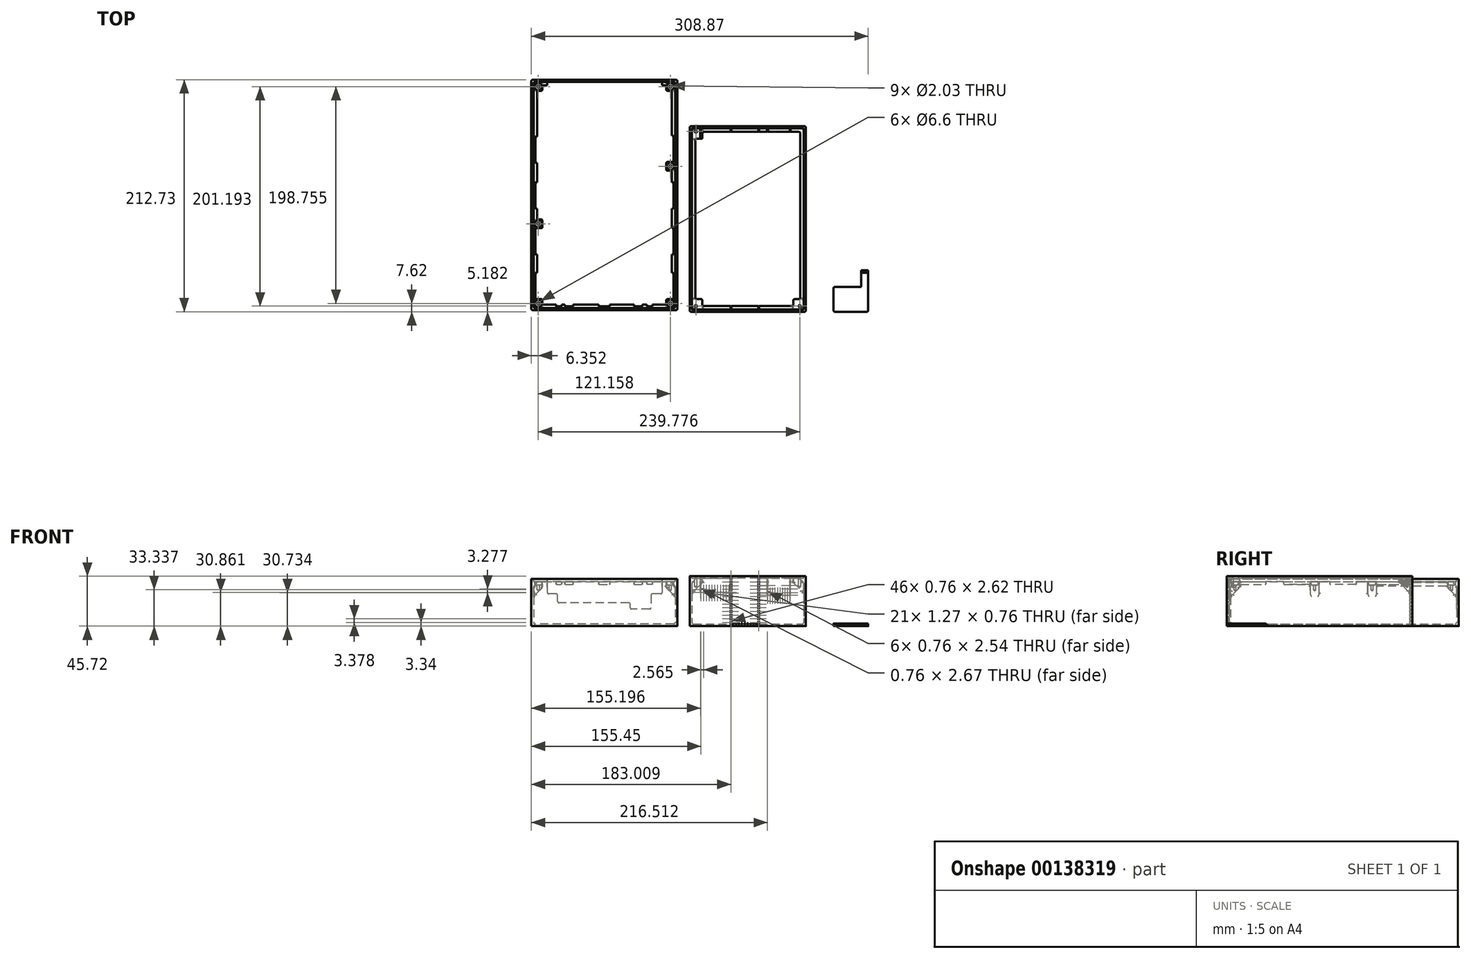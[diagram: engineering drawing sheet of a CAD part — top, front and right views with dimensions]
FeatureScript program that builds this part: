
annotation { "Feature Type Name" : "Feature", "Feature Type Description" : "" }
export const myFeature = defineFeature(function(context is Context, id is Id, definition is map)
    precondition{}
    {
        {
            var Q0;
            Q0=qCreatedBy(makeId("Top.planeOp"),FACE);
            var sketch = newSketch(context, id + "F0", { "sketchPlane" : qUnion([Q0])});
            skLineSegment(sketch, "E0.bottom", {"start": v(5.08, 5.08) * mm, "end": v(111.5, 5.08) * mm});
            skLineSegment(sketch, "E0.top", {"start": v(5.08, 175.13) * mm, "end": v(111.5, 175.13) * mm});
            skLineSegment(sketch, "E0.left", {"start": v(5.08, 5.08) * mm, "end": v(5.08, 175.13) * mm});
            skLineSegment(sketch, "E0.right", {"start": v(111.5, 5.08) * mm, "end": v(111.5, 175.13) * mm});
            skSolve(sketch);
        }
        {
            var Q0;
            Q0 = qSketchRegion(id + "F0", true);
            extrude(context, id + "F1", {"entities" : qUnion([Q0]), "depth" : 45.72 * mm, "offsetDistance" : 25.4 * mm});
        }
        {
            var Q0;
            Q0=makeQuery(id+"F1.opExtrude","CAP_FACE",FACE,{"disambiguationData":[OSD([sQuery(id+"F0.wireOp",EDGE,"E0.bottom"),sQuery(id+"F0.wireOp",EDGE,"E0.top"),sQuery(id+"F0.wireOp",EDGE,"E0.left"),sQuery(id+"F0.wireOp",EDGE,"E0.right")])],"isStart":false});
            shell(context, id + "F2", {"entities" : qUnion([Q0]), "thickness" : 2.03 * mm});
        }
        {
            var Q0;
            Q0=makeQuery(id+"F1.opExtrude","CAP_FACE",FACE,{"disambiguationData":[OSD([sQuery(id+"F0.wireOp",EDGE,"E0.bottom"),sQuery(id+"F0.wireOp",EDGE,"E0.top"),sQuery(id+"F0.wireOp",EDGE,"E0.left"),sQuery(id+"F0.wireOp",EDGE,"E0.right")])],"isStart":false});
            var sketch = newSketch(context, id + "F3", { "sketchPlane" : qUnion([Q0])});
            skLineSegment(sketch, "E1.0", {"start": v(16.64, 10.29) * mm, "end": v(99.95, 10.29) * mm});
            skLineSegment(sketch, "E1.1", {"start": v(10.29, 16.64) * mm, "end": v(10.29, 163.58) * mm});
            skLineSegment(sketch, "E1.2", {"start": v(16.64, 169.93) * mm, "end": v(106.3, 169.93) * mm});
            skLineSegment(sketch, "E1.3", {"start": v(106.3, 16.64) * mm, "end": v(106.3, 169.93) * mm});
            skLineSegment(sketch, "E2", {"start": v(109.47, 7.11) * mm, "end": v(7.11, 7.11) * mm});
            skLineSegment(sketch, "E3", {"start": v(7.11, 7.11) * mm, "end": v(7.11, 173.1) * mm});
            skLineSegment(sketch, "E4", {"start": v(7.11, 173.1) * mm, "end": v(109.47, 173.1) * mm});
            skLineSegment(sketch, "E5", {"start": v(109.47, 173.1) * mm, "end": v(109.47, 7.11) * mm});
            skLineSegment(sketch, "E6", {"start": v(16.64, 10.29) * mm, "end": v(16.64, 16.64) * mm});
            skLineSegment(sketch, "E7", {"start": v(16.64, 16.64) * mm, "end": v(10.29, 16.64) * mm});
            skLineSegment(sketch, "E8", {"start": v(106.3, 16.64) * mm, "end": v(99.95, 16.64) * mm});
            skLineSegment(sketch, "E9", {"start": v(99.95, 16.64) * mm, "end": v(99.95, 10.29) * mm});
            skLineSegment(sketch, "E10", {"start": v(16.64, 169.93) * mm, "end": v(16.64, 163.58) * mm});
            skLineSegment(sketch, "E11", {"start": v(16.64, 163.58) * mm, "end": v(10.29, 163.58) * mm});
            skSolve(sketch);
        }
        {
            var Q0;
            Q0 = qSketchRegion(id + "F3", true);
            extrude(context, id + "F4", {"entities" : qUnion([Q0]), "operationType" : NewBodyOperationType.ADD, "oppositeDirection" : true, "depth" : 15.24 * mm, "offsetDistance" : 25.4 * mm});
        }
        {
            var Q0;
            Q0=makeQuery(id+"F4.boolean.opBoolean","MERGE",FACE,{"derivedFrom":[makeQuery(id+"F1.opExtrude","CAP_FACE",FACE,{"disambiguationData":[OSD([sQuery(id+"F0.wireOp",EDGE,"E0.bottom"),sQuery(id+"F0.wireOp",EDGE,"E0.top"),sQuery(id+"F0.wireOp",EDGE,"E0.left"),sQuery(id+"F0.wireOp",EDGE,"E0.right")])],"isStart":false}),makeQuery(id+"F4.opExtrude","CAP_FACE",FACE,{"disambiguationData":[OSD([sQuery(id+"F3.wireOp",EDGE,"E1.0"),sQuery(id+"F3.wireOp",EDGE,"E1.1"),sQuery(id+"F3.wireOp",EDGE,"E1.2"),sQuery(id+"F3.wireOp",EDGE,"E1.3"),sQuery(id+"F3.wireOp",EDGE,"E2"),sQuery(id+"F3.wireOp",EDGE,"E3"),sQuery(id+"F3.wireOp",EDGE,"E4"),sQuery(id+"F3.wireOp",EDGE,"E5")])],"isStart":true})]});
            var sketch = newSketch(context, id + "F5", { "sketchPlane" : qUnion([Q0])});
            skLineSegment(sketch, "E12.0", {"start": v(7.11, 7.11) * mm, "end": v(109.47, 7.11) * mm});
            skLineSegment(sketch, "E12.1", {"start": v(7.11, 7.11) * mm, "end": v(7.11, 173.1) * mm});
            skLineSegment(sketch, "E12.2", {"start": v(7.11, 173.1) * mm, "end": v(109.47, 173.1) * mm});
            skLineSegment(sketch, "E12.3", {"start": v(109.47, 7.11) * mm, "end": v(109.47, 173.1) * mm});
            skSolve(sketch);
        }
        {
            var Q0;
            Q0 = qSketchRegion(id + "F5", true);
            extrude(context, id + "F6", {"entities" : qUnion([Q0]), "operationType" : NewBodyOperationType.REMOVE, "oppositeDirection" : true, "depth" : 1.65 * mm, "offsetDistance" : 25.4 * mm});
        }
        {
            var Q0;
            Q0=makeQuery(id+"F4.opExtrude","CAP_EDGE",EDGE,{"disambiguationData":[OSD([sQuery(id+"F3.wireOp",EDGE,"E1.0")])],"isStart":false});
            var Q1;
            Q1=makeQuery(id+"F4.opExtrude","CAP_EDGE",EDGE,{"disambiguationData":[OSD([sQuery(id+"F3.wireOp",EDGE,"E1.1")])],"isStart":false});
            var Q2;
            Q2=makeQuery(id+"F4.opExtrude","CAP_EDGE",EDGE,{"disambiguationData":[OSD([sQuery(id+"F3.wireOp",EDGE,"E1.3")])],"isStart":false});
            var Q3;
            Q3=makeQuery(id+"F4.opExtrude","CAP_EDGE",EDGE,{"disambiguationData":[OSD([sQuery(id+"F3.wireOp",EDGE,"E1.2")])],"isStart":false});
            chamfer(context, id + "F7", {"entities" : qUnion([Q0, Q1, Q2, Q3]), "width" : 12.7 * mm, "tangentPropagation" : true});
        }
        {
            var Q0;
            Q0=makeQuery(id+"F4.opExtrude","CAP_EDGE",EDGE,{"disambiguationData":[OSD([sQuery(id+"F3.wireOp",EDGE,"E8")])],"isStart":false});
            var Q1;
            Q1=makeQuery(id+"F4.opExtrude","CAP_EDGE",EDGE,{"disambiguationData":[OSD([sQuery(id+"F3.wireOp",EDGE,"E9")])],"isStart":false});
            var Q2;
            Q2=makeQuery(id+"F4.opExtrude","CAP_EDGE",EDGE,{"disambiguationData":[OSD([sQuery(id+"F3.wireOp",EDGE,"E11")])],"isStart":false});
            var Q3;
            Q3=makeQuery(id+"F4.opExtrude","CAP_EDGE",EDGE,{"disambiguationData":[OSD([sQuery(id+"F3.wireOp",EDGE,"E10")])],"isStart":false});
            var Q4;
            Q4=makeQuery(id+"F4.opExtrude","CAP_EDGE",EDGE,{"disambiguationData":[OSD([sQuery(id+"F3.wireOp",EDGE,"E7")])],"isStart":false});
            var Q5;
            Q5=makeQuery(id+"F4.opExtrude","CAP_EDGE",EDGE,{"disambiguationData":[OSD([sQuery(id+"F3.wireOp",EDGE,"E6")])],"isStart":false});
            chamfer(context, id + "F8", {"entities" : qUnion([Q0, Q1, Q2, Q3, Q4, Q5]), "width" : 9.52 * mm, "tangentPropagation" : true});
        }
        {
            var Q0;
            Q0=makeQuery(id+"F4.opExtrude","SWEPT_EDGE",EDGE,{"disambiguationData":[OSD([sQuery(id+"F3.wireOp",EDGE,"E6"),sQuery(id+"F3.wireOp",EDGE,"E7")])]});
            var Q1;
            {var subQ0=sQuery(id+"F3.wireOp",EDGE,"E7");Q1=makeQuery(id+"F8.opChamfer","BLEND_EDGE",EDGE,{"blendedFrom":[makeQuery(id+"F4.opExtrude","CAP_EDGE",EDGE,{"disambiguationData":[OSD([subQ0])],"isStart":false}),makeQuery(id+"F4.opExtrude","SWEPT_FACE",FACE,{"disambiguationData":[OSD([subQ0])]})],"blendedInto":[makeQuery(id+"F4.opExtrude","SWEPT_FACE",FACE,{"disambiguationData":[OSD([subQ0])]})]});}
            var Q2;
            Q2=makeQuery(id+"F8.opChamfer","BLEND_EDGE",EDGE,{"blendedFrom":[makeQuery(id+"F4.opExtrude","CAP_EDGE",EDGE,{"disambiguationData":[OSD([sQuery(id+"F3.wireOp",EDGE,"E6")])],"isStart":false}),makeQuery(id+"F4.opExtrude","CAP_EDGE",EDGE,{"disambiguationData":[OSD([sQuery(id+"F3.wireOp",EDGE,"E7")])],"isStart":false})],"blendedInto":[]});
            var Q3;
            {var subQ0=sQuery(id+"F3.wireOp",EDGE,"E6");Q3=makeQuery(id+"F8.opChamfer","BLEND_EDGE",EDGE,{"blendedFrom":[makeQuery(id+"F4.opExtrude","CAP_EDGE",EDGE,{"disambiguationData":[OSD([subQ0])],"isStart":false}),makeQuery(id+"F4.opExtrude","SWEPT_FACE",FACE,{"disambiguationData":[OSD([subQ0])]})],"blendedInto":[makeQuery(id+"F4.opExtrude","SWEPT_FACE",FACE,{"disambiguationData":[OSD([subQ0])]})]});}
            var Q4;
            {var subQ0=sQuery(id+"F3.wireOp",EDGE,"E1.0");Q4=makeQuery(id+"F7.opChamfer","BLEND_EDGE",EDGE,{"blendedFrom":[makeQuery(id+"F4.opExtrude","CAP_EDGE",EDGE,{"disambiguationData":[OSD([subQ0])],"isStart":false}),makeQuery(id+"F4.opExtrude","SWEPT_FACE",FACE,{"disambiguationData":[OSD([subQ0])]})],"blendedInto":[makeQuery(id+"F4.opExtrude","SWEPT_FACE",FACE,{"disambiguationData":[OSD([subQ0])]})]});}
            var Q5;
            Q5=makeQuery(id+"F7.opChamfer","BLEND_EDGE",EDGE,{"blendedFrom":[makeQuery(id+"F4.opExtrude","CAP_EDGE",EDGE,{"disambiguationData":[OSD([sQuery(id+"F3.wireOp",EDGE,"E1.0")])],"isStart":false}),makeQuery(id+"F2.opShell","OFFSET_FACE",FACE,{"disambiguationData":[OSD([sQuery(id+"F0.wireOp",EDGE,"E0.bottom")])]})],"blendedInto":[makeQuery(id+"F2.opShell","OFFSET_FACE",FACE,{"disambiguationData":[OSD([sQuery(id+"F0.wireOp",EDGE,"E0.bottom")])]})]});
            var Q6;
            {var subQ0=sQuery(id+"F3.wireOp",EDGE,"E1.1");Q6=makeQuery(id+"F7.opChamfer","BLEND_EDGE",EDGE,{"blendedFrom":[makeQuery(id+"F4.opExtrude","CAP_EDGE",EDGE,{"disambiguationData":[OSD([subQ0])],"isStart":false}),makeQuery(id+"F4.opExtrude","SWEPT_FACE",FACE,{"disambiguationData":[OSD([subQ0])]})],"blendedInto":[makeQuery(id+"F4.opExtrude","SWEPT_FACE",FACE,{"disambiguationData":[OSD([subQ0])]})]});}
            var Q7;
            Q7=makeQuery(id+"F4.opExtrude","SWEPT_EDGE",EDGE,{"disambiguationData":[OSD([sQuery(id+"F3.wireOp",EDGE,"E8"),sQuery(id+"F3.wireOp",EDGE,"E9")])]});
            var Q8;
            Q8=makeQuery(id+"F8.opChamfer","BLEND_EDGE",EDGE,{"blendedFrom":[makeQuery(id+"F4.opExtrude","CAP_EDGE",EDGE,{"disambiguationData":[OSD([sQuery(id+"F3.wireOp",EDGE,"E8")])],"isStart":false}),makeQuery(id+"F4.opExtrude","CAP_EDGE",EDGE,{"disambiguationData":[OSD([sQuery(id+"F3.wireOp",EDGE,"E9")])],"isStart":false})],"blendedInto":[]});
            var Q9;
            {var subQ0=sQuery(id+"F3.wireOp",EDGE,"E9");Q9=makeQuery(id+"F8.opChamfer","BLEND_EDGE",EDGE,{"blendedFrom":[makeQuery(id+"F4.opExtrude","CAP_EDGE",EDGE,{"disambiguationData":[OSD([subQ0])],"isStart":false}),makeQuery(id+"F4.opExtrude","SWEPT_FACE",FACE,{"disambiguationData":[OSD([subQ0])]})],"blendedInto":[makeQuery(id+"F4.opExtrude","SWEPT_FACE",FACE,{"disambiguationData":[OSD([subQ0])]})]});}
            var Q10;
            {var subQ0=sQuery(id+"F3.wireOp",EDGE,"E8");Q10=makeQuery(id+"F8.opChamfer","BLEND_EDGE",EDGE,{"blendedFrom":[makeQuery(id+"F4.opExtrude","CAP_EDGE",EDGE,{"disambiguationData":[OSD([subQ0])],"isStart":false}),makeQuery(id+"F4.opExtrude","SWEPT_FACE",FACE,{"disambiguationData":[OSD([subQ0])]})],"blendedInto":[makeQuery(id+"F4.opExtrude","SWEPT_FACE",FACE,{"disambiguationData":[OSD([subQ0])]})]});}
            var Q11;
            {var subQ0=sQuery(id+"F3.wireOp",EDGE,"E1.3");Q11=makeQuery(id+"F7.opChamfer","BLEND_EDGE",EDGE,{"blendedFrom":[makeQuery(id+"F4.opExtrude","CAP_EDGE",EDGE,{"disambiguationData":[OSD([subQ0])],"isStart":false}),makeQuery(id+"F4.opExtrude","SWEPT_FACE",FACE,{"disambiguationData":[OSD([subQ0])]})],"blendedInto":[makeQuery(id+"F4.opExtrude","SWEPT_FACE",FACE,{"disambiguationData":[OSD([subQ0])]})]});}
            var Q12;
            Q12=makeQuery(id+"F7.opChamfer","BLEND_EDGE",EDGE,{"blendedFrom":[makeQuery(id+"F4.opExtrude","CAP_EDGE",EDGE,{"disambiguationData":[OSD([sQuery(id+"F3.wireOp",EDGE,"E1.3")])],"isStart":false}),makeQuery(id+"F2.opShell","OFFSET_FACE",FACE,{"disambiguationData":[OSD([sQuery(id+"F0.wireOp",EDGE,"E0.right")])]})],"blendedInto":[makeQuery(id+"F2.opShell","OFFSET_FACE",FACE,{"disambiguationData":[OSD([sQuery(id+"F0.wireOp",EDGE,"E0.right")])]})]});
            var Q13;
            Q13=makeQuery(id+"F4.opExtrude","SWEPT_EDGE",EDGE,{"disambiguationData":[OSD([sQuery(id+"F3.wireOp",EDGE,"E10"),sQuery(id+"F3.wireOp",EDGE,"E11")])]});
            var Q14;
            {var subQ0=sQuery(id+"F3.wireOp",EDGE,"E10");Q14=makeQuery(id+"F8.opChamfer","BLEND_EDGE",EDGE,{"blendedFrom":[makeQuery(id+"F4.opExtrude","CAP_EDGE",EDGE,{"disambiguationData":[OSD([subQ0])],"isStart":false}),makeQuery(id+"F4.opExtrude","SWEPT_FACE",FACE,{"disambiguationData":[OSD([subQ0])]})],"blendedInto":[makeQuery(id+"F4.opExtrude","SWEPT_FACE",FACE,{"disambiguationData":[OSD([subQ0])]})]});}
            var Q15;
            {var subQ0=sQuery(id+"F3.wireOp",EDGE,"E11");Q15=makeQuery(id+"F8.opChamfer","BLEND_EDGE",EDGE,{"blendedFrom":[makeQuery(id+"F4.opExtrude","CAP_EDGE",EDGE,{"disambiguationData":[OSD([subQ0])],"isStart":false}),makeQuery(id+"F4.opExtrude","SWEPT_FACE",FACE,{"disambiguationData":[OSD([subQ0])]})],"blendedInto":[makeQuery(id+"F4.opExtrude","SWEPT_FACE",FACE,{"disambiguationData":[OSD([subQ0])]})]});}
            var Q16;
            Q16=makeQuery(id+"F8.opChamfer","BLEND_EDGE",EDGE,{"blendedFrom":[makeQuery(id+"F4.opExtrude","CAP_EDGE",EDGE,{"disambiguationData":[OSD([sQuery(id+"F3.wireOp",EDGE,"E10")])],"isStart":false}),makeQuery(id+"F4.opExtrude","CAP_EDGE",EDGE,{"disambiguationData":[OSD([sQuery(id+"F3.wireOp",EDGE,"E11")])],"isStart":false})],"blendedInto":[]});
            var Q17;
            Q17=makeQuery(id+"F7.opChamfer","BLEND_EDGE",EDGE,{"blendedFrom":[makeQuery(id+"F4.opExtrude","CAP_EDGE",EDGE,{"disambiguationData":[OSD([sQuery(id+"F3.wireOp",EDGE,"E1.1")])],"isStart":false}),makeQuery(id+"F2.opShell","OFFSET_FACE",FACE,{"disambiguationData":[OSD([sQuery(id+"F0.wireOp",EDGE,"E0.left")])]})],"blendedInto":[makeQuery(id+"F2.opShell","OFFSET_FACE",FACE,{"disambiguationData":[OSD([sQuery(id+"F0.wireOp",EDGE,"E0.left")])]})]});
            var Q18;
            {var subQ0=sQuery(id+"F3.wireOp",EDGE,"E1.2");Q18=makeQuery(id+"F7.opChamfer","BLEND_EDGE",EDGE,{"blendedFrom":[makeQuery(id+"F4.opExtrude","CAP_EDGE",EDGE,{"disambiguationData":[OSD([subQ0])],"isStart":false}),makeQuery(id+"F4.opExtrude","SWEPT_FACE",FACE,{"disambiguationData":[OSD([subQ0])]})],"blendedInto":[makeQuery(id+"F4.opExtrude","SWEPT_FACE",FACE,{"disambiguationData":[OSD([subQ0])]})]});}
            var Q19;
            Q19=makeQuery(id+"F7.opChamfer","BLEND_EDGE",EDGE,{"blendedFrom":[makeQuery(id+"F4.opExtrude","CAP_EDGE",EDGE,{"disambiguationData":[OSD([sQuery(id+"F3.wireOp",EDGE,"E1.2")])],"isStart":false}),makeQuery(id+"F2.opShell","OFFSET_FACE",FACE,{"disambiguationData":[OSD([sQuery(id+"F0.wireOp",EDGE,"E0.top")])]})],"blendedInto":[makeQuery(id+"F2.opShell","OFFSET_FACE",FACE,{"disambiguationData":[OSD([sQuery(id+"F0.wireOp",EDGE,"E0.top")])]})]});
            fillet(context, id + "F9", {"entities" : qUnion([Q0, Q1, Q2, Q3, Q4, Q5, Q6, Q7, Q8, Q9, Q10, Q11, Q12, Q13, Q14, Q15, Q16, Q17, Q18, Q19]), "tangentPropagation" : true, "radius" : 1.27 * mm, "defaultsChanged" : false, "vertexSettings" : [], "allowEdgeOverflow" : false});
        }
        {
            var Q0;
            Q0=makeQuery(id+"F1.opExtrude","SWEPT_FACE",FACE,{"disambiguationData":[OSD([sQuery(id+"F0.wireOp",EDGE,"E0.bottom")])]});
            var sketch = newSketch(context, id + "F10", { "sketchPlane" : qUnion([Q0])});
            skLineSegment(sketch, "E13.bottom", {"start": v(42.42, 2.03) * mm, "end": v(43.18, 2.03) * mm});
            skLineSegment(sketch, "E13.top", {"start": v(42.42, 4.65) * mm, "end": v(43.18, 4.65) * mm});
            skLineSegment(sketch, "E13.left", {"start": v(42.42, 2.03) * mm, "end": v(42.42, 4.65) * mm});
            skLineSegment(sketch, "E13.right", {"start": v(43.18, 2.03) * mm, "end": v(43.18, 4.65) * mm});
            skLineSegment(sketch, "E14.0.1.0", {"start": v(42.42, 8.03) * mm, "end": v(43.18, 8.03) * mm});
            skLineSegment(sketch, "E14.0.1.1", {"start": v(42.42, 5.41) * mm, "end": v(43.18, 5.41) * mm});
            skLineSegment(sketch, "E14.0.1.2", {"start": v(43.18, 5.41) * mm, "end": v(43.18, 8.03) * mm});
            skLineSegment(sketch, "E14.0.1.3", {"start": v(42.42, 5.41) * mm, "end": v(42.42, 8.03) * mm});
            skLineSegment(sketch, "E14.0.2.0", {"start": v(42.42, 11.4) * mm, "end": v(43.18, 11.4) * mm});
            skLineSegment(sketch, "E14.0.2.1", {"start": v(42.42, 8.79) * mm, "end": v(43.18, 8.79) * mm});
            skLineSegment(sketch, "E14.0.2.2", {"start": v(43.18, 8.79) * mm, "end": v(43.18, 11.4) * mm});
            skLineSegment(sketch, "E14.0.2.3", {"start": v(42.42, 8.79) * mm, "end": v(42.42, 11.4) * mm});
            skLineSegment(sketch, "E14.0.3.0", {"start": v(42.42, 14.78) * mm, "end": v(43.18, 14.78) * mm});
            skLineSegment(sketch, "E14.0.3.1", {"start": v(42.42, 12.17) * mm, "end": v(43.18, 12.17) * mm});
            skLineSegment(sketch, "E14.0.3.2", {"start": v(43.18, 12.17) * mm, "end": v(43.18, 14.78) * mm});
            skLineSegment(sketch, "E14.0.3.3", {"start": v(42.42, 12.17) * mm, "end": v(42.42, 14.78) * mm});
            skLineSegment(sketch, "E14.0.4.0", {"start": v(42.42, 18.16) * mm, "end": v(43.18, 18.16) * mm});
            skLineSegment(sketch, "E14.0.4.1", {"start": v(42.42, 15.54) * mm, "end": v(43.18, 15.54) * mm});
            skLineSegment(sketch, "E14.0.4.2", {"start": v(43.18, 15.54) * mm, "end": v(43.18, 18.16) * mm});
            skLineSegment(sketch, "E14.0.4.3", {"start": v(42.42, 15.54) * mm, "end": v(42.42, 18.16) * mm});
            skLineSegment(sketch, "E14.0.5.0", {"start": v(42.42, 21.54) * mm, "end": v(43.18, 21.54) * mm});
            skLineSegment(sketch, "E14.0.5.1", {"start": v(42.42, 18.92) * mm, "end": v(43.18, 18.92) * mm});
            skLineSegment(sketch, "E14.0.5.2", {"start": v(43.18, 18.92) * mm, "end": v(43.18, 21.54) * mm});
            skLineSegment(sketch, "E14.0.5.3", {"start": v(42.42, 18.92) * mm, "end": v(42.42, 21.54) * mm});
            skLineSegment(sketch, "E14.0.6.0", {"start": v(42.42, 24.92) * mm, "end": v(43.18, 24.92) * mm});
            skLineSegment(sketch, "E14.0.6.1", {"start": v(42.42, 22.3) * mm, "end": v(43.18, 22.3) * mm});
            skLineSegment(sketch, "E14.0.6.2", {"start": v(43.18, 22.3) * mm, "end": v(43.18, 24.92) * mm});
            skLineSegment(sketch, "E14.0.6.3", {"start": v(42.42, 22.3) * mm, "end": v(42.42, 24.92) * mm});
            skLineSegment(sketch, "E14.0.7.0", {"start": v(42.42, 28.3) * mm, "end": v(43.18, 28.3) * mm});
            skLineSegment(sketch, "E14.0.7.1", {"start": v(42.42, 25.68) * mm, "end": v(43.18, 25.68) * mm});
            skLineSegment(sketch, "E14.0.7.2", {"start": v(43.18, 25.68) * mm, "end": v(43.18, 28.3) * mm});
            skLineSegment(sketch, "E14.0.7.3", {"start": v(42.42, 25.68) * mm, "end": v(42.42, 28.3) * mm});
            skLineSegment(sketch, "E14.0.8.0", {"start": v(42.42, 31.67) * mm, "end": v(43.18, 31.67) * mm});
            skLineSegment(sketch, "E14.0.8.1", {"start": v(42.42, 29.06) * mm, "end": v(43.18, 29.06) * mm});
            skLineSegment(sketch, "E14.0.8.2", {"start": v(43.18, 29.06) * mm, "end": v(43.18, 31.67) * mm});
            skLineSegment(sketch, "E14.0.8.3", {"start": v(42.42, 29.06) * mm, "end": v(42.42, 31.67) * mm});
            skLineSegment(sketch, "E14.0.9.0", {"start": v(42.42, 35.05) * mm, "end": v(43.18, 35.05) * mm});
            skLineSegment(sketch, "E14.0.9.1", {"start": v(42.42, 32.44) * mm, "end": v(43.18, 32.44) * mm});
            skLineSegment(sketch, "E14.0.9.2", {"start": v(43.18, 32.44) * mm, "end": v(43.18, 35.05) * mm});
            skLineSegment(sketch, "E14.0.9.3", {"start": v(42.42, 32.44) * mm, "end": v(42.42, 35.05) * mm});
            skLineSegment(sketch, "E14.0.10.0", {"start": v(42.42, 38.43) * mm, "end": v(43.18, 38.43) * mm});
            skLineSegment(sketch, "E14.0.10.1", {"start": v(42.42, 35.81) * mm, "end": v(43.18, 35.81) * mm});
            skLineSegment(sketch, "E14.0.10.2", {"start": v(43.18, 35.81) * mm, "end": v(43.18, 38.43) * mm});
            skLineSegment(sketch, "E14.0.10.3", {"start": v(42.42, 35.81) * mm, "end": v(42.42, 38.43) * mm});
            skLineSegment(sketch, "E14.0.11.0", {"start": v(42.42, 41.8) * mm, "end": v(43.18, 41.8) * mm});
            skLineSegment(sketch, "E14.0.11.1", {"start": v(42.42, 39.2) * mm, "end": v(43.18, 39.2) * mm});
            skLineSegment(sketch, "E14.0.11.2", {"start": v(43.18, 39.2) * mm, "end": v(43.18, 41.8) * mm});
            skLineSegment(sketch, "E14.0.11.3", {"start": v(42.42, 39.2) * mm, "end": v(42.42, 41.8) * mm});
            skLineSegment(sketch, "E14.0.12.0", {"start": v(42.42, 45.19) * mm, "end": v(43.18, 45.19) * mm});
            skLineSegment(sketch, "E14.0.12.1", {"start": v(42.42, 42.57) * mm, "end": v(43.18, 42.57) * mm});
            skLineSegment(sketch, "E14.0.12.2", {"start": v(43.18, 42.57) * mm, "end": v(43.18, 45.19) * mm});
            skLineSegment(sketch, "E14.0.12.3", {"start": v(42.42, 42.57) * mm, "end": v(42.42, 45.19) * mm});
            skLineSegment(sketch, "E14.1.0.0", {"start": v(67.82, 4.65) * mm, "end": v(68.58, 4.65) * mm});
            skLineSegment(sketch, "E14.1.0.1", {"start": v(67.82, 2.03) * mm, "end": v(68.58, 2.03) * mm});
            skLineSegment(sketch, "E14.1.0.2", {"start": v(68.58, 2.03) * mm, "end": v(68.58, 4.65) * mm});
            skLineSegment(sketch, "E14.1.0.3", {"start": v(67.82, 2.03) * mm, "end": v(67.82, 4.65) * mm});
            skLineSegment(sketch, "E14.1.1.0", {"start": v(67.82, 8.03) * mm, "end": v(68.58, 8.03) * mm});
            skLineSegment(sketch, "E14.1.1.1", {"start": v(67.82, 5.41) * mm, "end": v(68.58, 5.41) * mm});
            skLineSegment(sketch, "E14.1.1.2", {"start": v(68.58, 5.41) * mm, "end": v(68.58, 8.03) * mm});
            skLineSegment(sketch, "E14.1.1.3", {"start": v(67.82, 5.41) * mm, "end": v(67.82, 8.03) * mm});
            skLineSegment(sketch, "E14.1.2.0", {"start": v(67.82, 11.4) * mm, "end": v(68.58, 11.4) * mm});
            skLineSegment(sketch, "E14.1.2.1", {"start": v(67.82, 8.79) * mm, "end": v(68.58, 8.79) * mm});
            skLineSegment(sketch, "E14.1.2.2", {"start": v(68.58, 8.79) * mm, "end": v(68.58, 11.4) * mm});
            skLineSegment(sketch, "E14.1.2.3", {"start": v(67.82, 8.79) * mm, "end": v(67.82, 11.4) * mm});
            skLineSegment(sketch, "E14.1.3.0", {"start": v(67.82, 14.78) * mm, "end": v(68.58, 14.78) * mm});
            skLineSegment(sketch, "E14.1.3.1", {"start": v(67.82, 12.17) * mm, "end": v(68.58, 12.17) * mm});
            skLineSegment(sketch, "E14.1.3.2", {"start": v(68.58, 12.17) * mm, "end": v(68.58, 14.78) * mm});
            skLineSegment(sketch, "E14.1.3.3", {"start": v(67.82, 12.17) * mm, "end": v(67.82, 14.78) * mm});
            skLineSegment(sketch, "E14.1.4.0", {"start": v(67.82, 18.16) * mm, "end": v(68.58, 18.16) * mm});
            skLineSegment(sketch, "E14.1.4.1", {"start": v(67.82, 15.54) * mm, "end": v(68.58, 15.54) * mm});
            skLineSegment(sketch, "E14.1.4.2", {"start": v(68.58, 15.54) * mm, "end": v(68.58, 18.16) * mm});
            skLineSegment(sketch, "E14.1.4.3", {"start": v(67.82, 15.54) * mm, "end": v(67.82, 18.16) * mm});
            skLineSegment(sketch, "E14.1.5.0", {"start": v(67.82, 21.54) * mm, "end": v(68.58, 21.54) * mm});
            skLineSegment(sketch, "E14.1.5.1", {"start": v(67.82, 18.92) * mm, "end": v(68.58, 18.92) * mm});
            skLineSegment(sketch, "E14.1.5.2", {"start": v(68.58, 18.92) * mm, "end": v(68.58, 21.54) * mm});
            skLineSegment(sketch, "E14.1.5.3", {"start": v(67.82, 18.92) * mm, "end": v(67.82, 21.54) * mm});
            skLineSegment(sketch, "E14.1.6.0", {"start": v(67.82, 24.92) * mm, "end": v(68.58, 24.92) * mm});
            skLineSegment(sketch, "E14.1.6.1", {"start": v(67.82, 22.3) * mm, "end": v(68.58, 22.3) * mm});
            skLineSegment(sketch, "E14.1.6.2", {"start": v(68.58, 22.3) * mm, "end": v(68.58, 24.92) * mm});
            skLineSegment(sketch, "E14.1.6.3", {"start": v(67.82, 22.3) * mm, "end": v(67.82, 24.92) * mm});
            skLineSegment(sketch, "E14.1.7.0", {"start": v(67.82, 28.3) * mm, "end": v(68.58, 28.3) * mm});
            skLineSegment(sketch, "E14.1.7.1", {"start": v(67.82, 25.68) * mm, "end": v(68.58, 25.68) * mm});
            skLineSegment(sketch, "E14.1.7.2", {"start": v(68.58, 25.68) * mm, "end": v(68.58, 28.3) * mm});
            skLineSegment(sketch, "E14.1.7.3", {"start": v(67.82, 25.68) * mm, "end": v(67.82, 28.3) * mm});
            skLineSegment(sketch, "E14.1.8.0", {"start": v(67.82, 31.67) * mm, "end": v(68.58, 31.67) * mm});
            skLineSegment(sketch, "E14.1.8.1", {"start": v(67.82, 29.06) * mm, "end": v(68.58, 29.06) * mm});
            skLineSegment(sketch, "E14.1.8.2", {"start": v(68.58, 29.06) * mm, "end": v(68.58, 31.67) * mm});
            skLineSegment(sketch, "E14.1.8.3", {"start": v(67.82, 29.06) * mm, "end": v(67.82, 31.67) * mm});
            skLineSegment(sketch, "E14.1.9.0", {"start": v(67.82, 35.05) * mm, "end": v(68.58, 35.05) * mm});
            skLineSegment(sketch, "E14.1.9.1", {"start": v(67.82, 32.44) * mm, "end": v(68.58, 32.44) * mm});
            skLineSegment(sketch, "E14.1.9.2", {"start": v(68.58, 32.44) * mm, "end": v(68.58, 35.05) * mm});
            skLineSegment(sketch, "E14.1.9.3", {"start": v(67.82, 32.44) * mm, "end": v(67.82, 35.05) * mm});
            skLineSegment(sketch, "E14.1.10.0", {"start": v(67.82, 38.43) * mm, "end": v(68.58, 38.43) * mm});
            skLineSegment(sketch, "E14.1.10.1", {"start": v(67.82, 35.81) * mm, "end": v(68.58, 35.81) * mm});
            skLineSegment(sketch, "E14.1.10.2", {"start": v(68.58, 35.81) * mm, "end": v(68.58, 38.43) * mm});
            skLineSegment(sketch, "E14.1.10.3", {"start": v(67.82, 35.81) * mm, "end": v(67.82, 38.43) * mm});
            skLineSegment(sketch, "E14.1.11.0", {"start": v(67.82, 41.8) * mm, "end": v(68.58, 41.8) * mm});
            skLineSegment(sketch, "E14.1.11.1", {"start": v(67.82, 39.2) * mm, "end": v(68.58, 39.2) * mm});
            skLineSegment(sketch, "E14.1.11.2", {"start": v(68.58, 39.2) * mm, "end": v(68.58, 41.8) * mm});
            skLineSegment(sketch, "E14.1.11.3", {"start": v(67.82, 39.2) * mm, "end": v(67.82, 41.8) * mm});
            skLineSegment(sketch, "E14.1.12.0", {"start": v(67.82, 45.19) * mm, "end": v(68.58, 45.19) * mm});
            skLineSegment(sketch, "E14.1.12.1", {"start": v(67.82, 42.57) * mm, "end": v(68.58, 42.57) * mm});
            skLineSegment(sketch, "E14.1.12.2", {"start": v(68.58, 42.57) * mm, "end": v(68.58, 45.19) * mm});
            skLineSegment(sketch, "E14.1.12.3", {"start": v(67.82, 42.57) * mm, "end": v(67.82, 45.19) * mm});
            skLineSegment(sketch, "E14.direction1", {"start": v(42.42, 2.03) * mm, "end": v(67.82, 2.03) * mm, "construction": true});
            skLineSegment(sketch, "E14.direction2", {"start": v(42.42, 2.03) * mm, "end": v(42.42, 5.41) * mm, "construction": true});
            skLineSegment(sketch, "E15.bottom", {"start": v(44.2, 2.8) * mm, "end": v(45.47, 2.8) * mm});
            skLineSegment(sketch, "E15.top", {"start": v(44.2, 2.03) * mm, "end": v(45.47, 2.03) * mm});
            skLineSegment(sketch, "E15.left", {"start": v(44.2, 2.8) * mm, "end": v(44.2, 2.03) * mm});
            skLineSegment(sketch, "E15.right", {"start": v(45.47, 2.8) * mm, "end": v(45.47, 2.03) * mm});
            skLineSegment(sketch, "E16.1.0.0", {"start": v(46.86, 2.8) * mm, "end": v(46.86, 2.03) * mm});
            skLineSegment(sketch, "E16.1.0.1", {"start": v(48.13, 2.8) * mm, "end": v(48.13, 2.03) * mm});
            skLineSegment(sketch, "E16.1.0.2", {"start": v(46.86, 2.8) * mm, "end": v(48.13, 2.8) * mm});
            skLineSegment(sketch, "E16.1.0.3", {"start": v(46.86, 2.03) * mm, "end": v(48.13, 2.03) * mm});
            skLineSegment(sketch, "E16.2.0.0", {"start": v(49.53, 2.8) * mm, "end": v(49.53, 2.03) * mm});
            skLineSegment(sketch, "E16.2.0.1", {"start": v(50.8, 2.8) * mm, "end": v(50.8, 2.03) * mm});
            skLineSegment(sketch, "E16.2.0.2", {"start": v(49.53, 2.8) * mm, "end": v(50.8, 2.8) * mm});
            skLineSegment(sketch, "E16.2.0.3", {"start": v(49.53, 2.03) * mm, "end": v(50.8, 2.03) * mm});
            skLineSegment(sketch, "E16.3.0.0", {"start": v(52.2, 2.8) * mm, "end": v(52.2, 2.03) * mm});
            skLineSegment(sketch, "E16.3.0.1", {"start": v(53.47, 2.8) * mm, "end": v(53.47, 2.03) * mm});
            skLineSegment(sketch, "E16.3.0.2", {"start": v(52.2, 2.8) * mm, "end": v(53.47, 2.8) * mm});
            skLineSegment(sketch, "E16.3.0.3", {"start": v(52.2, 2.03) * mm, "end": v(53.47, 2.03) * mm});
            skLineSegment(sketch, "E16.4.0.0", {"start": v(54.86, 2.8) * mm, "end": v(54.86, 2.03) * mm});
            skLineSegment(sketch, "E16.4.0.1", {"start": v(56.13, 2.8) * mm, "end": v(56.13, 2.03) * mm});
            skLineSegment(sketch, "E16.4.0.2", {"start": v(54.86, 2.8) * mm, "end": v(56.13, 2.8) * mm});
            skLineSegment(sketch, "E16.4.0.3", {"start": v(54.86, 2.03) * mm, "end": v(56.13, 2.03) * mm});
            skLineSegment(sketch, "E16.5.0.0", {"start": v(57.53, 2.8) * mm, "end": v(57.53, 2.03) * mm});
            skLineSegment(sketch, "E16.5.0.1", {"start": v(58.8, 2.8) * mm, "end": v(58.8, 2.03) * mm});
            skLineSegment(sketch, "E16.5.0.2", {"start": v(57.53, 2.8) * mm, "end": v(58.8, 2.8) * mm});
            skLineSegment(sketch, "E16.5.0.3", {"start": v(57.53, 2.03) * mm, "end": v(58.8, 2.03) * mm});
            skLineSegment(sketch, "E16.6.0.0", {"start": v(60.2, 2.8) * mm, "end": v(60.2, 2.03) * mm});
            skLineSegment(sketch, "E16.6.0.1", {"start": v(61.47, 2.8) * mm, "end": v(61.47, 2.03) * mm});
            skLineSegment(sketch, "E16.6.0.2", {"start": v(60.2, 2.8) * mm, "end": v(61.47, 2.8) * mm});
            skLineSegment(sketch, "E16.6.0.3", {"start": v(60.2, 2.03) * mm, "end": v(61.47, 2.03) * mm});
            skLineSegment(sketch, "E16.direction1", {"start": v(44.2, 2.03) * mm, "end": v(46.86, 2.03) * mm, "construction": true});
            skLineSegment(sketch, "E17.0.7.0", {"start": v(62.87, 2.8) * mm, "end": v(62.87, 2.03) * mm});
            skLineSegment(sketch, "E17.3.7.0", {"start": v(64.14, 2.8) * mm, "end": v(64.14, 2.03) * mm});
            skLineSegment(sketch, "E17.6.7.0", {"start": v(62.87, 2.8) * mm, "end": v(64.14, 2.8) * mm});
            skLineSegment(sketch, "E17.9.7.0", {"start": v(62.87, 2.03) * mm, "end": v(64.14, 2.03) * mm});
            skLineSegment(sketch, "E17.0.8.0", {"start": v(65.53, 2.8) * mm, "end": v(65.53, 2.03) * mm});
            skLineSegment(sketch, "E17.3.8.0", {"start": v(66.8, 2.8) * mm, "end": v(66.8, 2.03) * mm});
            skLineSegment(sketch, "E17.6.8.0", {"start": v(65.53, 2.8) * mm, "end": v(66.8, 2.8) * mm});
            skLineSegment(sketch, "E17.9.8.0", {"start": v(65.53, 2.03) * mm, "end": v(66.8, 2.03) * mm});
            skSolve(sketch);
        }
        {
            var Q0;
            Q0 = qSketchRegion(id + "F10", true);
            extrude(context, id + "F11", {"entities" : qUnion([Q0]), "operationType" : NewBodyOperationType.REMOVE, "oppositeDirection" : true, "depth" : 12.7 * mm, "offsetDistance" : 25.4 * mm});
        }
        {
            var Q0;
            Q0=makeQuery(id+"F1.opExtrude","SWEPT_FACE",FACE,{"disambiguationData":[OSD([sQuery(id+"F0.wireOp",EDGE,"E0.top")])]});
            var sketch = newSketch(context, id + "F12", { "sketchPlane" : qUnion([Q0])});
            skLineSegment(sketch, "E18.bottom", {"start": v(-15.88, 31.24) * mm, "end": v(-14.6, 31.24) * mm});
            skLineSegment(sketch, "E18.top", {"start": v(-15.88, 30.48) * mm, "end": v(-14.6, 30.48) * mm});
            skLineSegment(sketch, "E18.left", {"start": v(-15.88, 31.24) * mm, "end": v(-15.88, 30.48) * mm});
            skLineSegment(sketch, "E18.right", {"start": v(-14.6, 31.24) * mm, "end": v(-14.6, 30.48) * mm});
            skLineSegment(sketch, "E19.1.0.0", {"start": v(-18.44, 30.48) * mm, "end": v(-17.17, 30.48) * mm});
            skLineSegment(sketch, "E19.1.0.1", {"start": v(-18.44, 31.24) * mm, "end": v(-17.17, 31.24) * mm});
            skLineSegment(sketch, "E19.1.0.2", {"start": v(-17.17, 31.24) * mm, "end": v(-17.17, 30.48) * mm});
            skLineSegment(sketch, "E19.1.0.3", {"start": v(-18.44, 31.24) * mm, "end": v(-18.44, 30.48) * mm});
            skLineSegment(sketch, "E19.2.0.0", {"start": v(-21, 30.48) * mm, "end": v(-19.74, 30.48) * mm});
            skLineSegment(sketch, "E19.2.0.1", {"start": v(-21, 31.24) * mm, "end": v(-19.74, 31.24) * mm});
            skLineSegment(sketch, "E19.2.0.2", {"start": v(-19.74, 31.24) * mm, "end": v(-19.74, 30.48) * mm});
            skLineSegment(sketch, "E19.2.0.3", {"start": v(-21, 31.24) * mm, "end": v(-21, 30.48) * mm});
            skLineSegment(sketch, "E19.3.0.0", {"start": v(-23.57, 30.48) * mm, "end": v(-22.3, 30.48) * mm});
            skLineSegment(sketch, "E19.3.0.1", {"start": v(-23.57, 31.24) * mm, "end": v(-22.3, 31.24) * mm});
            skLineSegment(sketch, "E19.3.0.2", {"start": v(-22.3, 31.24) * mm, "end": v(-22.3, 30.48) * mm});
            skLineSegment(sketch, "E19.3.0.3", {"start": v(-23.57, 31.24) * mm, "end": v(-23.57, 30.48) * mm});
            skLineSegment(sketch, "E19.4.0.0", {"start": v(-26.14, 30.48) * mm, "end": v(-24.87, 30.48) * mm});
            skLineSegment(sketch, "E19.4.0.1", {"start": v(-26.14, 31.24) * mm, "end": v(-24.87, 31.24) * mm});
            skLineSegment(sketch, "E19.4.0.2", {"start": v(-24.87, 31.24) * mm, "end": v(-24.87, 30.48) * mm});
            skLineSegment(sketch, "E19.4.0.3", {"start": v(-26.14, 31.24) * mm, "end": v(-26.14, 30.48) * mm});
            skLineSegment(sketch, "E19.5.0.0", {"start": v(-28.7, 30.48) * mm, "end": v(-27.43, 30.48) * mm});
            skLineSegment(sketch, "E19.5.0.1", {"start": v(-28.7, 31.24) * mm, "end": v(-27.43, 31.24) * mm});
            skLineSegment(sketch, "E19.5.0.2", {"start": v(-27.43, 31.24) * mm, "end": v(-27.43, 30.48) * mm});
            skLineSegment(sketch, "E19.5.0.3", {"start": v(-28.7, 31.24) * mm, "end": v(-28.7, 30.48) * mm});
            skLineSegment(sketch, "E19.6.0.0", {"start": v(-31.27, 30.48) * mm, "end": v(-30, 30.48) * mm});
            skLineSegment(sketch, "E19.6.0.1", {"start": v(-31.27, 31.24) * mm, "end": v(-30, 31.24) * mm});
            skLineSegment(sketch, "E19.6.0.2", {"start": v(-30, 31.24) * mm, "end": v(-30, 30.48) * mm});
            skLineSegment(sketch, "E19.6.0.3", {"start": v(-31.27, 31.24) * mm, "end": v(-31.27, 30.48) * mm});
            skLineSegment(sketch, "E19.7.0.0", {"start": v(-33.83, 30.48) * mm, "end": v(-32.56, 30.48) * mm});
            skLineSegment(sketch, "E19.7.0.1", {"start": v(-33.83, 31.24) * mm, "end": v(-32.56, 31.24) * mm});
            skLineSegment(sketch, "E19.7.0.2", {"start": v(-32.56, 31.24) * mm, "end": v(-32.56, 30.48) * mm});
            skLineSegment(sketch, "E19.7.0.3", {"start": v(-33.83, 31.24) * mm, "end": v(-33.83, 30.48) * mm});
            skLineSegment(sketch, "E19.8.0.0", {"start": v(-36.4, 30.48) * mm, "end": v(-35.13, 30.48) * mm});
            skLineSegment(sketch, "E19.8.0.1", {"start": v(-36.4, 31.24) * mm, "end": v(-35.13, 31.24) * mm});
            skLineSegment(sketch, "E19.8.0.2", {"start": v(-35.13, 31.24) * mm, "end": v(-35.13, 30.48) * mm});
            skLineSegment(sketch, "E19.8.0.3", {"start": v(-36.4, 31.24) * mm, "end": v(-36.4, 30.48) * mm});
            skLineSegment(sketch, "E19.9.0.0", {"start": v(-38.96, 30.48) * mm, "end": v(-37.7, 30.48) * mm});
            skLineSegment(sketch, "E19.9.0.1", {"start": v(-38.96, 31.24) * mm, "end": v(-37.7, 31.24) * mm});
            skLineSegment(sketch, "E19.9.0.2", {"start": v(-37.7, 31.24) * mm, "end": v(-37.7, 30.48) * mm});
            skLineSegment(sketch, "E19.9.0.3", {"start": v(-38.96, 31.24) * mm, "end": v(-38.96, 30.48) * mm});
            skLineSegment(sketch, "E19.10.0.0", {"start": v(-41.53, 30.48) * mm, "end": v(-40.26, 30.48) * mm});
            skLineSegment(sketch, "E19.10.0.1", {"start": v(-41.53, 31.24) * mm, "end": v(-40.26, 31.24) * mm});
            skLineSegment(sketch, "E19.10.0.2", {"start": v(-40.26, 31.24) * mm, "end": v(-40.26, 30.48) * mm});
            skLineSegment(sketch, "E19.10.0.3", {"start": v(-41.53, 31.24) * mm, "end": v(-41.53, 30.48) * mm});
            skLineSegment(sketch, "E19.direction1", {"start": v(-15.88, 30.48) * mm, "end": v(-18.44, 30.48) * mm, "construction": true});
            skLineSegment(sketch, "E20.bottom", {"start": v(-14.6, 32) * mm, "end": v(-15.37, 32) * mm});
            skLineSegment(sketch, "E20.top", {"start": v(-14.6, 34.67) * mm, "end": v(-15.37, 34.67) * mm});
            skLineSegment(sketch, "E20.left", {"start": v(-14.6, 32) * mm, "end": v(-14.6, 34.67) * mm});
            skLineSegment(sketch, "E20.right", {"start": v(-15.37, 32) * mm, "end": v(-15.37, 34.67) * mm});
            skLineSegment(sketch, "E21.0.1.0", {"start": v(-15.37, 35.43) * mm, "end": v(-15.37, 38.1) * mm});
            skLineSegment(sketch, "E21.0.1.1", {"start": v(-14.6, 35.43) * mm, "end": v(-15.37, 35.43) * mm});
            skLineSegment(sketch, "E21.0.1.2", {"start": v(-14.6, 35.43) * mm, "end": v(-14.6, 38.1) * mm});
            skLineSegment(sketch, "E21.0.1.3", {"start": v(-14.6, 38.1) * mm, "end": v(-15.37, 38.1) * mm});
            skLineSegment(sketch, "E21.0.2.0", {"start": v(-15.37, 38.86) * mm, "end": v(-15.37, 41.53) * mm});
            skLineSegment(sketch, "E21.0.2.1", {"start": v(-14.6, 38.86) * mm, "end": v(-15.37, 38.86) * mm});
            skLineSegment(sketch, "E21.0.2.2", {"start": v(-14.6, 38.86) * mm, "end": v(-14.6, 41.53) * mm});
            skLineSegment(sketch, "E21.0.2.3", {"start": v(-14.6, 41.53) * mm, "end": v(-15.37, 41.53) * mm});
            skLineSegment(sketch, "E21.0.3.0", {"start": v(-15.37, 42.3) * mm, "end": v(-15.37, 44.96) * mm});
            skLineSegment(sketch, "E21.0.3.1", {"start": v(-14.6, 42.3) * mm, "end": v(-15.37, 42.3) * mm});
            skLineSegment(sketch, "E21.0.3.2", {"start": v(-14.6, 42.3) * mm, "end": v(-14.6, 44.96) * mm});
            skLineSegment(sketch, "E21.0.3.3", {"start": v(-14.6, 44.96) * mm, "end": v(-15.37, 44.96) * mm});
            skLineSegment(sketch, "E21.direction1", {"start": v(-15.37, 32) * mm, "end": v(-13.63, 32) * mm, "construction": true});
            skLineSegment(sketch, "E21.direction2", {"start": v(-15.37, 32) * mm, "end": v(-15.37, 35.43) * mm, "construction": true});
            skLineSegment(sketch, "E22.bottom", {"start": v(-96.27, 27.94) * mm, "end": v(-97.54, 27.94) * mm});
            skLineSegment(sketch, "E22.top", {"start": v(-96.27, 28.7) * mm, "end": v(-97.54, 28.7) * mm});
            skLineSegment(sketch, "E22.left", {"start": v(-96.27, 27.94) * mm, "end": v(-96.27, 28.7) * mm});
            skLineSegment(sketch, "E22.right", {"start": v(-97.54, 27.94) * mm, "end": v(-97.54, 28.7) * mm});
            skLineSegment(sketch, "E23.1.0.0", {"start": v(-94, 27.94) * mm, "end": v(-94, 28.7) * mm});
            skLineSegment(sketch, "E23.1.0.1", {"start": v(-94, 28.7) * mm, "end": v(-95.28, 28.7) * mm});
            skLineSegment(sketch, "E23.1.0.2", {"start": v(-95.28, 27.94) * mm, "end": v(-95.28, 28.7) * mm});
            skLineSegment(sketch, "E23.1.0.3", {"start": v(-94, 27.94) * mm, "end": v(-95.28, 27.94) * mm});
            skLineSegment(sketch, "E23.2.0.0", {"start": v(-91.74, 27.94) * mm, "end": v(-91.74, 28.7) * mm});
            skLineSegment(sketch, "E23.2.0.1", {"start": v(-91.74, 28.7) * mm, "end": v(-93.01, 28.7) * mm});
            skLineSegment(sketch, "E23.2.0.2", {"start": v(-93.01, 27.94) * mm, "end": v(-93.01, 28.7) * mm});
            skLineSegment(sketch, "E23.2.0.3", {"start": v(-91.74, 27.94) * mm, "end": v(-93.01, 27.94) * mm});
            skLineSegment(sketch, "E23.3.0.0", {"start": v(-89.48, 27.94) * mm, "end": v(-89.48, 28.7) * mm});
            skLineSegment(sketch, "E23.3.0.1", {"start": v(-89.48, 28.7) * mm, "end": v(-90.75, 28.7) * mm});
            skLineSegment(sketch, "E23.3.0.2", {"start": v(-90.75, 27.94) * mm, "end": v(-90.75, 28.7) * mm});
            skLineSegment(sketch, "E23.3.0.3", {"start": v(-89.48, 27.94) * mm, "end": v(-90.75, 27.94) * mm});
            skLineSegment(sketch, "E23.4.0.0", {"start": v(-87.22, 27.94) * mm, "end": v(-87.22, 28.7) * mm});
            skLineSegment(sketch, "E23.4.0.1", {"start": v(-87.22, 28.7) * mm, "end": v(-88.5, 28.7) * mm});
            skLineSegment(sketch, "E23.4.0.2", {"start": v(-88.5, 27.94) * mm, "end": v(-88.5, 28.7) * mm});
            skLineSegment(sketch, "E23.4.0.3", {"start": v(-87.22, 27.94) * mm, "end": v(-88.5, 27.94) * mm});
            skLineSegment(sketch, "E23.5.0.0", {"start": v(-84.96, 27.94) * mm, "end": v(-84.96, 28.7) * mm});
            skLineSegment(sketch, "E23.5.0.1", {"start": v(-84.96, 28.7) * mm, "end": v(-86.23, 28.7) * mm});
            skLineSegment(sketch, "E23.5.0.2", {"start": v(-86.23, 27.94) * mm, "end": v(-86.23, 28.7) * mm});
            skLineSegment(sketch, "E23.5.0.3", {"start": v(-84.96, 27.94) * mm, "end": v(-86.23, 27.94) * mm});
            skLineSegment(sketch, "E23.6.0.0", {"start": v(-82.7, 27.94) * mm, "end": v(-82.7, 28.7) * mm});
            skLineSegment(sketch, "E23.6.0.1", {"start": v(-82.7, 28.7) * mm, "end": v(-83.97, 28.7) * mm});
            skLineSegment(sketch, "E23.6.0.2", {"start": v(-83.97, 27.94) * mm, "end": v(-83.97, 28.7) * mm});
            skLineSegment(sketch, "E23.6.0.3", {"start": v(-82.7, 27.94) * mm, "end": v(-83.97, 27.94) * mm});
            skLineSegment(sketch, "E23.7.0.0", {"start": v(-80.44, 27.94) * mm, "end": v(-80.44, 28.7) * mm});
            skLineSegment(sketch, "E23.7.0.1", {"start": v(-80.44, 28.7) * mm, "end": v(-81.71, 28.7) * mm});
            skLineSegment(sketch, "E23.7.0.2", {"start": v(-81.71, 27.94) * mm, "end": v(-81.71, 28.7) * mm});
            skLineSegment(sketch, "E23.7.0.3", {"start": v(-80.44, 27.94) * mm, "end": v(-81.71, 27.94) * mm});
            skLineSegment(sketch, "E23.8.0.0", {"start": v(-78.18, 27.94) * mm, "end": v(-78.18, 28.7) * mm});
            skLineSegment(sketch, "E23.8.0.1", {"start": v(-78.18, 28.7) * mm, "end": v(-79.45, 28.7) * mm});
            skLineSegment(sketch, "E23.8.0.2", {"start": v(-79.45, 27.94) * mm, "end": v(-79.45, 28.7) * mm});
            skLineSegment(sketch, "E23.8.0.3", {"start": v(-78.18, 27.94) * mm, "end": v(-79.45, 27.94) * mm});
            skLineSegment(sketch, "E23.9.0.0", {"start": v(-75.92, 27.94) * mm, "end": v(-75.92, 28.7) * mm});
            skLineSegment(sketch, "E23.9.0.1", {"start": v(-75.92, 28.7) * mm, "end": v(-77.2, 28.7) * mm});
            skLineSegment(sketch, "E23.9.0.2", {"start": v(-77.2, 27.94) * mm, "end": v(-77.2, 28.7) * mm});
            skLineSegment(sketch, "E23.9.0.3", {"start": v(-75.92, 27.94) * mm, "end": v(-77.2, 27.94) * mm});
            skLineSegment(sketch, "E23.direction1", {"start": v(-97.54, 27.94) * mm, "end": v(-95.28, 27.94) * mm, "construction": true});
            skLineSegment(sketch, "E24.bottom", {"start": v(-97.54, 29.46) * mm, "end": v(-96.77, 29.46) * mm});
            skLineSegment(sketch, "E24.top", {"start": v(-97.54, 32) * mm, "end": v(-96.77, 32) * mm});
            skLineSegment(sketch, "E24.left", {"start": v(-97.54, 29.46) * mm, "end": v(-97.54, 32) * mm});
            skLineSegment(sketch, "E24.right", {"start": v(-96.77, 29.46) * mm, "end": v(-96.77, 32) * mm});
            skLineSegment(sketch, "E25.0.1.0", {"start": v(-97.54, 35.28) * mm, "end": v(-96.77, 35.28) * mm});
            skLineSegment(sketch, "E25.0.1.1", {"start": v(-97.54, 32.74) * mm, "end": v(-96.77, 32.74) * mm});
            skLineSegment(sketch, "E25.0.1.2", {"start": v(-96.77, 32.74) * mm, "end": v(-96.77, 35.28) * mm});
            skLineSegment(sketch, "E25.0.1.3", {"start": v(-97.54, 32.74) * mm, "end": v(-97.54, 35.28) * mm});
            skLineSegment(sketch, "E25.0.2.0", {"start": v(-97.54, 38.56) * mm, "end": v(-96.77, 38.56) * mm});
            skLineSegment(sketch, "E25.0.2.1", {"start": v(-97.54, 36.02) * mm, "end": v(-96.77, 36.02) * mm});
            skLineSegment(sketch, "E25.0.2.2", {"start": v(-96.77, 36.02) * mm, "end": v(-96.77, 38.56) * mm});
            skLineSegment(sketch, "E25.0.2.3", {"start": v(-97.54, 36.02) * mm, "end": v(-97.54, 38.56) * mm});
            skLineSegment(sketch, "E25.0.3.0", {"start": v(-97.54, 41.83) * mm, "end": v(-96.77, 41.83) * mm});
            skLineSegment(sketch, "E25.0.3.1", {"start": v(-97.54, 39.3) * mm, "end": v(-96.77, 39.3) * mm});
            skLineSegment(sketch, "E25.0.3.2", {"start": v(-96.77, 39.3) * mm, "end": v(-96.77, 41.83) * mm});
            skLineSegment(sketch, "E25.0.3.3", {"start": v(-97.54, 39.3) * mm, "end": v(-97.54, 41.83) * mm});
            skLineSegment(sketch, "E25.0.4.0", {"start": v(-97.54, 45.11) * mm, "end": v(-96.77, 45.11) * mm});
            skLineSegment(sketch, "E25.0.4.1", {"start": v(-97.54, 42.57) * mm, "end": v(-96.77, 42.57) * mm});
            skLineSegment(sketch, "E25.0.4.2", {"start": v(-96.77, 42.57) * mm, "end": v(-96.77, 45.11) * mm});
            skLineSegment(sketch, "E25.0.4.3", {"start": v(-97.54, 42.57) * mm, "end": v(-97.54, 45.11) * mm});
            skLineSegment(sketch, "E25.1.0.0", {"start": v(-76.68, 32) * mm, "end": v(-75.92, 32) * mm});
            skLineSegment(sketch, "E25.1.0.1", {"start": v(-76.68, 29.46) * mm, "end": v(-75.92, 29.46) * mm});
            skLineSegment(sketch, "E25.1.0.2", {"start": v(-75.92, 29.46) * mm, "end": v(-75.92, 32) * mm});
            skLineSegment(sketch, "E25.1.0.3", {"start": v(-76.68, 29.46) * mm, "end": v(-76.68, 32) * mm});
            skLineSegment(sketch, "E25.1.1.0", {"start": v(-76.68, 35.28) * mm, "end": v(-75.92, 35.28) * mm});
            skLineSegment(sketch, "E25.1.1.1", {"start": v(-76.68, 32.74) * mm, "end": v(-75.92, 32.74) * mm});
            skLineSegment(sketch, "E25.1.1.2", {"start": v(-75.92, 32.74) * mm, "end": v(-75.92, 35.28) * mm});
            skLineSegment(sketch, "E25.1.1.3", {"start": v(-76.68, 32.74) * mm, "end": v(-76.68, 35.28) * mm});
            skLineSegment(sketch, "E25.1.2.0", {"start": v(-76.68, 38.56) * mm, "end": v(-75.92, 38.56) * mm});
            skLineSegment(sketch, "E25.1.2.1", {"start": v(-76.68, 36.02) * mm, "end": v(-75.92, 36.02) * mm});
            skLineSegment(sketch, "E25.1.2.2", {"start": v(-75.92, 36.02) * mm, "end": v(-75.92, 38.56) * mm});
            skLineSegment(sketch, "E25.1.2.3", {"start": v(-76.68, 36.02) * mm, "end": v(-76.68, 38.56) * mm});
            skLineSegment(sketch, "E25.1.3.0", {"start": v(-76.68, 41.83) * mm, "end": v(-75.92, 41.83) * mm});
            skLineSegment(sketch, "E25.1.3.1", {"start": v(-76.68, 39.3) * mm, "end": v(-75.92, 39.3) * mm});
            skLineSegment(sketch, "E25.1.3.2", {"start": v(-75.92, 39.3) * mm, "end": v(-75.92, 41.83) * mm});
            skLineSegment(sketch, "E25.1.3.3", {"start": v(-76.68, 39.3) * mm, "end": v(-76.68, 41.83) * mm});
            skLineSegment(sketch, "E25.1.4.0", {"start": v(-76.68, 45.11) * mm, "end": v(-75.92, 45.11) * mm});
            skLineSegment(sketch, "E25.1.4.1", {"start": v(-76.68, 42.57) * mm, "end": v(-75.92, 42.57) * mm});
            skLineSegment(sketch, "E25.1.4.2", {"start": v(-75.92, 42.57) * mm, "end": v(-75.92, 45.11) * mm});
            skLineSegment(sketch, "E25.1.4.3", {"start": v(-76.68, 42.57) * mm, "end": v(-76.68, 45.11) * mm});
            skLineSegment(sketch, "E25.direction1", {"start": v(-97.54, 29.46) * mm, "end": v(-76.68, 29.46) * mm, "construction": true});
            skLineSegment(sketch, "E25.direction2", {"start": v(-97.54, 29.46) * mm, "end": v(-97.54, 32.74) * mm, "construction": true});
            skLineSegment(sketch, "E26.bottom", {"start": v(-68.58, 2.03) * mm, "end": v(-67.82, 2.03) * mm});
            skLineSegment(sketch, "E26.top", {"start": v(-68.58, 4.65) * mm, "end": v(-67.82, 4.65) * mm});
            skLineSegment(sketch, "E26.left", {"start": v(-68.58, 2.03) * mm, "end": v(-68.58, 4.65) * mm});
            skLineSegment(sketch, "E26.right", {"start": v(-67.82, 2.03) * mm, "end": v(-67.82, 4.65) * mm});
            skLineSegment(sketch, "E27.0.1.0", {"start": v(-68.58, 5.41) * mm, "end": v(-67.82, 5.41) * mm});
            skLineSegment(sketch, "E27.0.1.1", {"start": v(-67.82, 5.41) * mm, "end": v(-67.82, 8.03) * mm});
            skLineSegment(sketch, "E27.0.1.2", {"start": v(-68.58, 5.41) * mm, "end": v(-68.58, 8.03) * mm});
            skLineSegment(sketch, "E27.0.1.3", {"start": v(-68.58, 8.03) * mm, "end": v(-67.82, 8.03) * mm});
            skLineSegment(sketch, "E27.0.2.0", {"start": v(-68.58, 8.79) * mm, "end": v(-67.82, 8.79) * mm});
            skLineSegment(sketch, "E27.0.2.1", {"start": v(-67.82, 8.79) * mm, "end": v(-67.82, 11.4) * mm});
            skLineSegment(sketch, "E27.0.2.2", {"start": v(-68.58, 8.79) * mm, "end": v(-68.58, 11.4) * mm});
            skLineSegment(sketch, "E27.0.2.3", {"start": v(-68.58, 11.4) * mm, "end": v(-67.82, 11.4) * mm});
            skLineSegment(sketch, "E27.0.3.0", {"start": v(-68.58, 12.17) * mm, "end": v(-67.82, 12.17) * mm});
            skLineSegment(sketch, "E27.0.3.1", {"start": v(-67.82, 12.17) * mm, "end": v(-67.82, 14.78) * mm});
            skLineSegment(sketch, "E27.0.3.2", {"start": v(-68.58, 12.17) * mm, "end": v(-68.58, 14.78) * mm});
            skLineSegment(sketch, "E27.0.3.3", {"start": v(-68.58, 14.78) * mm, "end": v(-67.82, 14.78) * mm});
            skLineSegment(sketch, "E27.0.4.0", {"start": v(-68.58, 15.54) * mm, "end": v(-67.82, 15.54) * mm});
            skLineSegment(sketch, "E27.0.4.1", {"start": v(-67.82, 15.54) * mm, "end": v(-67.82, 18.16) * mm});
            skLineSegment(sketch, "E27.0.4.2", {"start": v(-68.58, 15.54) * mm, "end": v(-68.58, 18.16) * mm});
            skLineSegment(sketch, "E27.0.4.3", {"start": v(-68.58, 18.16) * mm, "end": v(-67.82, 18.16) * mm});
            skLineSegment(sketch, "E27.0.5.0", {"start": v(-68.58, 18.92) * mm, "end": v(-67.82, 18.92) * mm});
            skLineSegment(sketch, "E27.0.5.1", {"start": v(-67.82, 18.92) * mm, "end": v(-67.82, 21.54) * mm});
            skLineSegment(sketch, "E27.0.5.2", {"start": v(-68.58, 18.92) * mm, "end": v(-68.58, 21.54) * mm});
            skLineSegment(sketch, "E27.0.5.3", {"start": v(-68.58, 21.54) * mm, "end": v(-67.82, 21.54) * mm});
            skLineSegment(sketch, "E27.0.6.0", {"start": v(-68.58, 22.3) * mm, "end": v(-67.82, 22.3) * mm});
            skLineSegment(sketch, "E27.0.6.1", {"start": v(-67.82, 22.3) * mm, "end": v(-67.82, 24.92) * mm});
            skLineSegment(sketch, "E27.0.6.2", {"start": v(-68.58, 22.3) * mm, "end": v(-68.58, 24.92) * mm});
            skLineSegment(sketch, "E27.0.6.3", {"start": v(-68.58, 24.92) * mm, "end": v(-67.82, 24.92) * mm});
            skLineSegment(sketch, "E27.0.7.0", {"start": v(-68.58, 25.68) * mm, "end": v(-67.82, 25.68) * mm});
            skLineSegment(sketch, "E27.0.7.1", {"start": v(-67.82, 25.68) * mm, "end": v(-67.82, 28.3) * mm});
            skLineSegment(sketch, "E27.0.7.2", {"start": v(-68.58, 25.68) * mm, "end": v(-68.58, 28.3) * mm});
            skLineSegment(sketch, "E27.0.7.3", {"start": v(-68.58, 28.3) * mm, "end": v(-67.82, 28.3) * mm});
            skLineSegment(sketch, "E27.0.8.0", {"start": v(-68.58, 29.06) * mm, "end": v(-67.82, 29.06) * mm});
            skLineSegment(sketch, "E27.0.8.1", {"start": v(-67.82, 29.06) * mm, "end": v(-67.82, 31.67) * mm});
            skLineSegment(sketch, "E27.0.8.2", {"start": v(-68.58, 29.06) * mm, "end": v(-68.58, 31.67) * mm});
            skLineSegment(sketch, "E27.0.8.3", {"start": v(-68.58, 31.67) * mm, "end": v(-67.82, 31.67) * mm});
            skLineSegment(sketch, "E27.0.9.0", {"start": v(-68.58, 32.44) * mm, "end": v(-67.82, 32.44) * mm});
            skLineSegment(sketch, "E27.0.9.1", {"start": v(-67.82, 32.44) * mm, "end": v(-67.82, 35.05) * mm});
            skLineSegment(sketch, "E27.0.9.2", {"start": v(-68.58, 32.44) * mm, "end": v(-68.58, 35.05) * mm});
            skLineSegment(sketch, "E27.0.9.3", {"start": v(-68.58, 35.05) * mm, "end": v(-67.82, 35.05) * mm});
            skLineSegment(sketch, "E27.0.10.0", {"start": v(-68.58, 35.81) * mm, "end": v(-67.82, 35.81) * mm});
            skLineSegment(sketch, "E27.0.10.1", {"start": v(-67.82, 35.81) * mm, "end": v(-67.82, 38.43) * mm});
            skLineSegment(sketch, "E27.0.10.2", {"start": v(-68.58, 35.81) * mm, "end": v(-68.58, 38.43) * mm});
            skLineSegment(sketch, "E27.0.10.3", {"start": v(-68.58, 38.43) * mm, "end": v(-67.82, 38.43) * mm});
            skLineSegment(sketch, "E27.0.11.0", {"start": v(-68.58, 39.2) * mm, "end": v(-67.82, 39.2) * mm});
            skLineSegment(sketch, "E27.0.11.1", {"start": v(-67.82, 39.2) * mm, "end": v(-67.82, 41.8) * mm});
            skLineSegment(sketch, "E27.0.11.2", {"start": v(-68.58, 39.2) * mm, "end": v(-68.58, 41.8) * mm});
            skLineSegment(sketch, "E27.0.11.3", {"start": v(-68.58, 41.8) * mm, "end": v(-67.82, 41.8) * mm});
            skLineSegment(sketch, "E27.0.12.0", {"start": v(-68.58, 42.57) * mm, "end": v(-67.82, 42.57) * mm});
            skLineSegment(sketch, "E27.0.12.1", {"start": v(-67.82, 42.57) * mm, "end": v(-67.82, 45.19) * mm});
            skLineSegment(sketch, "E27.0.12.2", {"start": v(-68.58, 42.57) * mm, "end": v(-68.58, 45.19) * mm});
            skLineSegment(sketch, "E27.0.12.3", {"start": v(-68.58, 45.19) * mm, "end": v(-67.82, 45.19) * mm});
            skLineSegment(sketch, "E27.1.0.0", {"start": v(-43.18, 2.03) * mm, "end": v(-42.42, 2.03) * mm});
            skLineSegment(sketch, "E27.1.0.1", {"start": v(-42.42, 2.03) * mm, "end": v(-42.42, 4.65) * mm});
            skLineSegment(sketch, "E27.1.0.2", {"start": v(-43.18, 2.03) * mm, "end": v(-43.18, 4.65) * mm});
            skLineSegment(sketch, "E27.1.0.3", {"start": v(-43.18, 4.65) * mm, "end": v(-42.42, 4.65) * mm});
            skLineSegment(sketch, "E27.1.1.0", {"start": v(-43.18, 5.41) * mm, "end": v(-42.42, 5.41) * mm});
            skLineSegment(sketch, "E27.1.1.1", {"start": v(-42.42, 5.41) * mm, "end": v(-42.42, 8.03) * mm});
            skLineSegment(sketch, "E27.1.1.2", {"start": v(-43.18, 5.41) * mm, "end": v(-43.18, 8.03) * mm});
            skLineSegment(sketch, "E27.1.1.3", {"start": v(-43.18, 8.03) * mm, "end": v(-42.42, 8.03) * mm});
            skLineSegment(sketch, "E27.1.2.0", {"start": v(-43.18, 8.79) * mm, "end": v(-42.42, 8.79) * mm});
            skLineSegment(sketch, "E27.1.2.1", {"start": v(-42.42, 8.79) * mm, "end": v(-42.42, 11.4) * mm});
            skLineSegment(sketch, "E27.1.2.2", {"start": v(-43.18, 8.79) * mm, "end": v(-43.18, 11.4) * mm});
            skLineSegment(sketch, "E27.1.2.3", {"start": v(-43.18, 11.4) * mm, "end": v(-42.42, 11.4) * mm});
            skLineSegment(sketch, "E27.1.3.0", {"start": v(-43.18, 12.17) * mm, "end": v(-42.42, 12.17) * mm});
            skLineSegment(sketch, "E27.1.3.1", {"start": v(-42.42, 12.17) * mm, "end": v(-42.42, 14.78) * mm});
            skLineSegment(sketch, "E27.1.3.2", {"start": v(-43.18, 12.17) * mm, "end": v(-43.18, 14.78) * mm});
            skLineSegment(sketch, "E27.1.3.3", {"start": v(-43.18, 14.78) * mm, "end": v(-42.42, 14.78) * mm});
            skLineSegment(sketch, "E27.1.4.0", {"start": v(-43.18, 15.54) * mm, "end": v(-42.42, 15.54) * mm});
            skLineSegment(sketch, "E27.1.4.1", {"start": v(-42.42, 15.54) * mm, "end": v(-42.42, 18.16) * mm});
            skLineSegment(sketch, "E27.1.4.2", {"start": v(-43.18, 15.54) * mm, "end": v(-43.18, 18.16) * mm});
            skLineSegment(sketch, "E27.1.4.3", {"start": v(-43.18, 18.16) * mm, "end": v(-42.42, 18.16) * mm});
            skLineSegment(sketch, "E27.1.5.0", {"start": v(-43.18, 18.92) * mm, "end": v(-42.42, 18.92) * mm});
            skLineSegment(sketch, "E27.1.5.1", {"start": v(-42.42, 18.92) * mm, "end": v(-42.42, 21.54) * mm});
            skLineSegment(sketch, "E27.1.5.2", {"start": v(-43.18, 18.92) * mm, "end": v(-43.18, 21.54) * mm});
            skLineSegment(sketch, "E27.1.5.3", {"start": v(-43.18, 21.54) * mm, "end": v(-42.42, 21.54) * mm});
            skLineSegment(sketch, "E27.1.6.0", {"start": v(-43.18, 22.3) * mm, "end": v(-42.42, 22.3) * mm});
            skLineSegment(sketch, "E27.1.6.1", {"start": v(-42.42, 22.3) * mm, "end": v(-42.42, 24.92) * mm});
            skLineSegment(sketch, "E27.1.6.2", {"start": v(-43.18, 22.3) * mm, "end": v(-43.18, 24.92) * mm});
            skLineSegment(sketch, "E27.1.6.3", {"start": v(-43.18, 24.92) * mm, "end": v(-42.42, 24.92) * mm});
            skLineSegment(sketch, "E27.1.7.0", {"start": v(-43.18, 25.68) * mm, "end": v(-42.42, 25.68) * mm});
            skLineSegment(sketch, "E27.1.7.1", {"start": v(-42.42, 25.68) * mm, "end": v(-42.42, 28.3) * mm});
            skLineSegment(sketch, "E27.1.7.2", {"start": v(-43.18, 25.68) * mm, "end": v(-43.18, 28.3) * mm});
            skLineSegment(sketch, "E27.1.7.3", {"start": v(-43.18, 28.3) * mm, "end": v(-42.42, 28.3) * mm});
            skLineSegment(sketch, "E27.1.8.0", {"start": v(-43.18, 29.06) * mm, "end": v(-42.42, 29.06) * mm});
            skLineSegment(sketch, "E27.1.8.1", {"start": v(-42.42, 29.06) * mm, "end": v(-42.42, 31.67) * mm});
            skLineSegment(sketch, "E27.1.8.2", {"start": v(-43.18, 29.06) * mm, "end": v(-43.18, 31.67) * mm});
            skLineSegment(sketch, "E27.1.8.3", {"start": v(-43.18, 31.67) * mm, "end": v(-42.42, 31.67) * mm});
            skLineSegment(sketch, "E27.1.9.0", {"start": v(-43.18, 32.44) * mm, "end": v(-42.42, 32.44) * mm});
            skLineSegment(sketch, "E27.1.9.1", {"start": v(-42.42, 32.44) * mm, "end": v(-42.42, 35.05) * mm});
            skLineSegment(sketch, "E27.1.9.2", {"start": v(-43.18, 32.44) * mm, "end": v(-43.18, 35.05) * mm});
            skLineSegment(sketch, "E27.1.9.3", {"start": v(-43.18, 35.05) * mm, "end": v(-42.42, 35.05) * mm});
            skLineSegment(sketch, "E27.1.10.0", {"start": v(-43.18, 35.81) * mm, "end": v(-42.42, 35.81) * mm});
            skLineSegment(sketch, "E27.1.10.1", {"start": v(-42.42, 35.81) * mm, "end": v(-42.42, 38.43) * mm});
            skLineSegment(sketch, "E27.1.10.2", {"start": v(-43.18, 35.81) * mm, "end": v(-43.18, 38.43) * mm});
            skLineSegment(sketch, "E27.1.10.3", {"start": v(-43.18, 38.43) * mm, "end": v(-42.42, 38.43) * mm});
            skLineSegment(sketch, "E27.1.11.0", {"start": v(-43.18, 39.2) * mm, "end": v(-42.42, 39.2) * mm});
            skLineSegment(sketch, "E27.1.11.1", {"start": v(-42.42, 39.2) * mm, "end": v(-42.42, 41.8) * mm});
            skLineSegment(sketch, "E27.1.11.2", {"start": v(-43.18, 39.2) * mm, "end": v(-43.18, 41.8) * mm});
            skLineSegment(sketch, "E27.1.11.3", {"start": v(-43.18, 41.8) * mm, "end": v(-42.42, 41.8) * mm});
            skLineSegment(sketch, "E27.1.12.0", {"start": v(-43.18, 42.57) * mm, "end": v(-42.42, 42.57) * mm});
            skLineSegment(sketch, "E27.1.12.1", {"start": v(-42.42, 42.57) * mm, "end": v(-42.42, 45.19) * mm});
            skLineSegment(sketch, "E27.1.12.2", {"start": v(-43.18, 42.57) * mm, "end": v(-43.18, 45.19) * mm});
            skLineSegment(sketch, "E27.1.12.3", {"start": v(-43.18, 45.19) * mm, "end": v(-42.42, 45.19) * mm});
            skLineSegment(sketch, "E27.direction1", {"start": v(-68.58, 2.03) * mm, "end": v(-43.18, 2.03) * mm, "construction": true});
            skLineSegment(sketch, "E27.direction2", {"start": v(-68.58, 2.03) * mm, "end": v(-68.58, 5.41) * mm, "construction": true});
            skSolve(sketch);
        }
        {
            var Q0;
            Q0 = qSketchRegion(id + "F12", true);
            extrude(context, id + "F13", {"entities" : qUnion([Q0]), "operationType" : NewBodyOperationType.REMOVE, "oppositeDirection" : true, "depth" : 11.56 * mm, "offsetDistance" : 25.4 * mm});
        }
        {
            var Q0;
            Q0=makeQuery(id+"F1.opExtrude","SWEPT_EDGE",EDGE,{"disambiguationData":[OSD([sQuery(id+"F0.wireOp",EDGE,"E0.bottom"),sQuery(id+"F0.wireOp",EDGE,"E0.left")])]});
            var Q1;
            Q1=makeQuery(id+"F1.opExtrude","SWEPT_EDGE",EDGE,{"disambiguationData":[OSD([sQuery(id+"F0.wireOp",EDGE,"E0.bottom"),sQuery(id+"F0.wireOp",EDGE,"E0.right")])]});
            var Q2;
            Q2=makeQuery(id+"F1.opExtrude","SWEPT_EDGE",EDGE,{"disambiguationData":[OSD([sQuery(id+"F0.wireOp",EDGE,"E0.top"),sQuery(id+"F0.wireOp",EDGE,"E0.right")])]});
            var Q3;
            Q3=makeQuery(id+"F1.opExtrude","SWEPT_EDGE",EDGE,{"disambiguationData":[OSD([sQuery(id+"F0.wireOp",EDGE,"E0.top"),sQuery(id+"F0.wireOp",EDGE,"E0.left")])]});
            fillet(context, id + "F14", {"entities" : qUnion([Q0, Q1, Q2, Q3]), "tangentPropagation" : true, "radius" : 1.27 * mm, "defaultsChanged" : false, "vertexSettings" : [], "allowEdgeOverflow" : false});
        }
        {
            var Q0;
            Q0=makeQuery(id+"F6.boolean.opBoolean","COPY",EDGE,{"derivedFrom":makeQuery(id+"F6.opExtrude","SWEPT_EDGE",EDGE,{"disambiguationData":[OSD([sQuery(id+"F5.wireOp",EDGE,"E12.1"),sQuery(id+"F5.wireOp",EDGE,"E12.2")])]})});
            var Q1;
            Q1=makeQuery(id+"F6.boolean.opBoolean","COPY",EDGE,{"derivedFrom":makeQuery(id+"F6.opExtrude","SWEPT_EDGE",EDGE,{"disambiguationData":[OSD([sQuery(id+"F5.wireOp",EDGE,"E12.2"),sQuery(id+"F5.wireOp",EDGE,"E12.3")])]})});
            var Q2;
            Q2=makeQuery(id+"F6.boolean.opBoolean","COPY",EDGE,{"derivedFrom":makeQuery(id+"F6.opExtrude","SWEPT_EDGE",EDGE,{"disambiguationData":[OSD([sQuery(id+"F5.wireOp",EDGE,"E12.0"),sQuery(id+"F5.wireOp",EDGE,"E12.1")])]})});
            var Q3;
            Q3=makeQuery(id+"F6.boolean.opBoolean","COPY",EDGE,{"derivedFrom":makeQuery(id+"F6.opExtrude","SWEPT_EDGE",EDGE,{"disambiguationData":[OSD([sQuery(id+"F5.wireOp",EDGE,"E12.0"),sQuery(id+"F5.wireOp",EDGE,"E12.3")])]})});
            fillet(context, id + "F15", {"entities" : qUnion([Q0, Q1, Q2, Q3]), "tangentPropagation" : true, "radius" : 0.38 * mm, "defaultsChanged" : true, "vertexSettings" : [], "allowEdgeOverflow" : false});
        }
        {
            var Q0;
            Q0=makeQuery(id+"F2.opShell","OFFSET_EDGE",EDGE,{"disambiguationData":[OSD([sQuery(id+"F0.wireOp",EDGE,"E0.top"),sQuery(id+"F0.wireOp",EDGE,"E0.left")])]});
            var Q1;
            Q1=makeQuery(id+"F8.opChamfer","BLEND_EDGE",EDGE,{"blendedFrom":[makeQuery(id+"F4.opExtrude","CAP_EDGE",EDGE,{"disambiguationData":[OSD([sQuery(id+"F3.wireOp",EDGE,"E10")])],"isStart":false}),makeQuery(id+"F2.opShell","OFFSET_FACE",FACE,{"disambiguationData":[OSD([sQuery(id+"F0.wireOp",EDGE,"E0.top")])]})],"blendedInto":[makeQuery(id+"F2.opShell","OFFSET_FACE",FACE,{"disambiguationData":[OSD([sQuery(id+"F0.wireOp",EDGE,"E0.top")])]})]});
            var Q2;
            Q2=makeQuery(id+"F8.opChamfer","BLEND_EDGE",EDGE,{"blendedFrom":[makeQuery(id+"F4.opExtrude","CAP_EDGE",EDGE,{"disambiguationData":[OSD([sQuery(id+"F3.wireOp",EDGE,"E11")])],"isStart":false}),makeQuery(id+"F2.opShell","OFFSET_FACE",FACE,{"disambiguationData":[OSD([sQuery(id+"F0.wireOp",EDGE,"E0.left")])]})],"blendedInto":[makeQuery(id+"F2.opShell","OFFSET_FACE",FACE,{"disambiguationData":[OSD([sQuery(id+"F0.wireOp",EDGE,"E0.left")])]})]});
            var Q3;
            {var subQ0=sQuery(id+"F0.wireOp",EDGE,"E0.left");Q3=makeQuery(id+"F2.opShell","OFFSET_EDGE",EDGE,{"disambiguationData":[OSD([subQ0]),TDD([makeQuery(id+"F1.opExtrude","CAP_EDGE",EDGE,{"disambiguationData":[OSD([subQ0])],"isStart":true})])]});}
            var Q4;
            {var subQ0=sQuery(id+"F0.wireOp",EDGE,"E0.left");var subQ1=sQuery(id+"F0.wireOp",EDGE,"E0.top");Q4=makeQuery(id+"F11.boolean.opBoolean","SPLIT",EDGE,{"disambiguationData":[TD([makeQuery(id+"F2.opShell","OFFSET_FACE",FACE,{"disambiguationData":[OSD([subQ0])]})])],"derivedFrom":makeQuery(id+"F2.opShell","OFFSET_EDGE",EDGE,{"disambiguationData":[OSD([subQ1]),TDD([makeQuery(id+"F1.opExtrude","CAP_EDGE",EDGE,{"disambiguationData":[OSD([subQ1])],"isStart":true})])]})});}
            var Q5;
            Q5=makeQuery(id+"F2.opShell","OFFSET_EDGE",EDGE,{"disambiguationData":[OSD([sQuery(id+"F0.wireOp",EDGE,"E0.bottom"),sQuery(id+"F0.wireOp",EDGE,"E0.left")])]});
            var Q6;
            {var subQ0=sQuery(id+"F0.wireOp",EDGE,"E0.left");var subQ1=sQuery(id+"F0.wireOp",EDGE,"E0.bottom");Q6=makeQuery(id+"F11.boolean.opBoolean","SPLIT",EDGE,{"disambiguationData":[TD([makeQuery(id+"F2.opShell","OFFSET_FACE",FACE,{"disambiguationData":[OSD([subQ0])]})])],"derivedFrom":makeQuery(id+"F2.opShell","OFFSET_EDGE",EDGE,{"disambiguationData":[OSD([subQ1]),TDD([makeQuery(id+"F1.opExtrude","CAP_EDGE",EDGE,{"disambiguationData":[OSD([subQ1])],"isStart":true})])]})});}
            var Q7;
            Q7=makeQuery(id+"F8.opChamfer","BLEND_EDGE",EDGE,{"blendedFrom":[makeQuery(id+"F4.opExtrude","CAP_EDGE",EDGE,{"disambiguationData":[OSD([sQuery(id+"F3.wireOp",EDGE,"E6")])],"isStart":false}),makeQuery(id+"F2.opShell","OFFSET_FACE",FACE,{"disambiguationData":[OSD([sQuery(id+"F0.wireOp",EDGE,"E0.bottom")])]})],"blendedInto":[makeQuery(id+"F2.opShell","OFFSET_FACE",FACE,{"disambiguationData":[OSD([sQuery(id+"F0.wireOp",EDGE,"E0.bottom")])]})]});
            var Q8;
            Q8=makeQuery(id+"F8.opChamfer","BLEND_EDGE",EDGE,{"blendedFrom":[makeQuery(id+"F4.opExtrude","CAP_EDGE",EDGE,{"disambiguationData":[OSD([sQuery(id+"F3.wireOp",EDGE,"E7")])],"isStart":false}),makeQuery(id+"F2.opShell","OFFSET_FACE",FACE,{"disambiguationData":[OSD([sQuery(id+"F0.wireOp",EDGE,"E0.left")])]})],"blendedInto":[makeQuery(id+"F2.opShell","OFFSET_FACE",FACE,{"disambiguationData":[OSD([sQuery(id+"F0.wireOp",EDGE,"E0.left")])]})]});
            var Q9;
            Q9=makeQuery(id+"F2.opShell","OFFSET_EDGE",EDGE,{"disambiguationData":[OSD([sQuery(id+"F0.wireOp",EDGE,"E0.bottom"),sQuery(id+"F0.wireOp",EDGE,"E0.right")])]});
            var Q10;
            Q10=makeQuery(id+"F8.opChamfer","BLEND_EDGE",EDGE,{"blendedFrom":[makeQuery(id+"F4.opExtrude","CAP_EDGE",EDGE,{"disambiguationData":[OSD([sQuery(id+"F3.wireOp",EDGE,"E9")])],"isStart":false}),makeQuery(id+"F2.opShell","OFFSET_FACE",FACE,{"disambiguationData":[OSD([sQuery(id+"F0.wireOp",EDGE,"E0.bottom")])]})],"blendedInto":[makeQuery(id+"F2.opShell","OFFSET_FACE",FACE,{"disambiguationData":[OSD([sQuery(id+"F0.wireOp",EDGE,"E0.bottom")])]})]});
            var Q11;
            Q11=makeQuery(id+"F8.opChamfer","BLEND_EDGE",EDGE,{"blendedFrom":[makeQuery(id+"F4.opExtrude","CAP_EDGE",EDGE,{"disambiguationData":[OSD([sQuery(id+"F3.wireOp",EDGE,"E8")])],"isStart":false}),makeQuery(id+"F2.opShell","OFFSET_FACE",FACE,{"disambiguationData":[OSD([sQuery(id+"F0.wireOp",EDGE,"E0.right")])]})],"blendedInto":[makeQuery(id+"F2.opShell","OFFSET_FACE",FACE,{"disambiguationData":[OSD([sQuery(id+"F0.wireOp",EDGE,"E0.right")])]})]});
            var Q12;
            {var subQ0=sQuery(id+"F0.wireOp",EDGE,"E0.right");Q12=makeQuery(id+"F2.opShell","OFFSET_EDGE",EDGE,{"disambiguationData":[OSD([subQ0]),TDD([makeQuery(id+"F1.opExtrude","CAP_EDGE",EDGE,{"disambiguationData":[OSD([subQ0])],"isStart":true})])]});}
            var Q13;
            Q13=makeQuery(id+"F2.opShell","OFFSET_EDGE",EDGE,{"disambiguationData":[OSD([sQuery(id+"F0.wireOp",EDGE,"E0.top"),sQuery(id+"F0.wireOp",EDGE,"E0.right")])]});
            var Q14;
            {var subQ0=sQuery(id+"F0.wireOp",EDGE,"E0.right");var subQ1=sQuery(id+"F0.wireOp",EDGE,"E0.top");Q14=makeQuery(id+"F11.boolean.opBoolean","SPLIT",EDGE,{"disambiguationData":[TD([makeQuery(id+"F2.opShell","OFFSET_FACE",FACE,{"disambiguationData":[OSD([subQ0])]})])],"derivedFrom":makeQuery(id+"F2.opShell","OFFSET_EDGE",EDGE,{"disambiguationData":[OSD([subQ1]),TDD([makeQuery(id+"F1.opExtrude","CAP_EDGE",EDGE,{"disambiguationData":[OSD([subQ1])],"isStart":true})])]})});}
            var Q15;
            {var subQ0=sQuery(id+"F0.wireOp",EDGE,"E0.right");var subQ1=sQuery(id+"F0.wireOp",EDGE,"E0.bottom");Q15=makeQuery(id+"F11.boolean.opBoolean","SPLIT",EDGE,{"disambiguationData":[TD([makeQuery(id+"F2.opShell","OFFSET_FACE",FACE,{"disambiguationData":[OSD([subQ0])]})])],"derivedFrom":makeQuery(id+"F2.opShell","OFFSET_EDGE",EDGE,{"disambiguationData":[OSD([subQ1]),TDD([makeQuery(id+"F1.opExtrude","CAP_EDGE",EDGE,{"disambiguationData":[OSD([subQ1])],"isStart":true})])]})});}
            fillet(context, id + "F16", {"entities" : qUnion([Q0, Q1, Q2, Q3, Q4, Q5, Q6, Q7, Q8, Q9, Q10, Q11, Q12, Q13, Q14, Q15]), "tangentPropagation" : true, "radius" : 1.27 * mm, "defaultsChanged" : false, "vertexSettings" : [], "allowEdgeOverflow" : false});
        }
        {
            var Q0;
            {var subQ0=sQuery(id+"F5.wireOp",EDGE,"E12.0");var subQ1=makeQuery(id+"F6.boolean.opBoolean","COPY",FACE,{"derivedFrom":makeQuery(id+"F6.opExtrude","SWEPT_FACE",FACE,{"disambiguationData":[OSD([subQ0])]})});var subQ2=sQuery(id+"F3.wireOp",EDGE,"E1.0");var subQ3=makeQuery(id+"F4.opExtrude","SWEPT_FACE",FACE,{"disambiguationData":[OSD([subQ2])]});var subQ4=sQuery(id+"F5.wireOp",EDGE,"E12.3");var subQ5=sQuery(id+"F5.wireOp",EDGE,"E12.2");var subQ6=makeQuery(id+"F6.boolean.opBoolean","COPY",FACE,{"derivedFrom":makeQuery(id+"F6.opExtrude","CAP_FACE",FACE,{"disambiguationData":[OSD([subQ0,sQuery(id+"F5.wireOp",EDGE,"E12.1"),subQ5,subQ4])],"isStart":false})});var subQ7=makeQuery(id+"F11.opExtrude","SWEPT_FACE",FACE,{"disambiguationData":[OSD([sQuery(id+"F10.wireOp",EDGE,"E14.1.14.2")])]});var subQ8=makeQuery(id+"F6.boolean.opBoolean","COPY",FACE,{"derivedFrom":makeQuery(id+"F6.opExtrude","SWEPT_FACE",FACE,{"disambiguationData":[OSD([subQ4])]})});var subQ9=sQuery(id+"F3.wireOp",EDGE,"E9");var subQ10=makeQuery(id+"F4.opExtrude","SWEPT_FACE",FACE,{"disambiguationData":[OSD([subQ9])]});var subQ11=sQuery(id+"F3.wireOp",EDGE,"E8");var subQ12=makeQuery(id+"F9.opFillet","BLEND_FACE",FACE,{"disambiguationData":[OSD([subQ11,subQ9]),TDD([makeQuery(id+"F4.opExtrude","SWEPT_EDGE",EDGE,{"disambiguationData":[OSD([subQ11,subQ9])]})])]});var subQ13=makeQuery(id+"F4.opExtrude","SWEPT_FACE",FACE,{"disambiguationData":[OSD([sQuery(id+"F3.wireOp",EDGE,"E1.3")])]});var subQ14=makeQuery(id+"F4.opExtrude","SWEPT_FACE",FACE,{"disambiguationData":[OSD([sQuery(id+"F3.wireOp",EDGE,"E1.2")])]});var subQ15=makeQuery(id+"F6.boolean.opBoolean","COPY",FACE,{"derivedFrom":makeQuery(id+"F6.opExtrude","SWEPT_FACE",FACE,{"disambiguationData":[OSD([subQ5])]})});var subQ16=makeQuery(id+"F4.opExtrude","SWEPT_FACE",FACE,{"disambiguationData":[OSD([subQ11])]});Q0=makeQuery(id+"F13.boolean.opBoolean","SPLIT",FACE,{"disambiguationData":[TD([subQ3])],"derivedFrom":makeQuery(id+"F11.boolean.opBoolean","SPLIT",FACE,{"disambiguationData":[TD([subQ3,subQ14,subQ13,subQ16,subQ10,subQ1,subQ15,subQ8,subQ12,subQ7])],"derivedFrom":subQ6})});}
            var sketch = newSketch(context, id + "F17", { "sketchPlane" : qUnion([Q0])});
            skCircle(sketch, "E28", {"center": v(10.67, 10.26) * mm, "radius": 1.02 * mm});
            skCircle(sketch, "E29", {"center": v(10.67, 170.28) * mm, "radius": 1.02 * mm});
            skCircle(sketch, "E30", {"center": v(105.92, 10.26) * mm, "radius": 1.02 * mm});
            skSolve(sketch);
        }
        {
            var Q0;
            Q0 = qSketchRegion(id + "F17", true);
            extrude(context, id + "F18", {"entities" : qUnion([Q0]), "operationType" : NewBodyOperationType.REMOVE, "oppositeDirection" : true, "depth" : 8.25 * mm, "offsetDistance" : 25.4 * mm});
        }
        {
            var Q0;
            Q0=makeQuery(id+"F18.boolean.opBoolean","COPY",EDGE,{"derivedFrom":makeQuery(id+"F18.opExtrude","CAP_EDGE",EDGE,{"disambiguationData":[OSD([sQuery(id+"F17.wireOp",EDGE,"E30")])],"isStart":false})});
            var Q1;
            Q1=makeQuery(id+"F18.boolean.opBoolean","COPY",EDGE,{"derivedFrom":makeQuery(id+"F18.opExtrude","CAP_EDGE",EDGE,{"disambiguationData":[OSD([sQuery(id+"F17.wireOp",EDGE,"E28")])],"isStart":false})});
            var Q2;
            Q2=makeQuery(id+"F18.boolean.opBoolean","COPY",EDGE,{"derivedFrom":makeQuery(id+"F18.opExtrude","CAP_EDGE",EDGE,{"disambiguationData":[OSD([sQuery(id+"F17.wireOp",EDGE,"E29")])],"isStart":false})});
            chamfer(context, id + "F19", {"entities" : qUnion([Q0, Q1, Q2]), "width" : 0.64 * mm, "tangentPropagation" : true});
        }
        {
            var Q0;
            Q0=qCreatedBy(makeId("Top.planeOp"),FACE);
            var sketch = newSketch(context, id + "F20", { "sketchPlane" : qUnion([Q0])});
            skLineSegment(sketch, "E31.top", {"start": v(168.66, 43.18) * mm, "end": v(162.3, 43.18) * mm});
            skLineSegment(sketch, "E31.right", {"start": v(162.3, 27.94) * mm, "end": v(162.3, 43.18) * mm});
            skLineSegment(sketch, "E32", {"start": v(168.66, 43.18) * mm, "end": v(168.66, 5.08) * mm});
            skLineSegment(sketch, "E33", {"start": v(168.66, 5.08) * mm, "end": v(136.9, 5.08) * mm});
            skLineSegment(sketch, "E34", {"start": v(136.9, 5.08) * mm, "end": v(136.9, 27.94) * mm});
            skLineSegment(sketch, "E35", {"start": v(136.9, 27.94) * mm, "end": v(162.3, 27.94) * mm});
            skSolve(sketch);
        }
        {
            var Q0;
            Q0 = qSketchRegion(id + "F20", true);
            extrude(context, id + "F21", {"entities" : qUnion([Q0]), "depth" : 2.41 * mm, "offsetDistance" : 25.4 * mm});
        }
        {
            var Q0;
            Q0=makeQuery(id+"F21.opExtrude","SWEPT_FACE",FACE,{"disambiguationData":[OSD([sQuery(id+"F20.wireOp",EDGE,"E31.right")])]});
            var sketch = newSketch(context, id + "F22", { "sketchPlane" : qUnion([Q0])});
            skLineSegment(sketch, "E36", {"start": v(-43.18, 0) * mm, "end": v(-40.77, 2.41) * mm});
            skLineSegment(sketch, "E37", {"start": v(-40.77, 2.41) * mm, "end": v(-43.18, 2.41) * mm});
            skLineSegment(sketch, "E38", {"start": v(-43.18, 2.41) * mm, "end": v(-43.18, 0) * mm});
            skSolve(sketch);
        }
        {
            var Q0;
            Q0 = qSketchRegion(id + "F22", true);
            extrude(context, id + "F23", {"entities" : qUnion([Q0]), "operationType" : NewBodyOperationType.REMOVE, "endBound" : BoundingType.UP_TO_NEXT, "oppositeDirection" : true, "depth" : 25.4 * mm, "offsetDistance" : 25.4 * mm});
        }
        {
            var Q0;
            Q0=makeQuery(id+"F23.boolean.opBoolean","COPY",EDGE,{"derivedFrom":makeQuery(id+"F23.opExtrude","SWEPT_EDGE",EDGE,{"disambiguationData":[OSD([sQuery(id+"F20.wireOp",EDGE,"E31.right"),sQuery(id+"F22.wireOp",EDGE,"E36"),sQuery(id+"F22.wireOp",EDGE,"E37")])]})});
            var Q1;
            Q1=makeQuery(id+"F21.opExtrude","SWEPT_EDGE",EDGE,{"disambiguationData":[OSD([sQuery(id+"F20.wireOp",EDGE,"E33"),sQuery(id+"F20.wireOp",EDGE,"E34")])]});
            var Q2;
            Q2=makeQuery(id+"F21.opExtrude","SWEPT_EDGE",EDGE,{"disambiguationData":[OSD([sQuery(id+"F20.wireOp",EDGE,"E32"),sQuery(id+"F20.wireOp",EDGE,"E33")])]});
            var Q3;
            Q3=makeQuery(id+"F21.opExtrude","SWEPT_EDGE",EDGE,{"disambiguationData":[OSD([sQuery(id+"F20.wireOp",EDGE,"E34"),sQuery(id+"F20.wireOp",EDGE,"E35")])]});
            fillet(context, id + "F24", {"entities" : qUnion([Q0, Q1, Q2, Q3]), "tangentPropagation" : true, "radius" : 1.27 * mm, "defaultsChanged" : false, "vertexSettings" : [], "allowEdgeOverflow" : false});
        }
        {
            var Q0;
            Q0=qCreatedBy(makeId("Top.planeOp"),FACE);
            var sketch = newSketch(context, id + "F25", { "sketchPlane" : qUnion([Q0])});
            skCircle(sketch, "E39", {"center": v(-133.86, 85.73) * mm, "radius": 1.02 * mm, "construction": true});
            skCircle(sketch, "E40", {"center": v(-133.86, 12.7) * mm, "radius": 1.02 * mm, "construction": true});
            skCircle(sketch, "E41", {"center": v(-12.7, 12.7) * mm, "radius": 1.02 * mm, "construction": true});
            skCircle(sketch, "E42", {"center": v(-12.7, 138.43) * mm, "radius": 1.02 * mm, "construction": true});
            skCircle(sketch, "E43", {"center": v(-12.7, 211.46) * mm, "radius": 1.02 * mm, "construction": true});
            skCircle(sketch, "E44", {"center": v(-133.86, 211.46) * mm, "radius": 1.02 * mm, "construction": true});
            skSolve(sketch);
        }
        {
            var Q0;
            Q0=qCreatedBy(makeId("Top.planeOp"),FACE);
            var sketch = newSketch(context, id + "F26", { "sketchPlane" : qUnion([Q0])});
            skLineSegment(sketch, "E45.bottom", {"start": v(-6.35, 6.48) * mm, "end": v(-140.2, 6.48) * mm});
            skLineSegment(sketch, "E45.top", {"start": v(-6.35, 217.8) * mm, "end": v(-140.2, 217.8) * mm});
            skLineSegment(sketch, "E45.left", {"start": v(-6.35, 6.48) * mm, "end": v(-6.35, 217.8) * mm});
            skLineSegment(sketch, "E45.right", {"start": v(-140.2, 6.48) * mm, "end": v(-140.2, 217.8) * mm});
            skSolve(sketch);
        }
        {
            var Q0;
            Q0 = qSketchRegion(id + "F26", true);
            extrude(context, id + "F27", {"entities" : qUnion([Q0]), "depth" : 43.18 * mm, "offsetDistance" : 25.4 * mm});
        }
        {
            var Q0;
            Q0=makeQuery(id+"F27.opExtrude","CAP_FACE",FACE,{"disambiguationData":[OSD([sQuery(id+"F26.wireOp",EDGE,"E45.bottom"),sQuery(id+"F26.wireOp",EDGE,"E45.top"),sQuery(id+"F26.wireOp",EDGE,"E45.left"),sQuery(id+"F26.wireOp",EDGE,"E45.right")])],"isStart":false});
            shell(context, id + "F28", {"entities" : qUnion([Q0]), "thickness" : 2.03 * mm});
        }
        {
            var Q0;
            Q0=makeQuery(id+"F27.opExtrude","CAP_FACE",FACE,{"disambiguationData":[OSD([sQuery(id+"F26.wireOp",EDGE,"E45.bottom"),sQuery(id+"F26.wireOp",EDGE,"E45.top"),sQuery(id+"F26.wireOp",EDGE,"E45.left"),sQuery(id+"F26.wireOp",EDGE,"E45.right")])],"isStart":false});
            var sketch = newSketch(context, id + "F29", { "sketchPlane" : qUnion([Q0])});
            skLineSegment(sketch, "E46.0", {"start": v(-16.51, 11.68) * mm, "end": v(-130.05, 11.68) * mm});
            skLineSegment(sketch, "E46.1", {"start": v(-11.56, 16.64) * mm, "end": v(-11.56, 134.37) * mm});
            skLineSegment(sketch, "E46.2", {"start": v(-16.51, 212.6) * mm, "end": v(-130.05, 212.6) * mm});
            skLineSegment(sketch, "E46.3", {"start": v(-135, 16.64) * mm, "end": v(-135, 81.66) * mm});
            skLineSegment(sketch, "E47.bottom", {"start": v(-138.18, 8.5) * mm, "end": v(-8.38, 8.5) * mm});
            skLineSegment(sketch, "E47.top", {"start": v(-138.18, 215.77) * mm, "end": v(-8.38, 215.77) * mm});
            skLineSegment(sketch, "E47.left", {"start": v(-138.18, 8.5) * mm, "end": v(-138.18, 215.77) * mm});
            skLineSegment(sketch, "E47.right", {"start": v(-8.38, 8.5) * mm, "end": v(-8.38, 215.77) * mm});
            skLineSegment(sketch, "E48.trimOffspring", {"start": v(-135, 89.79) * mm, "end": v(-135, 207.64) * mm});
            skLineSegment(sketch, "E49.trimOffspring", {"start": v(-11.56, 142.5) * mm, "end": v(-11.56, 207.64) * mm});
            skLineSegment(sketch, "E50", {"start": v(-130.05, 11.68) * mm, "end": v(-130.05, 16.64) * mm});
            skLineSegment(sketch, "E51", {"start": v(-130.05, 16.64) * mm, "end": v(-135, 16.64) * mm});
            skLineSegment(sketch, "E52", {"start": v(-130.05, 212.6) * mm, "end": v(-130.05, 207.64) * mm});
            skLineSegment(sketch, "E53", {"start": v(-130.05, 207.64) * mm, "end": v(-135, 207.64) * mm});
            skLineSegment(sketch, "E54", {"start": v(-16.51, 212.6) * mm, "end": v(-16.51, 207.64) * mm});
            skLineSegment(sketch, "E55", {"start": v(-16.51, 207.64) * mm, "end": v(-11.56, 207.64) * mm});
            skLineSegment(sketch, "E56", {"start": v(-16.51, 11.68) * mm, "end": v(-16.51, 16.64) * mm});
            skLineSegment(sketch, "E57", {"start": v(-16.51, 16.64) * mm, "end": v(-11.56, 16.64) * mm});
            skLineSegment(sketch, "E58", {"start": v(-16.51, 142.5) * mm, "end": v(-16.51, 134.37) * mm});
            skLineSegment(sketch, "E59", {"start": v(-16.51, 134.37) * mm, "end": v(-11.56, 134.37) * mm});
            skLineSegment(sketch, "E60", {"start": v(-16.51, 142.5) * mm, "end": v(-11.56, 142.5) * mm});
            skLineSegment(sketch, "E61", {"start": v(-130.05, 89.79) * mm, "end": v(-135, 89.79) * mm});
            skLineSegment(sketch, "E62", {"start": v(-130.05, 89.79) * mm, "end": v(-130.05, 81.66) * mm});
            skLineSegment(sketch, "E63", {"start": v(-130.05, 81.66) * mm, "end": v(-135, 81.66) * mm});
            skSolve(sketch);
        }
        {
            var Q0;
            Q0 = qSketchRegion(id + "F29", true);
            extrude(context, id + "F30", {"entities" : qUnion([Q0]), "operationType" : NewBodyOperationType.ADD, "oppositeDirection" : true, "depth" : 16.13 * mm, "offsetDistance" : 25.4 * mm});
        }
        {
            var Q0;
            Q0=makeQuery(id+"F30.boolean.opBoolean","MERGE",FACE,{"derivedFrom":[makeQuery(id+"F27.opExtrude","CAP_FACE",FACE,{"disambiguationData":[OSD([sQuery(id+"F26.wireOp",EDGE,"E45.bottom"),sQuery(id+"F26.wireOp",EDGE,"E45.top"),sQuery(id+"F26.wireOp",EDGE,"E45.left"),sQuery(id+"F26.wireOp",EDGE,"E45.right")])],"isStart":false}),makeQuery(id+"F30.opExtrude","CAP_FACE",FACE,{"disambiguationData":[OSD([sQuery(id+"F29.wireOp",EDGE,"E46.0"),sQuery(id+"F29.wireOp",EDGE,"E46.1"),sQuery(id+"F29.wireOp",EDGE,"E46.2"),sQuery(id+"F29.wireOp",EDGE,"E46.3"),sQuery(id+"F29.wireOp",EDGE,"E47.bottom"),sQuery(id+"F29.wireOp",EDGE,"E47.top"),sQuery(id+"F29.wireOp",EDGE,"E47.left"),sQuery(id+"F29.wireOp",EDGE,"E47.right"),sQuery(id+"F29.wireOp",EDGE,"uWxHugOf-zhmA-qJ57-9LGJ-pqTAcnEIktd7"),sQuery(id+"F29.wireOp",EDGE,"jIXdJzng-OD2u-fN7O-8gNi-9prW1kMuI1wx"),sQuery(id+"F29.wireOp",EDGE,"CFKaRoVD-wyd5-bcc1-801v-Y6PZ14qxQbg9"),sQuery(id+"F29.wireOp",EDGE,"GjyveGod-SLd1-fnku-ILoq-S772YWMfSp8S"),sQuery(id+"F29.wireOp",EDGE,"UHkL2R5a-KTLg-REzY-9cj0-lWzBasoKYknI"),sQuery(id+"F29.wireOp",EDGE,"J0Rh9hGe-oPI9-cChK-3JgH-kA8318Qk9fB8"),sQuery(id+"F29.wireOp",EDGE,"E48.trimOffspring"),sQuery(id+"F29.wireOp",EDGE,"E49.trimOffspring")])],"isStart":true})]});
            var sketch = newSketch(context, id + "F31", { "sketchPlane" : qUnion([Q0])});
            skLineSegment(sketch, "E64.0", {"start": v(-8.38, 8.5) * mm, "end": v(-138.18, 8.5) * mm});
            skLineSegment(sketch, "E64.1", {"start": v(-8.38, 8.5) * mm, "end": v(-8.38, 215.77) * mm});
            skLineSegment(sketch, "E64.2", {"start": v(-8.38, 215.77) * mm, "end": v(-138.18, 215.77) * mm});
            skLineSegment(sketch, "E64.3", {"start": v(-138.18, 8.5) * mm, "end": v(-138.18, 215.77) * mm});
            skLineSegment(sketch, "E65.0", {"start": v(-127.5, 19.18) * mm, "end": v(-19.05, 19.18) * mm});
            skLineSegment(sketch, "E65.1", {"start": v(-127.5, 205.1) * mm, "end": v(-127.5, 19.18) * mm});
            skLineSegment(sketch, "E65.2", {"start": v(-19.05, 205.1) * mm, "end": v(-127.5, 205.1) * mm});
            skLineSegment(sketch, "E65.3", {"start": v(-19.05, 19.18) * mm, "end": v(-19.05, 205.1) * mm});
            skSolve(sketch);
        }
        {
            var Q0;
            Q0 = qSketchRegion(id + "F31", true);
            extrude(context, id + "F32", {"entities" : qUnion([Q0]), "operationType" : NewBodyOperationType.REMOVE, "oppositeDirection" : true, "depth" : 2.54 * mm, "offsetDistance" : 25.4 * mm});
        }
        {
            var Q0;
            Q0=makeQuery(id+"F30.opExtrude","CAP_EDGE",EDGE,{"disambiguationData":[OSD([sQuery(id+"F29.wireOp",EDGE,"E46.3")])],"isStart":false});
            var Q1;
            Q1=makeQuery(id+"F30.opExtrude","CAP_EDGE",EDGE,{"disambiguationData":[OSD([sQuery(id+"F29.wireOp",EDGE,"E48.trimOffspring")])],"isStart":false});
            var Q2;
            Q2=makeQuery(id+"F30.opExtrude","CAP_EDGE",EDGE,{"disambiguationData":[OSD([sQuery(id+"F29.wireOp",EDGE,"E46.2")])],"isStart":false});
            var Q3;
            Q3=makeQuery(id+"F30.opExtrude","CAP_EDGE",EDGE,{"disambiguationData":[OSD([sQuery(id+"F29.wireOp",EDGE,"E49.trimOffspring")])],"isStart":false});
            var Q4;
            Q4=makeQuery(id+"F30.opExtrude","CAP_EDGE",EDGE,{"disambiguationData":[OSD([sQuery(id+"F29.wireOp",EDGE,"E46.1")])],"isStart":false});
            var Q5;
            Q5=makeQuery(id+"F30.opExtrude","CAP_EDGE",EDGE,{"disambiguationData":[OSD([sQuery(id+"F29.wireOp",EDGE,"E46.0")])],"isStart":false});
            chamfer(context, id + "F33", {"entities" : qUnion([Q0, Q1, Q2, Q3, Q4, Q5]), "width" : 12.7 * mm, "tangentPropagation" : true});
        }
        {
            var Q0;
            Q0=makeQuery(id+"F30.opExtrude","CAP_EDGE",EDGE,{"disambiguationData":[OSD([sQuery(id+"F29.wireOp",EDGE,"E50")])],"isStart":false});
            var Q1;
            Q1=makeQuery(id+"F30.opExtrude","CAP_EDGE",EDGE,{"disambiguationData":[OSD([sQuery(id+"F29.wireOp",EDGE,"E51")])],"isStart":false});
            var Q2;
            Q2=makeQuery(id+"F30.opExtrude","CAP_EDGE",EDGE,{"disambiguationData":[OSD([sQuery(id+"F29.wireOp",EDGE,"E62")])],"isStart":false});
            var Q3;
            Q3=makeQuery(id+"F30.opExtrude","CAP_EDGE",EDGE,{"disambiguationData":[OSD([sQuery(id+"F29.wireOp",EDGE,"E52")])],"isStart":false});
            var Q4;
            Q4=makeQuery(id+"F30.opExtrude","CAP_EDGE",EDGE,{"disambiguationData":[OSD([sQuery(id+"F29.wireOp",EDGE,"E53")])],"isStart":false});
            var Q5;
            Q5=makeQuery(id+"F30.opExtrude","CAP_EDGE",EDGE,{"disambiguationData":[OSD([sQuery(id+"F29.wireOp",EDGE,"E55")])],"isStart":false});
            var Q6;
            Q6=makeQuery(id+"F30.opExtrude","CAP_EDGE",EDGE,{"disambiguationData":[OSD([sQuery(id+"F29.wireOp",EDGE,"E54")])],"isStart":false});
            var Q7;
            Q7=makeQuery(id+"F30.opExtrude","CAP_EDGE",EDGE,{"disambiguationData":[OSD([sQuery(id+"F29.wireOp",EDGE,"E58")])],"isStart":false});
            var Q8;
            Q8=makeQuery(id+"F30.opExtrude","CAP_EDGE",EDGE,{"disambiguationData":[OSD([sQuery(id+"F29.wireOp",EDGE,"E57")])],"isStart":false});
            var Q9;
            Q9=makeQuery(id+"F30.opExtrude","CAP_EDGE",EDGE,{"disambiguationData":[OSD([sQuery(id+"F29.wireOp",EDGE,"E56")])],"isStart":false});
            chamfer(context, id + "F34", {"entities" : qUnion([Q0, Q1, Q2, Q3, Q4, Q5, Q6, Q7, Q8, Q9]), "width" : 8.13 * mm, "tangentPropagation" : true});
        }
        {
            var Q0;
            Q0=makeQuery(id+"F33.opChamfer","BLEND_EDGE",EDGE,{"blendedFrom":[makeQuery(id+"F30.opExtrude","CAP_EDGE",EDGE,{"disambiguationData":[OSD([sQuery(id+"F29.wireOp",EDGE,"E46.0")])],"isStart":false}),makeQuery(id+"F28.opShell","OFFSET_FACE",FACE,{"disambiguationData":[OSD([sQuery(id+"F26.wireOp",EDGE,"E45.bottom")])]})],"blendedInto":[makeQuery(id+"F28.opShell","OFFSET_FACE",FACE,{"disambiguationData":[OSD([sQuery(id+"F26.wireOp",EDGE,"E45.bottom")])]})]});
            var Q1;
            Q1=makeQuery(id+"F33.opChamfer","TWEAK_EDGE",EDGE,{"derivedFrom":[makeQuery(id+"F30.opExtrude","CAP_VERTEX",VERTEX,{"disambiguationData":[OSD([sQuery(id+"F29.wireOp",EDGE,"E46.0"),sQuery(id+"F29.wireOp",EDGE,"E50")])],"isStart":false})]});
            var Q2;
            Q2=makeQuery(id+"F34.opChamfer","BLEND_EDGE",EDGE,{"blendedFrom":[makeQuery(id+"F30.opExtrude","CAP_EDGE",EDGE,{"disambiguationData":[OSD([sQuery(id+"F29.wireOp",EDGE,"E50")])],"isStart":false}),makeQuery(id+"F28.opShell","OFFSET_FACE",FACE,{"disambiguationData":[OSD([sQuery(id+"F26.wireOp",EDGE,"E45.bottom")])]})],"blendedInto":[makeQuery(id+"F28.opShell","OFFSET_FACE",FACE,{"disambiguationData":[OSD([sQuery(id+"F26.wireOp",EDGE,"E45.bottom")])]})]});
            var Q3;
            Q3=makeQuery(id+"F34.opChamfer","BLEND_EDGE",EDGE,{"blendedFrom":[makeQuery(id+"F30.opExtrude","CAP_EDGE",EDGE,{"disambiguationData":[OSD([sQuery(id+"F29.wireOp",EDGE,"E50")])],"isStart":false}),makeQuery(id+"F30.opExtrude","CAP_EDGE",EDGE,{"disambiguationData":[OSD([sQuery(id+"F29.wireOp",EDGE,"E51")])],"isStart":false})],"blendedInto":[]});
            var Q4;
            Q4=makeQuery(id+"F34.opChamfer","BLEND_EDGE",EDGE,{"blendedFrom":[makeQuery(id+"F30.opExtrude","CAP_EDGE",EDGE,{"disambiguationData":[OSD([sQuery(id+"F29.wireOp",EDGE,"E51")])],"isStart":false}),makeQuery(id+"F28.opShell","OFFSET_FACE",FACE,{"disambiguationData":[OSD([sQuery(id+"F26.wireOp",EDGE,"E45.right")])]})],"blendedInto":[makeQuery(id+"F28.opShell","OFFSET_FACE",FACE,{"disambiguationData":[OSD([sQuery(id+"F26.wireOp",EDGE,"E45.right")])]})]});
            var Q5;
            Q5=makeQuery(id+"F33.opChamfer","TWEAK_EDGE",EDGE,{"derivedFrom":[makeQuery(id+"F30.opExtrude","CAP_VERTEX",VERTEX,{"disambiguationData":[OSD([sQuery(id+"F29.wireOp",EDGE,"E46.3"),sQuery(id+"F29.wireOp",EDGE,"E51")])],"isStart":false})]});
            var Q6;
            {var subQ0=sQuery(id+"F29.wireOp",EDGE,"E51");Q6=makeQuery(id+"F34.opChamfer","BLEND_EDGE",EDGE,{"blendedFrom":[makeQuery(id+"F30.opExtrude","CAP_EDGE",EDGE,{"disambiguationData":[OSD([subQ0])],"isStart":false}),makeQuery(id+"F30.opExtrude","SWEPT_FACE",FACE,{"disambiguationData":[OSD([subQ0])]})],"blendedInto":[makeQuery(id+"F30.opExtrude","SWEPT_FACE",FACE,{"disambiguationData":[OSD([subQ0])]})]});}
            var Q7;
            Q7=makeQuery(id+"F33.opChamfer","BLEND_EDGE",EDGE,{"blendedFrom":[makeQuery(id+"F30.opExtrude","CAP_EDGE",EDGE,{"disambiguationData":[OSD([sQuery(id+"F29.wireOp",EDGE,"E46.3")])],"isStart":false}),makeQuery(id+"F30.opExtrude","SWEPT_FACE",FACE,{"disambiguationData":[OSD([sQuery(id+"F29.wireOp",EDGE,"E51")])]})],"blendedInto":[makeQuery(id+"F30.opExtrude","SWEPT_FACE",FACE,{"disambiguationData":[OSD([sQuery(id+"F29.wireOp",EDGE,"E51")])]})]});
            var Q8;
            Q8=makeQuery(id+"F30.opExtrude","SWEPT_EDGE",EDGE,{"disambiguationData":[OSD([sQuery(id+"F29.wireOp",EDGE,"E50"),sQuery(id+"F29.wireOp",EDGE,"E51")])]});
            var Q9;
            {var subQ0=sQuery(id+"F29.wireOp",EDGE,"E50");Q9=makeQuery(id+"F34.opChamfer","BLEND_EDGE",EDGE,{"blendedFrom":[makeQuery(id+"F30.opExtrude","CAP_EDGE",EDGE,{"disambiguationData":[OSD([subQ0])],"isStart":false}),makeQuery(id+"F30.opExtrude","SWEPT_FACE",FACE,{"disambiguationData":[OSD([subQ0])]})],"blendedInto":[makeQuery(id+"F30.opExtrude","SWEPT_FACE",FACE,{"disambiguationData":[OSD([subQ0])]})]});}
            var Q10;
            Q10=makeQuery(id+"F33.opChamfer","BLEND_EDGE",EDGE,{"blendedFrom":[makeQuery(id+"F30.opExtrude","CAP_EDGE",EDGE,{"disambiguationData":[OSD([sQuery(id+"F29.wireOp",EDGE,"E46.0")])],"isStart":false}),makeQuery(id+"F30.opExtrude","SWEPT_FACE",FACE,{"disambiguationData":[OSD([sQuery(id+"F29.wireOp",EDGE,"E50")])]})],"blendedInto":[makeQuery(id+"F30.opExtrude","SWEPT_FACE",FACE,{"disambiguationData":[OSD([sQuery(id+"F29.wireOp",EDGE,"E50")])]})]});
            var Q11;
            Q11=makeQuery(id+"F30.opExtrude","SWEPT_EDGE",EDGE,{"disambiguationData":[OSD([sQuery(id+"F29.wireOp",EDGE,"E46.0"),sQuery(id+"F29.wireOp",EDGE,"E50")])]});
            var Q12;
            Q12=makeQuery(id+"F30.opExtrude","SWEPT_EDGE",EDGE,{"disambiguationData":[OSD([sQuery(id+"F29.wireOp",EDGE,"E46.3"),sQuery(id+"F29.wireOp",EDGE,"E51")])]});
            var Q13;
            Q13=makeQuery(id+"F33.opChamfer","TWEAK_EDGE",EDGE,{"derivedFrom":[makeQuery(id+"F30.opExtrude","CAP_VERTEX",VERTEX,{"disambiguationData":[OSD([sQuery(id+"F29.wireOp",EDGE,"E48.trimOffspring"),sQuery(id+"F29.wireOp",EDGE,"E61")])],"isStart":false})]});
            var Q14;
            Q14=makeQuery(id+"F34.opChamfer","BLEND_EDGE",EDGE,{"blendedFrom":[makeQuery(id+"F30.opExtrude","CAP_EDGE",EDGE,{"disambiguationData":[OSD([sQuery(id+"F29.wireOp",EDGE,"E62")])],"isStart":false}),makeQuery(id+"F30.opExtrude","SWEPT_FACE",FACE,{"disambiguationData":[OSD([sQuery(id+"F29.wireOp",EDGE,"E61")])]})],"blendedInto":[makeQuery(id+"F30.opExtrude","SWEPT_FACE",FACE,{"disambiguationData":[OSD([sQuery(id+"F29.wireOp",EDGE,"E61")])]})]});
            var Q15;
            Q15=makeQuery(id+"F34.opChamfer","BLEND_EDGE",EDGE,{"blendedFrom":[makeQuery(id+"F30.opExtrude","CAP_EDGE",EDGE,{"disambiguationData":[OSD([sQuery(id+"F29.wireOp",EDGE,"E62")])],"isStart":false}),makeQuery(id+"F28.opShell","OFFSET_FACE",FACE,{"disambiguationData":[OSD([sQuery(id+"F26.wireOp",EDGE,"E45.right")])]})],"blendedInto":[makeQuery(id+"F28.opShell","OFFSET_FACE",FACE,{"disambiguationData":[OSD([sQuery(id+"F26.wireOp",EDGE,"E45.right")])]})]});
            var Q16;
            Q16=makeQuery(id+"F34.opChamfer","BLEND_EDGE",EDGE,{"blendedFrom":[makeQuery(id+"F30.opExtrude","CAP_EDGE",EDGE,{"disambiguationData":[OSD([sQuery(id+"F29.wireOp",EDGE,"E62")])],"isStart":false}),makeQuery(id+"F30.opExtrude","SWEPT_FACE",FACE,{"disambiguationData":[OSD([sQuery(id+"F29.wireOp",EDGE,"E63")])]})],"blendedInto":[makeQuery(id+"F30.opExtrude","SWEPT_FACE",FACE,{"disambiguationData":[OSD([sQuery(id+"F29.wireOp",EDGE,"E63")])]})]});
            var Q17;
            {var subQ0=sQuery(id+"F29.wireOp",EDGE,"E62");Q17=makeQuery(id+"F34.opChamfer","BLEND_EDGE",EDGE,{"blendedFrom":[makeQuery(id+"F30.opExtrude","CAP_EDGE",EDGE,{"disambiguationData":[OSD([subQ0])],"isStart":false}),makeQuery(id+"F30.opExtrude","SWEPT_FACE",FACE,{"disambiguationData":[OSD([subQ0])]})],"blendedInto":[makeQuery(id+"F30.opExtrude","SWEPT_FACE",FACE,{"disambiguationData":[OSD([subQ0])]})]});}
            var Q18;
            Q18=makeQuery(id+"F30.opExtrude","SWEPT_EDGE",EDGE,{"disambiguationData":[OSD([sQuery(id+"F29.wireOp",EDGE,"E61"),sQuery(id+"F29.wireOp",EDGE,"E62")])]});
            var Q19;
            Q19=makeQuery(id+"F30.opExtrude","SWEPT_EDGE",EDGE,{"disambiguationData":[OSD([sQuery(id+"F29.wireOp",EDGE,"E62"),sQuery(id+"F29.wireOp",EDGE,"E63")])]});
            var Q20;
            Q20=makeQuery(id+"F33.opChamfer","BLEND_EDGE",EDGE,{"blendedFrom":[makeQuery(id+"F30.opExtrude","CAP_EDGE",EDGE,{"disambiguationData":[OSD([sQuery(id+"F29.wireOp",EDGE,"E48.trimOffspring")])],"isStart":false}),makeQuery(id+"F30.opExtrude","SWEPT_FACE",FACE,{"disambiguationData":[OSD([sQuery(id+"F29.wireOp",EDGE,"E61")])]})],"blendedInto":[makeQuery(id+"F30.opExtrude","SWEPT_FACE",FACE,{"disambiguationData":[OSD([sQuery(id+"F29.wireOp",EDGE,"E61")])]})]});
            var Q21;
            Q21=makeQuery(id+"F30.opExtrude","SWEPT_EDGE",EDGE,{"disambiguationData":[OSD([sQuery(id+"F29.wireOp",EDGE,"E48.trimOffspring"),sQuery(id+"F29.wireOp",EDGE,"E61")])]});
            var Q22;
            Q22=makeQuery(id+"F30.opExtrude","SWEPT_EDGE",EDGE,{"disambiguationData":[OSD([sQuery(id+"F29.wireOp",EDGE,"E46.3"),sQuery(id+"F29.wireOp",EDGE,"E63")])]});
            var Q23;
            Q23=makeQuery(id+"F33.opChamfer","BLEND_EDGE",EDGE,{"blendedFrom":[makeQuery(id+"F30.opExtrude","CAP_EDGE",EDGE,{"disambiguationData":[OSD([sQuery(id+"F29.wireOp",EDGE,"E46.3")])],"isStart":false}),makeQuery(id+"F30.opExtrude","SWEPT_FACE",FACE,{"disambiguationData":[OSD([sQuery(id+"F29.wireOp",EDGE,"E63")])]})],"blendedInto":[makeQuery(id+"F30.opExtrude","SWEPT_FACE",FACE,{"disambiguationData":[OSD([sQuery(id+"F29.wireOp",EDGE,"E63")])]})]});
            var Q24;
            Q24=makeQuery(id+"F34.opChamfer","BLEND_EDGE",EDGE,{"blendedFrom":[makeQuery(id+"F30.opExtrude","CAP_EDGE",EDGE,{"disambiguationData":[OSD([sQuery(id+"F29.wireOp",EDGE,"E52")])],"isStart":false}),makeQuery(id+"F28.opShell","OFFSET_FACE",FACE,{"disambiguationData":[OSD([sQuery(id+"F26.wireOp",EDGE,"E45.top")])]})],"blendedInto":[makeQuery(id+"F28.opShell","OFFSET_FACE",FACE,{"disambiguationData":[OSD([sQuery(id+"F26.wireOp",EDGE,"E45.top")])]})]});
            var Q25;
            Q25=makeQuery(id+"F34.opChamfer","BLEND_EDGE",EDGE,{"blendedFrom":[makeQuery(id+"F30.opExtrude","CAP_EDGE",EDGE,{"disambiguationData":[OSD([sQuery(id+"F29.wireOp",EDGE,"E52")])],"isStart":false}),makeQuery(id+"F30.opExtrude","CAP_EDGE",EDGE,{"disambiguationData":[OSD([sQuery(id+"F29.wireOp",EDGE,"E53")])],"isStart":false})],"blendedInto":[]});
            var Q26;
            Q26=makeQuery(id+"F34.opChamfer","BLEND_EDGE",EDGE,{"blendedFrom":[makeQuery(id+"F30.opExtrude","CAP_EDGE",EDGE,{"disambiguationData":[OSD([sQuery(id+"F29.wireOp",EDGE,"E53")])],"isStart":false}),makeQuery(id+"F28.opShell","OFFSET_FACE",FACE,{"disambiguationData":[OSD([sQuery(id+"F26.wireOp",EDGE,"E45.right")])]})],"blendedInto":[makeQuery(id+"F28.opShell","OFFSET_FACE",FACE,{"disambiguationData":[OSD([sQuery(id+"F26.wireOp",EDGE,"E45.right")])]})]});
            var Q27;
            {var subQ0=sQuery(id+"F29.wireOp",EDGE,"E53");Q27=makeQuery(id+"F34.opChamfer","BLEND_EDGE",EDGE,{"blendedFrom":[makeQuery(id+"F30.opExtrude","CAP_EDGE",EDGE,{"disambiguationData":[OSD([subQ0])],"isStart":false}),makeQuery(id+"F30.opExtrude","SWEPT_FACE",FACE,{"disambiguationData":[OSD([subQ0])]})],"blendedInto":[makeQuery(id+"F30.opExtrude","SWEPT_FACE",FACE,{"disambiguationData":[OSD([subQ0])]})]});}
            var Q28;
            {var subQ0=sQuery(id+"F29.wireOp",EDGE,"E52");Q28=makeQuery(id+"F34.opChamfer","BLEND_EDGE",EDGE,{"blendedFrom":[makeQuery(id+"F30.opExtrude","CAP_EDGE",EDGE,{"disambiguationData":[OSD([subQ0])],"isStart":false}),makeQuery(id+"F30.opExtrude","SWEPT_FACE",FACE,{"disambiguationData":[OSD([subQ0])]})],"blendedInto":[makeQuery(id+"F30.opExtrude","SWEPT_FACE",FACE,{"disambiguationData":[OSD([subQ0])]})]});}
            var Q29;
            Q29=makeQuery(id+"F33.opChamfer","TWEAK_EDGE",EDGE,{"derivedFrom":[makeQuery(id+"F30.opExtrude","CAP_VERTEX",VERTEX,{"disambiguationData":[OSD([sQuery(id+"F29.wireOp",EDGE,"E46.2"),sQuery(id+"F29.wireOp",EDGE,"E52")])],"isStart":false})]});
            var Q30;
            Q30=makeQuery(id+"F33.opChamfer","BLEND_EDGE",EDGE,{"blendedFrom":[makeQuery(id+"F30.opExtrude","CAP_EDGE",EDGE,{"disambiguationData":[OSD([sQuery(id+"F29.wireOp",EDGE,"E46.2")])],"isStart":false}),makeQuery(id+"F30.opExtrude","SWEPT_FACE",FACE,{"disambiguationData":[OSD([sQuery(id+"F29.wireOp",EDGE,"E52")])]})],"blendedInto":[makeQuery(id+"F30.opExtrude","SWEPT_FACE",FACE,{"disambiguationData":[OSD([sQuery(id+"F29.wireOp",EDGE,"E52")])]})]});
            var Q31;
            Q31=makeQuery(id+"F30.opExtrude","SWEPT_EDGE",EDGE,{"disambiguationData":[OSD([sQuery(id+"F29.wireOp",EDGE,"E46.2"),sQuery(id+"F29.wireOp",EDGE,"E52")])]});
            var Q32;
            Q32=makeQuery(id+"F30.opExtrude","SWEPT_EDGE",EDGE,{"disambiguationData":[OSD([sQuery(id+"F29.wireOp",EDGE,"E52"),sQuery(id+"F29.wireOp",EDGE,"E53")])]});
            var Q33;
            Q33=makeQuery(id+"F30.opExtrude","SWEPT_EDGE",EDGE,{"disambiguationData":[OSD([sQuery(id+"F29.wireOp",EDGE,"E48.trimOffspring"),sQuery(id+"F29.wireOp",EDGE,"E53")])]});
            var Q34;
            Q34=makeQuery(id+"F33.opChamfer","BLEND_EDGE",EDGE,{"blendedFrom":[makeQuery(id+"F30.opExtrude","CAP_EDGE",EDGE,{"disambiguationData":[OSD([sQuery(id+"F29.wireOp",EDGE,"E48.trimOffspring")])],"isStart":false}),makeQuery(id+"F30.opExtrude","SWEPT_FACE",FACE,{"disambiguationData":[OSD([sQuery(id+"F29.wireOp",EDGE,"E53")])]})],"blendedInto":[makeQuery(id+"F30.opExtrude","SWEPT_FACE",FACE,{"disambiguationData":[OSD([sQuery(id+"F29.wireOp",EDGE,"E53")])]})]});
            var Q35;
            Q35=makeQuery(id+"F34.opChamfer","BLEND_EDGE",EDGE,{"blendedFrom":[makeQuery(id+"F30.opExtrude","CAP_EDGE",EDGE,{"disambiguationData":[OSD([sQuery(id+"F29.wireOp",EDGE,"E55")])],"isStart":false}),makeQuery(id+"F28.opShell","OFFSET_FACE",FACE,{"disambiguationData":[OSD([sQuery(id+"F26.wireOp",EDGE,"E45.left")])]})],"blendedInto":[makeQuery(id+"F28.opShell","OFFSET_FACE",FACE,{"disambiguationData":[OSD([sQuery(id+"F26.wireOp",EDGE,"E45.left")])]})]});
            var Q36;
            Q36=makeQuery(id+"F34.opChamfer","BLEND_EDGE",EDGE,{"blendedFrom":[makeQuery(id+"F30.opExtrude","CAP_EDGE",EDGE,{"disambiguationData":[OSD([sQuery(id+"F29.wireOp",EDGE,"E54")])],"isStart":false}),makeQuery(id+"F30.opExtrude","CAP_EDGE",EDGE,{"disambiguationData":[OSD([sQuery(id+"F29.wireOp",EDGE,"E55")])],"isStart":false})],"blendedInto":[]});
            var Q37;
            Q37=makeQuery(id+"F34.opChamfer","BLEND_EDGE",EDGE,{"blendedFrom":[makeQuery(id+"F30.opExtrude","CAP_EDGE",EDGE,{"disambiguationData":[OSD([sQuery(id+"F29.wireOp",EDGE,"E54")])],"isStart":false}),makeQuery(id+"F28.opShell","OFFSET_FACE",FACE,{"disambiguationData":[OSD([sQuery(id+"F26.wireOp",EDGE,"E45.top")])]})],"blendedInto":[makeQuery(id+"F28.opShell","OFFSET_FACE",FACE,{"disambiguationData":[OSD([sQuery(id+"F26.wireOp",EDGE,"E45.top")])]})]});
            var Q38;
            {var subQ0=sQuery(id+"F29.wireOp",EDGE,"E54");Q38=makeQuery(id+"F34.opChamfer","BLEND_EDGE",EDGE,{"blendedFrom":[makeQuery(id+"F30.opExtrude","CAP_EDGE",EDGE,{"disambiguationData":[OSD([subQ0])],"isStart":false}),makeQuery(id+"F30.opExtrude","SWEPT_FACE",FACE,{"disambiguationData":[OSD([subQ0])]})],"blendedInto":[makeQuery(id+"F30.opExtrude","SWEPT_FACE",FACE,{"disambiguationData":[OSD([subQ0])]})]});}
            var Q39;
            {var subQ0=sQuery(id+"F29.wireOp",EDGE,"E55");Q39=makeQuery(id+"F34.opChamfer","BLEND_EDGE",EDGE,{"blendedFrom":[makeQuery(id+"F30.opExtrude","CAP_EDGE",EDGE,{"disambiguationData":[OSD([subQ0])],"isStart":false}),makeQuery(id+"F30.opExtrude","SWEPT_FACE",FACE,{"disambiguationData":[OSD([subQ0])]})],"blendedInto":[makeQuery(id+"F30.opExtrude","SWEPT_FACE",FACE,{"disambiguationData":[OSD([subQ0])]})]});}
            var Q40;
            Q40=makeQuery(id+"F33.opChamfer","TWEAK_EDGE",EDGE,{"derivedFrom":[makeQuery(id+"F30.opExtrude","CAP_VERTEX",VERTEX,{"disambiguationData":[OSD([sQuery(id+"F29.wireOp",EDGE,"E49.trimOffspring"),sQuery(id+"F29.wireOp",EDGE,"E55")])],"isStart":false})]});
            var Q41;
            Q41=makeQuery(id+"F33.opChamfer","BLEND_EDGE",EDGE,{"blendedFrom":[makeQuery(id+"F30.opExtrude","CAP_EDGE",EDGE,{"disambiguationData":[OSD([sQuery(id+"F29.wireOp",EDGE,"E49.trimOffspring")])],"isStart":false}),makeQuery(id+"F30.opExtrude","SWEPT_FACE",FACE,{"disambiguationData":[OSD([sQuery(id+"F29.wireOp",EDGE,"E55")])]})],"blendedInto":[makeQuery(id+"F30.opExtrude","SWEPT_FACE",FACE,{"disambiguationData":[OSD([sQuery(id+"F29.wireOp",EDGE,"E55")])]})]});
            var Q42;
            Q42=makeQuery(id+"F30.opExtrude","SWEPT_EDGE",EDGE,{"disambiguationData":[OSD([sQuery(id+"F29.wireOp",EDGE,"E49.trimOffspring"),sQuery(id+"F29.wireOp",EDGE,"E55")])]});
            var Q43;
            Q43=makeQuery(id+"F30.opExtrude","SWEPT_EDGE",EDGE,{"disambiguationData":[OSD([sQuery(id+"F29.wireOp",EDGE,"E54"),sQuery(id+"F29.wireOp",EDGE,"E55")])]});
            var Q44;
            Q44=makeQuery(id+"F30.opExtrude","SWEPT_EDGE",EDGE,{"disambiguationData":[OSD([sQuery(id+"F29.wireOp",EDGE,"E46.2"),sQuery(id+"F29.wireOp",EDGE,"E54")])]});
            var Q45;
            Q45=makeQuery(id+"F33.opChamfer","BLEND_EDGE",EDGE,{"blendedFrom":[makeQuery(id+"F30.opExtrude","CAP_EDGE",EDGE,{"disambiguationData":[OSD([sQuery(id+"F29.wireOp",EDGE,"E46.2")])],"isStart":false}),makeQuery(id+"F30.opExtrude","SWEPT_FACE",FACE,{"disambiguationData":[OSD([sQuery(id+"F29.wireOp",EDGE,"E54")])]})],"blendedInto":[makeQuery(id+"F30.opExtrude","SWEPT_FACE",FACE,{"disambiguationData":[OSD([sQuery(id+"F29.wireOp",EDGE,"E54")])]})]});
            var Q46;
            Q46=makeQuery(id+"F33.opChamfer","TWEAK_EDGE",EDGE,{"derivedFrom":[makeQuery(id+"F30.opExtrude","CAP_VERTEX",VERTEX,{"disambiguationData":[OSD([sQuery(id+"F29.wireOp",EDGE,"E46.1"),sQuery(id+"F29.wireOp",EDGE,"E59")])],"isStart":false})]});
            var Q47;
            Q47=makeQuery(id+"F34.opChamfer","BLEND_EDGE",EDGE,{"blendedFrom":[makeQuery(id+"F30.opExtrude","CAP_EDGE",EDGE,{"disambiguationData":[OSD([sQuery(id+"F29.wireOp",EDGE,"E58")])],"isStart":false}),makeQuery(id+"F30.opExtrude","SWEPT_FACE",FACE,{"disambiguationData":[OSD([sQuery(id+"F29.wireOp",EDGE,"E59")])]})],"blendedInto":[makeQuery(id+"F30.opExtrude","SWEPT_FACE",FACE,{"disambiguationData":[OSD([sQuery(id+"F29.wireOp",EDGE,"E59")])]})]});
            var Q48;
            Q48=makeQuery(id+"F34.opChamfer","BLEND_EDGE",EDGE,{"blendedFrom":[makeQuery(id+"F30.opExtrude","CAP_EDGE",EDGE,{"disambiguationData":[OSD([sQuery(id+"F29.wireOp",EDGE,"E58")])],"isStart":false}),makeQuery(id+"F28.opShell","OFFSET_FACE",FACE,{"disambiguationData":[OSD([sQuery(id+"F26.wireOp",EDGE,"E45.left")])]})],"blendedInto":[makeQuery(id+"F28.opShell","OFFSET_FACE",FACE,{"disambiguationData":[OSD([sQuery(id+"F26.wireOp",EDGE,"E45.left")])]})]});
            var Q49;
            Q49=makeQuery(id+"F30.opExtrude","SWEPT_EDGE",EDGE,{"disambiguationData":[OSD([sQuery(id+"F29.wireOp",EDGE,"E58"),sQuery(id+"F29.wireOp",EDGE,"E59")])]});
            var Q50;
            Q50=makeQuery(id+"F33.opChamfer","BLEND_EDGE",EDGE,{"blendedFrom":[makeQuery(id+"F30.opExtrude","CAP_EDGE",EDGE,{"disambiguationData":[OSD([sQuery(id+"F29.wireOp",EDGE,"E46.1")])],"isStart":false}),makeQuery(id+"F30.opExtrude","SWEPT_FACE",FACE,{"disambiguationData":[OSD([sQuery(id+"F29.wireOp",EDGE,"E59")])]})],"blendedInto":[makeQuery(id+"F30.opExtrude","SWEPT_FACE",FACE,{"disambiguationData":[OSD([sQuery(id+"F29.wireOp",EDGE,"E59")])]})]});
            var Q51;
            Q51=makeQuery(id+"F30.opExtrude","SWEPT_EDGE",EDGE,{"disambiguationData":[OSD([sQuery(id+"F29.wireOp",EDGE,"E46.1"),sQuery(id+"F29.wireOp",EDGE,"E59")])]});
            var Q52;
            {var subQ0=sQuery(id+"F29.wireOp",EDGE,"E58");Q52=makeQuery(id+"F34.opChamfer","BLEND_EDGE",EDGE,{"blendedFrom":[makeQuery(id+"F30.opExtrude","CAP_EDGE",EDGE,{"disambiguationData":[OSD([subQ0])],"isStart":false}),makeQuery(id+"F30.opExtrude","SWEPT_FACE",FACE,{"disambiguationData":[OSD([subQ0])]})],"blendedInto":[makeQuery(id+"F30.opExtrude","SWEPT_FACE",FACE,{"disambiguationData":[OSD([subQ0])]})]});}
            var Q53;
            Q53=makeQuery(id+"F33.opChamfer","TWEAK_EDGE",EDGE,{"derivedFrom":[makeQuery(id+"F30.opExtrude","CAP_VERTEX",VERTEX,{"disambiguationData":[OSD([sQuery(id+"F29.wireOp",EDGE,"E49.trimOffspring"),sQuery(id+"F29.wireOp",EDGE,"E60")])],"isStart":false})]});
            var Q54;
            Q54=makeQuery(id+"F34.opChamfer","BLEND_EDGE",EDGE,{"blendedFrom":[makeQuery(id+"F30.opExtrude","CAP_EDGE",EDGE,{"disambiguationData":[OSD([sQuery(id+"F29.wireOp",EDGE,"E58")])],"isStart":false}),makeQuery(id+"F30.opExtrude","SWEPT_FACE",FACE,{"disambiguationData":[OSD([sQuery(id+"F29.wireOp",EDGE,"E60")])]})],"blendedInto":[makeQuery(id+"F30.opExtrude","SWEPT_FACE",FACE,{"disambiguationData":[OSD([sQuery(id+"F29.wireOp",EDGE,"E60")])]})]});
            var Q55;
            Q55=makeQuery(id+"F30.opExtrude","SWEPT_EDGE",EDGE,{"disambiguationData":[OSD([sQuery(id+"F29.wireOp",EDGE,"E58"),sQuery(id+"F29.wireOp",EDGE,"E60")])]});
            var Q56;
            Q56=makeQuery(id+"F30.opExtrude","SWEPT_EDGE",EDGE,{"disambiguationData":[OSD([sQuery(id+"F29.wireOp",EDGE,"E49.trimOffspring"),sQuery(id+"F29.wireOp",EDGE,"E60")])]});
            var Q57;
            Q57=makeQuery(id+"F33.opChamfer","BLEND_EDGE",EDGE,{"blendedFrom":[makeQuery(id+"F30.opExtrude","CAP_EDGE",EDGE,{"disambiguationData":[OSD([sQuery(id+"F29.wireOp",EDGE,"E49.trimOffspring")])],"isStart":false}),makeQuery(id+"F30.opExtrude","SWEPT_FACE",FACE,{"disambiguationData":[OSD([sQuery(id+"F29.wireOp",EDGE,"E60")])]})],"blendedInto":[makeQuery(id+"F30.opExtrude","SWEPT_FACE",FACE,{"disambiguationData":[OSD([sQuery(id+"F29.wireOp",EDGE,"E60")])]})]});
            var Q58;
            Q58=makeQuery(id+"F34.opChamfer","BLEND_EDGE",EDGE,{"blendedFrom":[makeQuery(id+"F30.opExtrude","CAP_EDGE",EDGE,{"disambiguationData":[OSD([sQuery(id+"F29.wireOp",EDGE,"E56")])],"isStart":false}),makeQuery(id+"F28.opShell","OFFSET_FACE",FACE,{"disambiguationData":[OSD([sQuery(id+"F26.wireOp",EDGE,"E45.bottom")])]})],"blendedInto":[makeQuery(id+"F28.opShell","OFFSET_FACE",FACE,{"disambiguationData":[OSD([sQuery(id+"F26.wireOp",EDGE,"E45.bottom")])]})]});
            var Q59;
            Q59=makeQuery(id+"F34.opChamfer","BLEND_EDGE",EDGE,{"blendedFrom":[makeQuery(id+"F30.opExtrude","CAP_EDGE",EDGE,{"disambiguationData":[OSD([sQuery(id+"F29.wireOp",EDGE,"E56")])],"isStart":false}),makeQuery(id+"F30.opExtrude","CAP_EDGE",EDGE,{"disambiguationData":[OSD([sQuery(id+"F29.wireOp",EDGE,"E57")])],"isStart":false})],"blendedInto":[]});
            var Q60;
            Q60=makeQuery(id+"F34.opChamfer","BLEND_EDGE",EDGE,{"blendedFrom":[makeQuery(id+"F30.opExtrude","CAP_EDGE",EDGE,{"disambiguationData":[OSD([sQuery(id+"F29.wireOp",EDGE,"E57")])],"isStart":false}),makeQuery(id+"F28.opShell","OFFSET_FACE",FACE,{"disambiguationData":[OSD([sQuery(id+"F26.wireOp",EDGE,"E45.left")])]})],"blendedInto":[makeQuery(id+"F28.opShell","OFFSET_FACE",FACE,{"disambiguationData":[OSD([sQuery(id+"F26.wireOp",EDGE,"E45.left")])]})]});
            var Q61;
            {var subQ0=sQuery(id+"F29.wireOp",EDGE,"E57");Q61=makeQuery(id+"F34.opChamfer","BLEND_EDGE",EDGE,{"blendedFrom":[makeQuery(id+"F30.opExtrude","CAP_EDGE",EDGE,{"disambiguationData":[OSD([subQ0])],"isStart":false}),makeQuery(id+"F30.opExtrude","SWEPT_FACE",FACE,{"disambiguationData":[OSD([subQ0])]})],"blendedInto":[makeQuery(id+"F30.opExtrude","SWEPT_FACE",FACE,{"disambiguationData":[OSD([subQ0])]})]});}
            var Q62;
            {var subQ0=sQuery(id+"F29.wireOp",EDGE,"E56");Q62=makeQuery(id+"F34.opChamfer","BLEND_EDGE",EDGE,{"blendedFrom":[makeQuery(id+"F30.opExtrude","CAP_EDGE",EDGE,{"disambiguationData":[OSD([subQ0])],"isStart":false}),makeQuery(id+"F30.opExtrude","SWEPT_FACE",FACE,{"disambiguationData":[OSD([subQ0])]})],"blendedInto":[makeQuery(id+"F30.opExtrude","SWEPT_FACE",FACE,{"disambiguationData":[OSD([subQ0])]})]});}
            var Q63;
            Q63=makeQuery(id+"F33.opChamfer","TWEAK_EDGE",EDGE,{"derivedFrom":[makeQuery(id+"F30.opExtrude","CAP_VERTEX",VERTEX,{"disambiguationData":[OSD([sQuery(id+"F29.wireOp",EDGE,"E46.0"),sQuery(id+"F29.wireOp",EDGE,"E56")])],"isStart":false})]});
            var Q64;
            Q64=makeQuery(id+"F33.opChamfer","BLEND_EDGE",EDGE,{"blendedFrom":[makeQuery(id+"F30.opExtrude","CAP_EDGE",EDGE,{"disambiguationData":[OSD([sQuery(id+"F29.wireOp",EDGE,"E46.0")])],"isStart":false}),makeQuery(id+"F30.opExtrude","SWEPT_FACE",FACE,{"disambiguationData":[OSD([sQuery(id+"F29.wireOp",EDGE,"E56")])]})],"blendedInto":[makeQuery(id+"F30.opExtrude","SWEPT_FACE",FACE,{"disambiguationData":[OSD([sQuery(id+"F29.wireOp",EDGE,"E56")])]})]});
            var Q65;
            Q65=makeQuery(id+"F30.opExtrude","SWEPT_EDGE",EDGE,{"disambiguationData":[OSD([sQuery(id+"F29.wireOp",EDGE,"E56"),sQuery(id+"F29.wireOp",EDGE,"E57")])]});
            var Q66;
            Q66=makeQuery(id+"F30.opExtrude","SWEPT_EDGE",EDGE,{"disambiguationData":[OSD([sQuery(id+"F29.wireOp",EDGE,"E46.0"),sQuery(id+"F29.wireOp",EDGE,"E56")])]});
            var Q67;
            Q67=makeQuery(id+"F30.opExtrude","SWEPT_EDGE",EDGE,{"disambiguationData":[OSD([sQuery(id+"F29.wireOp",EDGE,"E46.1"),sQuery(id+"F29.wireOp",EDGE,"E57")])]});
            var Q68;
            Q68=makeQuery(id+"F33.opChamfer","BLEND_EDGE",EDGE,{"blendedFrom":[makeQuery(id+"F30.opExtrude","CAP_EDGE",EDGE,{"disambiguationData":[OSD([sQuery(id+"F29.wireOp",EDGE,"E46.1")])],"isStart":false}),makeQuery(id+"F30.opExtrude","SWEPT_FACE",FACE,{"disambiguationData":[OSD([sQuery(id+"F29.wireOp",EDGE,"E57")])]})],"blendedInto":[makeQuery(id+"F30.opExtrude","SWEPT_FACE",FACE,{"disambiguationData":[OSD([sQuery(id+"F29.wireOp",EDGE,"E57")])]})]});
            var Q69;
            Q69=makeQuery(id+"F33.opChamfer","BLEND_EDGE",EDGE,{"blendedFrom":[makeQuery(id+"F30.opExtrude","CAP_EDGE",EDGE,{"disambiguationData":[OSD([sQuery(id+"F29.wireOp",EDGE,"E48.trimOffspring")])],"isStart":false}),makeQuery(id+"F28.opShell","OFFSET_FACE",FACE,{"disambiguationData":[OSD([sQuery(id+"F26.wireOp",EDGE,"E45.right")])]})],"blendedInto":[makeQuery(id+"F28.opShell","OFFSET_FACE",FACE,{"disambiguationData":[OSD([sQuery(id+"F26.wireOp",EDGE,"E45.right")])]})]});
            var Q70;
            Q70=makeQuery(id+"F33.opChamfer","BLEND_EDGE",EDGE,{"blendedFrom":[makeQuery(id+"F30.opExtrude","CAP_EDGE",EDGE,{"disambiguationData":[OSD([sQuery(id+"F29.wireOp",EDGE,"E46.2")])],"isStart":false}),makeQuery(id+"F28.opShell","OFFSET_FACE",FACE,{"disambiguationData":[OSD([sQuery(id+"F26.wireOp",EDGE,"E45.top")])]})],"blendedInto":[makeQuery(id+"F28.opShell","OFFSET_FACE",FACE,{"disambiguationData":[OSD([sQuery(id+"F26.wireOp",EDGE,"E45.top")])]})]});
            var Q71;
            {var subQ0=sQuery(id+"F29.wireOp",EDGE,"E46.2");Q71=makeQuery(id+"F33.opChamfer","BLEND_EDGE",EDGE,{"blendedFrom":[makeQuery(id+"F30.opExtrude","CAP_EDGE",EDGE,{"disambiguationData":[OSD([subQ0])],"isStart":false}),makeQuery(id+"F30.opExtrude","SWEPT_FACE",FACE,{"disambiguationData":[OSD([subQ0])]})],"blendedInto":[makeQuery(id+"F30.opExtrude","SWEPT_FACE",FACE,{"disambiguationData":[OSD([subQ0])]})]});}
            var Q72;
            {var subQ0=sQuery(id+"F29.wireOp",EDGE,"E48.trimOffspring");Q72=makeQuery(id+"F33.opChamfer","BLEND_EDGE",EDGE,{"blendedFrom":[makeQuery(id+"F30.opExtrude","CAP_EDGE",EDGE,{"disambiguationData":[OSD([subQ0])],"isStart":false}),makeQuery(id+"F30.opExtrude","SWEPT_FACE",FACE,{"disambiguationData":[OSD([subQ0])]})],"blendedInto":[makeQuery(id+"F30.opExtrude","SWEPT_FACE",FACE,{"disambiguationData":[OSD([subQ0])]})]});}
            var Q73;
            {var subQ0=sQuery(id+"F29.wireOp",EDGE,"E46.0");Q73=makeQuery(id+"F33.opChamfer","BLEND_EDGE",EDGE,{"blendedFrom":[makeQuery(id+"F30.opExtrude","CAP_EDGE",EDGE,{"disambiguationData":[OSD([subQ0])],"isStart":false}),makeQuery(id+"F30.opExtrude","SWEPT_FACE",FACE,{"disambiguationData":[OSD([subQ0])]})],"blendedInto":[makeQuery(id+"F30.opExtrude","SWEPT_FACE",FACE,{"disambiguationData":[OSD([subQ0])]})]});}
            var Q74;
            {var subQ0=sQuery(id+"F29.wireOp",EDGE,"E46.3");Q74=makeQuery(id+"F33.opChamfer","BLEND_EDGE",EDGE,{"blendedFrom":[makeQuery(id+"F30.opExtrude","CAP_EDGE",EDGE,{"disambiguationData":[OSD([subQ0])],"isStart":false}),makeQuery(id+"F30.opExtrude","SWEPT_FACE",FACE,{"disambiguationData":[OSD([subQ0])]})],"blendedInto":[makeQuery(id+"F30.opExtrude","SWEPT_FACE",FACE,{"disambiguationData":[OSD([subQ0])]})]});}
            var Q75;
            Q75=makeQuery(id+"F33.opChamfer","BLEND_EDGE",EDGE,{"blendedFrom":[makeQuery(id+"F30.opExtrude","CAP_EDGE",EDGE,{"disambiguationData":[OSD([sQuery(id+"F29.wireOp",EDGE,"E46.3")])],"isStart":false}),makeQuery(id+"F28.opShell","OFFSET_FACE",FACE,{"disambiguationData":[OSD([sQuery(id+"F26.wireOp",EDGE,"E45.right")])]})],"blendedInto":[makeQuery(id+"F28.opShell","OFFSET_FACE",FACE,{"disambiguationData":[OSD([sQuery(id+"F26.wireOp",EDGE,"E45.right")])]})]});
            var Q76;
            {var subQ0=sQuery(id+"F29.wireOp",EDGE,"E46.1");Q76=makeQuery(id+"F33.opChamfer","BLEND_EDGE",EDGE,{"blendedFrom":[makeQuery(id+"F30.opExtrude","CAP_EDGE",EDGE,{"disambiguationData":[OSD([subQ0])],"isStart":false}),makeQuery(id+"F30.opExtrude","SWEPT_FACE",FACE,{"disambiguationData":[OSD([subQ0])]})],"blendedInto":[makeQuery(id+"F30.opExtrude","SWEPT_FACE",FACE,{"disambiguationData":[OSD([subQ0])]})]});}
            var Q77;
            Q77=makeQuery(id+"F33.opChamfer","BLEND_EDGE",EDGE,{"blendedFrom":[makeQuery(id+"F30.opExtrude","CAP_EDGE",EDGE,{"disambiguationData":[OSD([sQuery(id+"F29.wireOp",EDGE,"E46.1")])],"isStart":false}),makeQuery(id+"F28.opShell","OFFSET_FACE",FACE,{"disambiguationData":[OSD([sQuery(id+"F26.wireOp",EDGE,"E45.left")])]})],"blendedInto":[makeQuery(id+"F28.opShell","OFFSET_FACE",FACE,{"disambiguationData":[OSD([sQuery(id+"F26.wireOp",EDGE,"E45.left")])]})]});
            var Q78;
            Q78=makeQuery(id+"F28.opShell","OFFSET_EDGE",EDGE,{"disambiguationData":[OSD([sQuery(id+"F26.wireOp",EDGE,"E45.bottom"),sQuery(id+"F26.wireOp",EDGE,"E45.left")])]});
            var Q79;
            Q79=makeQuery(id+"F28.opShell","OFFSET_FACE",FACE,{"disambiguationData":[OSD([sQuery(id+"F26.wireOp",EDGE,"E45.bottom"),sQuery(id+"F26.wireOp",EDGE,"E45.top"),sQuery(id+"F26.wireOp",EDGE,"E45.left"),sQuery(id+"F26.wireOp",EDGE,"E45.right")])]});
            var Q80;
            Q80=makeQuery(id+"F28.opShell","OFFSET_EDGE",EDGE,{"disambiguationData":[OSD([sQuery(id+"F26.wireOp",EDGE,"E45.top"),sQuery(id+"F26.wireOp",EDGE,"E45.left")])]});
            var Q81;
            Q81=makeQuery(id+"F28.opShell","OFFSET_EDGE",EDGE,{"disambiguationData":[OSD([sQuery(id+"F26.wireOp",EDGE,"E45.top"),sQuery(id+"F26.wireOp",EDGE,"E45.right")])]});
            var Q82;
            Q82=makeQuery(id+"F28.opShell","OFFSET_EDGE",EDGE,{"disambiguationData":[OSD([sQuery(id+"F26.wireOp",EDGE,"E45.bottom"),sQuery(id+"F26.wireOp",EDGE,"E45.right")])]});
            fillet(context, id + "F35", {"entities" : qUnion([Q0, Q1, Q2, Q3, Q4, Q5, Q6, Q7, Q8, Q9, Q10, Q11, Q12, Q13, Q14, Q15, Q16, Q17, Q18, Q19, Q20, Q21, Q22, Q23, Q24, Q25, Q26, Q27, Q28, Q29, Q30, Q31, Q32, Q33, Q34, Q35, Q36, Q37, Q38, Q39, Q40, Q41, Q42, Q43, Q44, Q45, Q46, Q47, Q48, Q49, Q50, Q51, Q52, Q53, Q54, Q55, Q56, Q57, Q58, Q59, Q60, Q61, Q62, Q63, Q64, Q65, Q66, Q67, Q68, Q69, Q70, Q71, Q72, Q73, Q74, Q75, Q76, Q77, Q78, Q79, Q80, Q81, Q82]), "tangentPropagation" : true, "radius" : 1.27 * mm, "defaultsChanged" : false, "vertexSettings" : [], "allowEdgeOverflow" : false});
        }
        {
            var Q0;
            Q0=makeQuery(id+"F32.boolean.opBoolean","COPY",FACE,{"derivedFrom":makeQuery(id+"F32.opExtrude","CAP_FACE",FACE,{"disambiguationData":[OSD([sQuery(id+"F31.wireOp",EDGE,"E64.0"),sQuery(id+"F31.wireOp",EDGE,"E64.1"),sQuery(id+"F31.wireOp",EDGE,"E64.2"),sQuery(id+"F31.wireOp",EDGE,"E64.3"),sQuery(id+"F31.wireOp",EDGE,"E65.0"),sQuery(id+"F31.wireOp",EDGE,"E65.1"),sQuery(id+"F31.wireOp",EDGE,"E65.2"),sQuery(id+"F31.wireOp",EDGE,"E65.3")])],"isStart":false})});
            var sketch = newSketch(context, id + "F36", { "sketchPlane" : qUnion([Q0])});
            skCircle(sketch, "E66", {"center": v(-133.86, 85.72) * mm, "radius": 1.02 * mm});
            skCircle(sketch, "E67", {"center": v(-133.86, 12.7) * mm, "radius": 1.02 * mm});
            skCircle(sketch, "E68", {"center": v(-12.7, 12.7) * mm, "radius": 1.02 * mm});
            skCircle(sketch, "E69", {"center": v(-12.7, 138.43) * mm, "radius": 1.02 * mm});
            skCircle(sketch, "E70", {"center": v(-12.7, 211.45) * mm, "radius": 1.02 * mm});
            skCircle(sketch, "E71", {"center": v(-133.86, 211.45) * mm, "radius": 1.02 * mm});
            skSolve(sketch);
        }
        {
            var Q0;
            Q0 = qSketchRegion(id + "F36", true);
            extrude(context, id + "F37", {"entities" : qUnion([Q0]), "operationType" : NewBodyOperationType.REMOVE, "oppositeDirection" : true, "depth" : 8.13 * mm, "offsetDistance" : 25.4 * mm});
        }
        {
            var Q0;
            Q0=makeQuery(id+"F27.opExtrude","SWEPT_FACE",FACE,{"disambiguationData":[OSD([sQuery(id+"F26.wireOp",EDGE,"E45.top")])]});
            var sketch = newSketch(context, id + "F38", { "sketchPlane" : qUnion([Q0])});
            skLineSegment(sketch, "E72.bottom", {"start": v(20.32, 43.18) * mm, "end": v(125.6, 43.18) * mm});
            skLineSegment(sketch, "E72.top", {"start": v(30.48, 15.62) * mm, "end": v(49.53, 15.62) * mm});
            skLineSegment(sketch, "E72.left", {"start": v(20.32, 43.18) * mm, "end": v(20.32, 29.6) * mm});
            skLineSegment(sketch, "E72.right", {"start": v(125.6, 43.18) * mm, "end": v(125.6, 29.6) * mm});
            skLineSegment(sketch, "E73", {"start": v(20.32, 29.6) * mm, "end": v(30.48, 29.6) * mm});
            skLineSegment(sketch, "E74", {"start": v(30.48, 29.6) * mm, "end": v(30.48, 15.62) * mm});
            skLineSegment(sketch, "E75", {"start": v(49.53, 21.34) * mm, "end": v(49.53, 21.34) * mm});
            skLineSegment(sketch, "E76", {"start": v(49.53, 21.34) * mm, "end": v(116.08, 21.34) * mm});
            skLineSegment(sketch, "E77", {"start": v(116.08, 21.34) * mm, "end": v(116.08, 29.6) * mm});
            skLineSegment(sketch, "E78", {"start": v(116.08, 29.6) * mm, "end": v(125.6, 29.6) * mm});
            skLineSegment(sketch, "E79", {"start": v(49.53, 15.62) * mm, "end": v(49.53, 21.34) * mm});
            skSolve(sketch);
        }
        {
            var Q0;
            Q0 = qSketchRegion(id + "F38", true);
            extrude(context, id + "F39", {"entities" : qUnion([Q0]), "operationType" : NewBodyOperationType.REMOVE, "endBound" : BoundingType.UP_TO_NEXT, "oppositeDirection" : true, "depth" : 25.4 * mm, "offsetDistance" : 25.4 * mm});
        }
        {
            var Q0;
            Q0=makeQuery(id+"F32.boolean.opBoolean","COPY",FACE,{"derivedFrom":makeQuery(id+"F32.opExtrude","CAP_FACE",FACE,{"disambiguationData":[OSD([sQuery(id+"F31.wireOp",EDGE,"E64.0"),sQuery(id+"F31.wireOp",EDGE,"E64.1"),sQuery(id+"F31.wireOp",EDGE,"E64.2"),sQuery(id+"F31.wireOp",EDGE,"E64.3"),sQuery(id+"F31.wireOp",EDGE,"E65.0"),sQuery(id+"F31.wireOp",EDGE,"E65.1"),sQuery(id+"F31.wireOp",EDGE,"E65.2"),sQuery(id+"F31.wireOp",EDGE,"E65.3")])],"isStart":false})});
            var sketch = newSketch(context, id + "F40", { "sketchPlane" : qUnion([Q0])});
            skLineSegment(sketch, "E80.bottom", {"start": v(-135, 141.6) * mm, "end": v(-136.14, 141.6) * mm});
            skLineSegment(sketch, "E80.top", {"start": v(-135, 165.73) * mm, "end": v(-136.14, 165.73) * mm});
            skLineSegment(sketch, "E80.left", {"start": v(-135, 141.6) * mm, "end": v(-135, 165.73) * mm});
            skLineSegment(sketch, "E80.right", {"start": v(-136.65, 142.11) * mm, "end": v(-136.65, 165.23) * mm});
            skLineSegment(sketch, "E81.bottom", {"start": v(-135, 123.82) * mm, "end": v(-136.14, 123.82) * mm});
            skLineSegment(sketch, "E81.top", {"start": v(-135, 99.7) * mm, "end": v(-136.14, 99.7) * mm});
            skLineSegment(sketch, "E81.left", {"start": v(-135, 123.82) * mm, "end": v(-135, 99.7) * mm});
            skLineSegment(sketch, "E81.right", {"start": v(-136.65, 123.32) * mm, "end": v(-136.65, 100.2) * mm});
            skLineSegment(sketch, "E82.bottom", {"start": v(-132.84, 81.66) * mm, "end": v(-136.14, 81.66) * mm});
            skLineSegment(sketch, "E82.top", {"start": v(-132.84, 57.53) * mm, "end": v(-136.14, 57.53) * mm});
            skLineSegment(sketch, "E82.left", {"start": v(-132.84, 81.66) * mm, "end": v(-132.84, 57.53) * mm});
            skLineSegment(sketch, "E82.right", {"start": v(-136.65, 81.15) * mm, "end": v(-136.65, 58.04) * mm});
            skLineSegment(sketch, "E83.bottom", {"start": v(-136.14, 40.77) * mm, "end": v(-132.84, 40.77) * mm});
            skLineSegment(sketch, "E83.top", {"start": v(-136.14, 16.64) * mm, "end": v(-132.84, 16.64) * mm});
            skLineSegment(sketch, "E83.left", {"start": v(-136.65, 40.26) * mm, "end": v(-136.65, 17.14) * mm});
            skLineSegment(sketch, "E83.right", {"start": v(-132.84, 40.77) * mm, "end": v(-132.84, 16.64) * mm});
            skPoint(sketch, "E84.visualSharp", {"position": v(-136.65, 40.77) * mm});
            skArc(sketch, "E84.filletArc", {"start": v(-136.14, 40.77) * mm, "mid": v(-136.5, 40.62) * mm, "end": v(-136.65, 40.26) * mm});
            skPoint(sketch, "E85.visualSharp", {"position": v(-136.65, 57.53) * mm});
            skArc(sketch, "E85.filletArc", {"start": v(-136.65, 58.04) * mm, "mid": v(-136.5, 57.68) * mm, "end": v(-136.14, 57.53) * mm});
            skPoint(sketch, "E86.visualSharp", {"position": v(-136.65, 16.64) * mm});
            skArc(sketch, "E86.filletArc", {"start": v(-136.65, 17.14) * mm, "mid": v(-136.5, 16.79) * mm, "end": v(-136.14, 16.64) * mm});
            skPoint(sketch, "E87.visualSharp", {"position": v(-136.65, 81.66) * mm});
            skArc(sketch, "E87.filletArc", {"start": v(-136.14, 81.66) * mm, "mid": v(-136.5, 81.51) * mm, "end": v(-136.65, 81.15) * mm});
            skPoint(sketch, "E88.visualSharp", {"position": v(-136.65, 99.7) * mm});
            skArc(sketch, "E88.filletArc", {"start": v(-136.65, 100.2) * mm, "mid": v(-136.5, 99.84) * mm, "end": v(-136.14, 99.7) * mm});
            skPoint(sketch, "E89.visualSharp", {"position": v(-136.65, 123.82) * mm});
            skArc(sketch, "E89.filletArc", {"start": v(-136.14, 123.83) * mm, "mid": v(-136.5, 123.68) * mm, "end": v(-136.65, 123.32) * mm});
            skPoint(sketch, "E90.visualSharp", {"position": v(-136.65, 141.6) * mm});
            skArc(sketch, "E90.filletArc", {"start": v(-136.65, 142.11) * mm, "mid": v(-136.5, 141.75) * mm, "end": v(-136.14, 141.6) * mm});
            skPoint(sketch, "E91.visualSharp", {"position": v(-136.65, 165.73) * mm});
            skArc(sketch, "E91.filletArc", {"start": v(-136.14, 165.74) * mm, "mid": v(-136.5, 165.59) * mm, "end": v(-136.65, 165.23) * mm});
            skLineSegment(sketch, "E92.bottom", {"start": v(-14.03, 16.64) * mm, "end": v(-10.41, 16.64) * mm});
            skLineSegment(sketch, "E92.top", {"start": v(-14.03, 40.77) * mm, "end": v(-10.41, 40.77) * mm});
            skLineSegment(sketch, "E92.left", {"start": v(-14.03, 16.64) * mm, "end": v(-14.03, 40.77) * mm});
            skLineSegment(sketch, "E92.right", {"start": v(-9.9, 17.15) * mm, "end": v(-9.9, 40.26) * mm});
            skLineSegment(sketch, "E93.bottom", {"start": v(-10.41, 57.53) * mm, "end": v(-11.56, 57.53) * mm});
            skLineSegment(sketch, "E93.top", {"start": v(-10.41, 81.66) * mm, "end": v(-11.56, 81.66) * mm});
            skLineSegment(sketch, "E93.left", {"start": v(-9.9, 58.04) * mm, "end": v(-9.9, 81.15) * mm});
            skLineSegment(sketch, "E93.right", {"start": v(-11.56, 57.53) * mm, "end": v(-11.56, 81.66) * mm});
            skLineSegment(sketch, "E94.bottom", {"start": v(-10.41, 99.7) * mm, "end": v(-11.56, 99.7) * mm});
            skLineSegment(sketch, "E94.top", {"start": v(-10.41, 123.82) * mm, "end": v(-11.56, 123.82) * mm});
            skLineSegment(sketch, "E94.left", {"start": v(-9.9, 100.2) * mm, "end": v(-9.9, 123.32) * mm});
            skLineSegment(sketch, "E94.right", {"start": v(-11.56, 99.7) * mm, "end": v(-11.56, 123.83) * mm});
            skLineSegment(sketch, "E95.bottom", {"start": v(-14.03, 142.5) * mm, "end": v(-10.41, 142.5) * mm});
            skLineSegment(sketch, "E95.top", {"start": v(-14.03, 166.62) * mm, "end": v(-10.41, 166.62) * mm});
            skLineSegment(sketch, "E95.left", {"start": v(-14.03, 142.5) * mm, "end": v(-14.03, 166.62) * mm});
            skLineSegment(sketch, "E95.right", {"start": v(-9.9, 143) * mm, "end": v(-9.9, 166.12) * mm});
            skPoint(sketch, "E96.visualSharp", {"position": v(-9.9, 16.64) * mm});
            skArc(sketch, "E96.filletArc", {"start": v(-10.41, 16.64) * mm, "mid": v(-10.05, 16.79) * mm, "end": v(-9.9, 17.15) * mm});
            skPoint(sketch, "E97.visualSharp", {"position": v(-9.9, 40.77) * mm});
            skArc(sketch, "E97.filletArc", {"start": v(-9.9, 40.26) * mm, "mid": v(-10.05, 40.62) * mm, "end": v(-10.41, 40.77) * mm});
            skPoint(sketch, "E98.visualSharp", {"position": v(-9.9, 57.53) * mm});
            skArc(sketch, "E98.filletArc", {"start": v(-10.41, 57.53) * mm, "mid": v(-10.05, 57.68) * mm, "end": v(-9.9, 58.04) * mm});
            skPoint(sketch, "E99.visualSharp", {"position": v(-9.9, 81.66) * mm});
            skArc(sketch, "E99.filletArc", {"start": v(-9.9, 81.15) * mm, "mid": v(-10.05, 81.51) * mm, "end": v(-10.41, 81.66) * mm});
            skPoint(sketch, "E100.visualSharp", {"position": v(-9.9, 99.7) * mm});
            skArc(sketch, "E100.filletArc", {"start": v(-10.41, 99.7) * mm, "mid": v(-10.05, 99.84) * mm, "end": v(-9.9, 100.2) * mm});
            skPoint(sketch, "E101.visualSharp", {"position": v(-9.9, 123.83) * mm});
            skArc(sketch, "E101.filletArc", {"start": v(-9.9, 123.32) * mm, "mid": v(-10.05, 123.68) * mm, "end": v(-10.41, 123.83) * mm});
            skPoint(sketch, "E102.visualSharp", {"position": v(-9.9, 142.5) * mm});
            skArc(sketch, "E102.filletArc", {"start": v(-10.41, 142.5) * mm, "mid": v(-10.05, 142.64) * mm, "end": v(-9.9, 143) * mm});
            skPoint(sketch, "E103.visualSharp", {"position": v(-9.9, 166.62) * mm});
            skArc(sketch, "E103.filletArc", {"start": v(-9.9, 166.12) * mm, "mid": v(-10.05, 166.48) * mm, "end": v(-10.41, 166.62) * mm});
            skLineSegment(sketch, "E104.bottom", {"start": v(-29.08, 11.68) * mm, "end": v(-34.16, 11.68) * mm});
            skLineSegment(sketch, "E104.top", {"start": v(-29.6, 10.03) * mm, "end": v(-33.66, 10.03) * mm});
            skLineSegment(sketch, "E104.left", {"start": v(-29.08, 11.68) * mm, "end": v(-29.08, 10.54) * mm});
            skLineSegment(sketch, "E104.right", {"start": v(-34.16, 11.68) * mm, "end": v(-34.16, 10.54) * mm});
            skLineSegment(sketch, "E105.bottom", {"start": v(-46.1, 11.68) * mm, "end": v(-38.48, 11.68) * mm});
            skLineSegment(sketch, "E105.top", {"start": v(-45.6, 10.03) * mm, "end": v(-38.99, 10.03) * mm});
            skLineSegment(sketch, "E105.left", {"start": v(-46.1, 11.68) * mm, "end": v(-46.1, 10.54) * mm});
            skLineSegment(sketch, "E105.right", {"start": v(-38.48, 11.68) * mm, "end": v(-38.48, 10.54) * mm});
            skLineSegment(sketch, "E106.bottom", {"start": v(-78.49, 11.68) * mm, "end": v(-68.33, 11.68) * mm});
            skLineSegment(sketch, "E106.top", {"start": v(-77.98, 10.03) * mm, "end": v(-68.83, 10.03) * mm});
            skLineSegment(sketch, "E106.left", {"start": v(-78.49, 11.68) * mm, "end": v(-78.49, 10.54) * mm});
            skLineSegment(sketch, "E106.right", {"start": v(-68.33, 11.68) * mm, "end": v(-68.33, 10.54) * mm});
            skLineSegment(sketch, "E107.bottom", {"start": v(-117.6, 11.68) * mm, "end": v(-112.52, 11.68) * mm});
            skLineSegment(sketch, "E107.top", {"start": v(-117.1, 10.03) * mm, "end": v(-113.03, 10.03) * mm});
            skLineSegment(sketch, "E107.left", {"start": v(-117.6, 11.68) * mm, "end": v(-117.6, 10.54) * mm});
            skLineSegment(sketch, "E107.right", {"start": v(-112.52, 11.68) * mm, "end": v(-112.52, 10.54) * mm});
            skLineSegment(sketch, "E108.bottom", {"start": v(-109.47, 11.68) * mm, "end": v(-101.85, 11.68) * mm});
            skLineSegment(sketch, "E108.top", {"start": v(-108.97, 10.03) * mm, "end": v(-102.36, 10.03) * mm});
            skLineSegment(sketch, "E108.left", {"start": v(-109.47, 11.68) * mm, "end": v(-109.47, 10.54) * mm});
            skLineSegment(sketch, "E108.right", {"start": v(-101.85, 11.68) * mm, "end": v(-101.85, 10.54) * mm});
            skPoint(sketch, "E109.visualSharp", {"position": v(-117.6, 10.03) * mm});
            skArc(sketch, "E109.filletArc", {"start": v(-117.6, 10.54) * mm, "mid": v(-117.45, 10.18) * mm, "end": v(-117.1, 10.03) * mm});
            skPoint(sketch, "E110.visualSharp", {"position": v(-112.52, 10.03) * mm});
            skArc(sketch, "E110.filletArc", {"start": v(-113.03, 10.03) * mm, "mid": v(-112.67, 10.18) * mm, "end": v(-112.52, 10.54) * mm});
            skPoint(sketch, "E111.visualSharp", {"position": v(-109.47, 10.03) * mm});
            skArc(sketch, "E111.filletArc", {"start": v(-109.47, 10.54) * mm, "mid": v(-109.33, 10.18) * mm, "end": v(-108.97, 10.03) * mm});
            skPoint(sketch, "E112.visualSharp", {"position": v(-101.85, 10.03) * mm});
            skArc(sketch, "E112.filletArc", {"start": v(-102.36, 10.03) * mm, "mid": v(-102, 10.18) * mm, "end": v(-101.85, 10.54) * mm});
            skPoint(sketch, "E113.visualSharp", {"position": v(-29.08, 10.03) * mm});
            skArc(sketch, "E113.filletArc", {"start": v(-29.6, 10.03) * mm, "mid": v(-29.23, 10.18) * mm, "end": v(-29.08, 10.54) * mm});
            skPoint(sketch, "E114.visualSharp", {"position": v(-34.16, 10.03) * mm});
            skArc(sketch, "E114.filletArc", {"start": v(-34.16, 10.54) * mm, "mid": v(-34.01, 10.18) * mm, "end": v(-33.66, 10.03) * mm});
            skPoint(sketch, "E115.visualSharp", {"position": v(-38.48, 10.03) * mm});
            skArc(sketch, "E115.filletArc", {"start": v(-38.99, 10.03) * mm, "mid": v(-38.63, 10.18) * mm, "end": v(-38.48, 10.54) * mm});
            skPoint(sketch, "E116.visualSharp", {"position": v(-46.1, 10.03) * mm});
            skArc(sketch, "E116.filletArc", {"start": v(-46.1, 10.54) * mm, "mid": v(-45.95, 10.18) * mm, "end": v(-45.6, 10.03) * mm});
            skPoint(sketch, "E117.visualSharp", {"position": v(-68.33, 10.03) * mm});
            skArc(sketch, "E117.filletArc", {"start": v(-68.83, 10.03) * mm, "mid": v(-68.47, 10.18) * mm, "end": v(-68.33, 10.54) * mm});
            skPoint(sketch, "E118.visualSharp", {"position": v(-78.49, 10.03) * mm});
            skArc(sketch, "E118.filletArc", {"start": v(-78.49, 10.54) * mm, "mid": v(-78.34, 10.18) * mm, "end": v(-77.98, 10.03) * mm});
            skSolve(sketch);
        }
        {
            var Q0;
            Q0 = qSketchRegion(id + "F40", true);
            extrude(context, id + "F41", {"entities" : qUnion([Q0]), "operationType" : NewBodyOperationType.REMOVE, "endBound" : BoundingType.UP_TO_NEXT, "oppositeDirection" : true, "depth" : 6.35 * mm, "offsetDistance" : 25.4 * mm});
        }
        {
            var Q0;
            Q0=makeQuery(id+"F37.boolean.opBoolean","COPY",EDGE,{"derivedFrom":makeQuery(id+"F37.opExtrude","CAP_EDGE",EDGE,{"disambiguationData":[OSD([sQuery(id+"F36.wireOp",EDGE,"E70")])],"isStart":false})});
            var Q1;
            Q1=makeQuery(id+"F37.boolean.opBoolean","COPY",EDGE,{"derivedFrom":makeQuery(id+"F37.opExtrude","CAP_EDGE",EDGE,{"disambiguationData":[OSD([sQuery(id+"F36.wireOp",EDGE,"E69")])],"isStart":false})});
            var Q2;
            Q2=makeQuery(id+"F37.boolean.opBoolean","COPY",EDGE,{"derivedFrom":makeQuery(id+"F37.opExtrude","CAP_EDGE",EDGE,{"disambiguationData":[OSD([sQuery(id+"F36.wireOp",EDGE,"E68")])],"isStart":false})});
            var Q3;
            Q3=makeQuery(id+"F37.boolean.opBoolean","COPY",EDGE,{"derivedFrom":makeQuery(id+"F37.opExtrude","CAP_EDGE",EDGE,{"disambiguationData":[OSD([sQuery(id+"F36.wireOp",EDGE,"E67")])],"isStart":false})});
            var Q4;
            Q4=makeQuery(id+"F37.boolean.opBoolean","COPY",EDGE,{"derivedFrom":makeQuery(id+"F37.opExtrude","CAP_EDGE",EDGE,{"disambiguationData":[OSD([sQuery(id+"F36.wireOp",EDGE,"E66")])],"isStart":false})});
            var Q5;
            Q5=makeQuery(id+"F37.boolean.opBoolean","COPY",EDGE,{"derivedFrom":makeQuery(id+"F37.opExtrude","CAP_EDGE",EDGE,{"disambiguationData":[OSD([sQuery(id+"F36.wireOp",EDGE,"E71")])],"isStart":false})});
            chamfer(context, id + "F42", {"entities" : qUnion([Q0, Q1, Q2, Q3, Q4, Q5]), "width" : 0.76 * mm, "tangentPropagation" : true});
        }
        {
            var Q0;
            Q0=makeQuery(id+"F6Q6DHqaodj8CH6_3.boolean.opBoolean","MERGE",EDGE,{"derivedFrom":[makeQuery(id+"F39.boolean.opBoolean","COPY",EDGE,{"derivedFrom":makeQuery(id+"F39.opExtrude","SWEPT_EDGE",EDGE,{"disambiguationData":[OSD([sQuery(id+"F38.wireOp",EDGE,"E72.right"),sQuery(id+"F38.wireOp",EDGE,"E78")])]})}),makeQuery(id+"F6Q6DHqaodj8CH6_3.opExtrude","SWEPT_EDGE",EDGE,{"disambiguationData":[OSD([sQuery(id+"FiUHRNcbHqPxuES_3.wireOp",EDGE,"oygzeq7p-MLS2-igzD-dGiJ-hHSOEb9UHojA"),sQuery(id+"FiUHRNcbHqPxuES_3.wireOp",EDGE,"xHZ5ZZ9H-tF4x-mKbL-hhNO-h0JonNggyvqf")])]})]});
            var Q1;
            Q1=makeQuery(id+"F6Q6DHqaodj8CH6_3.boolean.opBoolean","MERGE",EDGE,{"derivedFrom":[makeQuery(id+"F39.boolean.opBoolean","COPY",EDGE,{"derivedFrom":makeQuery(id+"F39.opExtrude","SWEPT_EDGE",EDGE,{"disambiguationData":[OSD([sQuery(id+"F38.wireOp",EDGE,"E77"),sQuery(id+"F38.wireOp",EDGE,"E78")])]})}),makeQuery(id+"F6Q6DHqaodj8CH6_3.opExtrude","SWEPT_EDGE",EDGE,{"disambiguationData":[OSD([sQuery(id+"FiUHRNcbHqPxuES_3.wireOp",EDGE,"daiGrZs7-Pctx-WR9S-lftt-lhOpGEcItZlY"),sQuery(id+"FiUHRNcbHqPxuES_3.wireOp",EDGE,"oygzeq7p-MLS2-igzD-dGiJ-hHSOEb9UHojA")])]})]});
            var Q2;
            Q2=makeQuery(id+"F6Q6DHqaodj8CH6_3.boolean.opBoolean","MERGE",EDGE,{"derivedFrom":[makeQuery(id+"F39.boolean.opBoolean","COPY",EDGE,{"derivedFrom":makeQuery(id+"F39.opExtrude","SWEPT_EDGE",EDGE,{"disambiguationData":[OSD([sQuery(id+"F38.wireOp",EDGE,"E76"),sQuery(id+"F38.wireOp",EDGE,"E77")])]})}),makeQuery(id+"F6Q6DHqaodj8CH6_3.opExtrude","SWEPT_EDGE",EDGE,{"disambiguationData":[OSD([sQuery(id+"FiUHRNcbHqPxuES_3.wireOp",EDGE,"fZCV9SY4-xFrP-SUI3-byIX-KvORmpHnCNhl"),sQuery(id+"FiUHRNcbHqPxuES_3.wireOp",EDGE,"daiGrZs7-Pctx-WR9S-lftt-lhOpGEcItZlY")])]})]});
            var Q3;
            Q3=makeQuery(id+"F6Q6DHqaodj8CH6_3.boolean.opBoolean","MERGE",EDGE,{"derivedFrom":[makeQuery(id+"F39.boolean.opBoolean","COPY",EDGE,{"derivedFrom":makeQuery(id+"F39.opExtrude","SWEPT_EDGE",EDGE,{"disambiguationData":[OSD([sQuery(id+"F38.wireOp",EDGE,"E76"),sQuery(id+"F38.wireOp",EDGE,"E79")])]})}),makeQuery(id+"F6Q6DHqaodj8CH6_3.opExtrude","SWEPT_EDGE",EDGE,{"disambiguationData":[OSD([sQuery(id+"FiUHRNcbHqPxuES_3.wireOp",EDGE,"O8Pbmw58-BNNv-blfU-fIwV-TuAk36LbEc60"),sQuery(id+"FiUHRNcbHqPxuES_3.wireOp",EDGE,"fZCV9SY4-xFrP-SUI3-byIX-KvORmpHnCNhl")])]})]});
            var Q4;
            Q4=makeQuery(id+"F6Q6DHqaodj8CH6_3.boolean.opBoolean","MERGE",EDGE,{"derivedFrom":[makeQuery(id+"F39.boolean.opBoolean","COPY",EDGE,{"derivedFrom":makeQuery(id+"F39.opExtrude","SWEPT_EDGE",EDGE,{"disambiguationData":[OSD([sQuery(id+"F38.wireOp",EDGE,"E72.top"),sQuery(id+"F38.wireOp",EDGE,"E79")])]})}),makeQuery(id+"F6Q6DHqaodj8CH6_3.opExtrude","SWEPT_EDGE",EDGE,{"disambiguationData":[OSD([sQuery(id+"FiUHRNcbHqPxuES_3.wireOp",EDGE,"uEgj9GB3-BsB7-BrOw-ugyS-iQbMKxj03PTq"),sQuery(id+"FiUHRNcbHqPxuES_3.wireOp",EDGE,"O8Pbmw58-BNNv-blfU-fIwV-TuAk36LbEc60")])]})]});
            var Q5;
            Q5=makeQuery(id+"F6Q6DHqaodj8CH6_3.boolean.opBoolean","MERGE",EDGE,{"derivedFrom":[makeQuery(id+"F39.boolean.opBoolean","COPY",EDGE,{"derivedFrom":makeQuery(id+"F39.opExtrude","SWEPT_EDGE",EDGE,{"disambiguationData":[OSD([sQuery(id+"F38.wireOp",EDGE,"E72.top"),sQuery(id+"F38.wireOp",EDGE,"E74")])]})}),makeQuery(id+"F6Q6DHqaodj8CH6_3.opExtrude","SWEPT_EDGE",EDGE,{"disambiguationData":[OSD([sQuery(id+"FiUHRNcbHqPxuES_3.wireOp",EDGE,"5NWUJNZa-CUkK-0Neu-xoSp-1HFBKpICQFs8"),sQuery(id+"FiUHRNcbHqPxuES_3.wireOp",EDGE,"uEgj9GB3-BsB7-BrOw-ugyS-iQbMKxj03PTq")])]})]});
            var Q6;
            Q6=makeQuery(id+"F6Q6DHqaodj8CH6_3.boolean.opBoolean","MERGE",EDGE,{"derivedFrom":[makeQuery(id+"F39.boolean.opBoolean","COPY",EDGE,{"derivedFrom":makeQuery(id+"F39.opExtrude","SWEPT_EDGE",EDGE,{"disambiguationData":[OSD([sQuery(id+"F38.wireOp",EDGE,"E73"),sQuery(id+"F38.wireOp",EDGE,"E74")])]})}),makeQuery(id+"F6Q6DHqaodj8CH6_3.opExtrude","SWEPT_EDGE",EDGE,{"disambiguationData":[OSD([sQuery(id+"FiUHRNcbHqPxuES_3.wireOp",EDGE,"8u1KNfNl-7nHt-HDp8-XZDp-D5kYzs7wGzY3"),sQuery(id+"FiUHRNcbHqPxuES_3.wireOp",EDGE,"5NWUJNZa-CUkK-0Neu-xoSp-1HFBKpICQFs8")])]})]});
            var Q7;
            Q7=makeQuery(id+"F6Q6DHqaodj8CH6_3.boolean.opBoolean","MERGE",EDGE,{"derivedFrom":[makeQuery(id+"F39.boolean.opBoolean","COPY",EDGE,{"derivedFrom":makeQuery(id+"F39.opExtrude","SWEPT_EDGE",EDGE,{"disambiguationData":[OSD([sQuery(id+"F38.wireOp",EDGE,"E72.left"),sQuery(id+"F38.wireOp",EDGE,"E73")])]})}),makeQuery(id+"F6Q6DHqaodj8CH6_3.opExtrude","SWEPT_EDGE",EDGE,{"disambiguationData":[OSD([sQuery(id+"FiUHRNcbHqPxuES_3.wireOp",EDGE,"6XGdIO3q-NA60-IU5M-1dBi-Zzu4JKj0ONsd"),sQuery(id+"FiUHRNcbHqPxuES_3.wireOp",EDGE,"8u1KNfNl-7nHt-HDp8-XZDp-D5kYzs7wGzY3")])]})]});
            var Q8;
            Q8=makeQuery(id+"F27.opExtrude","SWEPT_EDGE",EDGE,{"disambiguationData":[OSD([sQuery(id+"F26.wireOp",EDGE,"E45.top"),sQuery(id+"F26.wireOp",EDGE,"E45.left")])]});
            var Q9;
            Q9=makeQuery(id+"F27.opExtrude","SWEPT_EDGE",EDGE,{"disambiguationData":[OSD([sQuery(id+"F26.wireOp",EDGE,"E45.top"),sQuery(id+"F26.wireOp",EDGE,"E45.right")])]});
            var Q10;
            Q10=makeQuery(id+"F27.opExtrude","SWEPT_EDGE",EDGE,{"disambiguationData":[OSD([sQuery(id+"F26.wireOp",EDGE,"E45.bottom"),sQuery(id+"F26.wireOp",EDGE,"E45.right")])]});
            var Q11;
            Q11=makeQuery(id+"F27.opExtrude","SWEPT_EDGE",EDGE,{"disambiguationData":[OSD([sQuery(id+"F26.wireOp",EDGE,"E45.bottom"),sQuery(id+"F26.wireOp",EDGE,"E45.left")])]});
            var Q12;
            Q12=makeQuery(id+"F32.boolean.opBoolean","COPY",EDGE,{"derivedFrom":makeQuery(id+"F32.opExtrude","SWEPT_EDGE",EDGE,{"disambiguationData":[OSD([sQuery(id+"F31.wireOp",EDGE,"E64.2"),sQuery(id+"F31.wireOp",EDGE,"E64.3")])]})});
            var Q13;
            Q13=makeQuery(id+"F32.boolean.opBoolean","COPY",EDGE,{"derivedFrom":makeQuery(id+"F32.opExtrude","SWEPT_EDGE",EDGE,{"disambiguationData":[OSD([sQuery(id+"F31.wireOp",EDGE,"E64.0"),sQuery(id+"F31.wireOp",EDGE,"E64.3")])]})});
            var Q14;
            Q14=makeQuery(id+"F32.boolean.opBoolean","COPY",EDGE,{"derivedFrom":makeQuery(id+"F32.opExtrude","SWEPT_EDGE",EDGE,{"disambiguationData":[OSD([sQuery(id+"F31.wireOp",EDGE,"E64.0"),sQuery(id+"F31.wireOp",EDGE,"E64.1")])]})});
            var Q15;
            Q15=makeQuery(id+"F32.boolean.opBoolean","COPY",EDGE,{"derivedFrom":makeQuery(id+"F32.opExtrude","SWEPT_EDGE",EDGE,{"disambiguationData":[OSD([sQuery(id+"F31.wireOp",EDGE,"E64.1"),sQuery(id+"F31.wireOp",EDGE,"E64.2")])]})});
            fillet(context, id + "F43", {"entities" : qUnion([Q0, Q1, Q2, Q3, Q4, Q5, Q6, Q7, Q8, Q9, Q10, Q11, Q12, Q13, Q14, Q15]), "tangentPropagation" : true, "radius" : 1.27 * mm, "defaultsChanged" : false, "vertexSettings" : [], "allowEdgeOverflow" : false});
        }
        {
            var Q0;
            Q0=makeQuery(id+"F32.boolean.opBoolean","COPY",FACE,{"derivedFrom":makeQuery(id+"F32.opExtrude","CAP_FACE",FACE,{"disambiguationData":[OSD([sQuery(id+"F31.wireOp",EDGE,"E64.0"),sQuery(id+"F31.wireOp",EDGE,"E64.1"),sQuery(id+"F31.wireOp",EDGE,"E64.2"),sQuery(id+"F31.wireOp",EDGE,"E64.3"),sQuery(id+"F31.wireOp",EDGE,"E65.0"),sQuery(id+"F31.wireOp",EDGE,"E65.1"),sQuery(id+"F31.wireOp",EDGE,"E65.2"),sQuery(id+"F31.wireOp",EDGE,"E65.3")])],"isStart":false})});
            var sketch = newSketch(context, id + "F44", { "sketchPlane" : qUnion([Q0])});
            skCircle(sketch, "E119", {"center": v(-133.86, 12.7) * mm, "radius": 3.3 * mm});
            skCircle(sketch, "E120", {"center": v(-133.86, 85.72) * mm, "radius": 3.3 * mm});
            skCircle(sketch, "E121", {"center": v(-133.86, 211.45) * mm, "radius": 3.3 * mm});
            skCircle(sketch, "E122", {"center": v(-12.7, 211.45) * mm, "radius": 3.3 * mm});
            skCircle(sketch, "E123", {"center": v(-12.7, 12.7) * mm, "radius": 3.3 * mm});
            skCircle(sketch, "E124", {"center": v(-12.7, 138.43) * mm, "radius": 3.3 * mm});
            skSolve(sketch);
        }
        {
            var Q0;
            Q0 = qSketchRegion(id + "F44", true);
            extrude(context, id + "F45", {"entities" : qUnion([Q0]), "operationType" : NewBodyOperationType.REMOVE, "oppositeDirection" : true, "depth" : 3.17 * mm, "offsetDistance" : 25.4 * mm});
        }
        {
            var Q0;
            Q0=makeQuery(id+"F45.boolean.opBoolean","COPY",EDGE,{"derivedFrom":makeQuery(id+"F45.opExtrude","CAP_EDGE",EDGE,{"disambiguationData":[OSD([sQuery(id+"F44.wireOp",EDGE,"E119")])],"isStart":false})});
            var Q1;
            Q1=makeQuery(id+"F45.boolean.opBoolean","COPY",EDGE,{"derivedFrom":makeQuery(id+"F45.opExtrude","CAP_EDGE",EDGE,{"disambiguationData":[OSD([sQuery(id+"F44.wireOp",EDGE,"E123")])],"isStart":false})});
            var Q2;
            Q2=makeQuery(id+"F45.boolean.opBoolean","COPY",EDGE,{"derivedFrom":makeQuery(id+"F45.opExtrude","CAP_EDGE",EDGE,{"disambiguationData":[OSD([sQuery(id+"F44.wireOp",EDGE,"E124")])],"isStart":false})});
            var Q3;
            Q3=makeQuery(id+"F45.boolean.opBoolean","COPY",EDGE,{"derivedFrom":makeQuery(id+"F45.opExtrude","CAP_EDGE",EDGE,{"disambiguationData":[OSD([sQuery(id+"F44.wireOp",EDGE,"E120")])],"isStart":false})});
            var Q4;
            Q4=makeQuery(id+"F45.boolean.opBoolean","COPY",EDGE,{"derivedFrom":makeQuery(id+"F45.opExtrude","CAP_EDGE",EDGE,{"disambiguationData":[OSD([sQuery(id+"F44.wireOp",EDGE,"E122")])],"isStart":false})});
            var Q5;
            Q5=makeQuery(id+"F45.boolean.opBoolean","COPY",EDGE,{"derivedFrom":makeQuery(id+"F45.opExtrude","CAP_EDGE",EDGE,{"disambiguationData":[OSD([sQuery(id+"F44.wireOp",EDGE,"E121")])],"isStart":false})});
            fillet(context, id + "F46", {"entities" : qUnion([Q0, Q1, Q2, Q3, Q4, Q5]), "tangentPropagation" : true, "radius" : 1.27 * mm, "defaultsChanged" : false, "vertexSettings" : [], "allowEdgeOverflow" : false});
        }
    });
